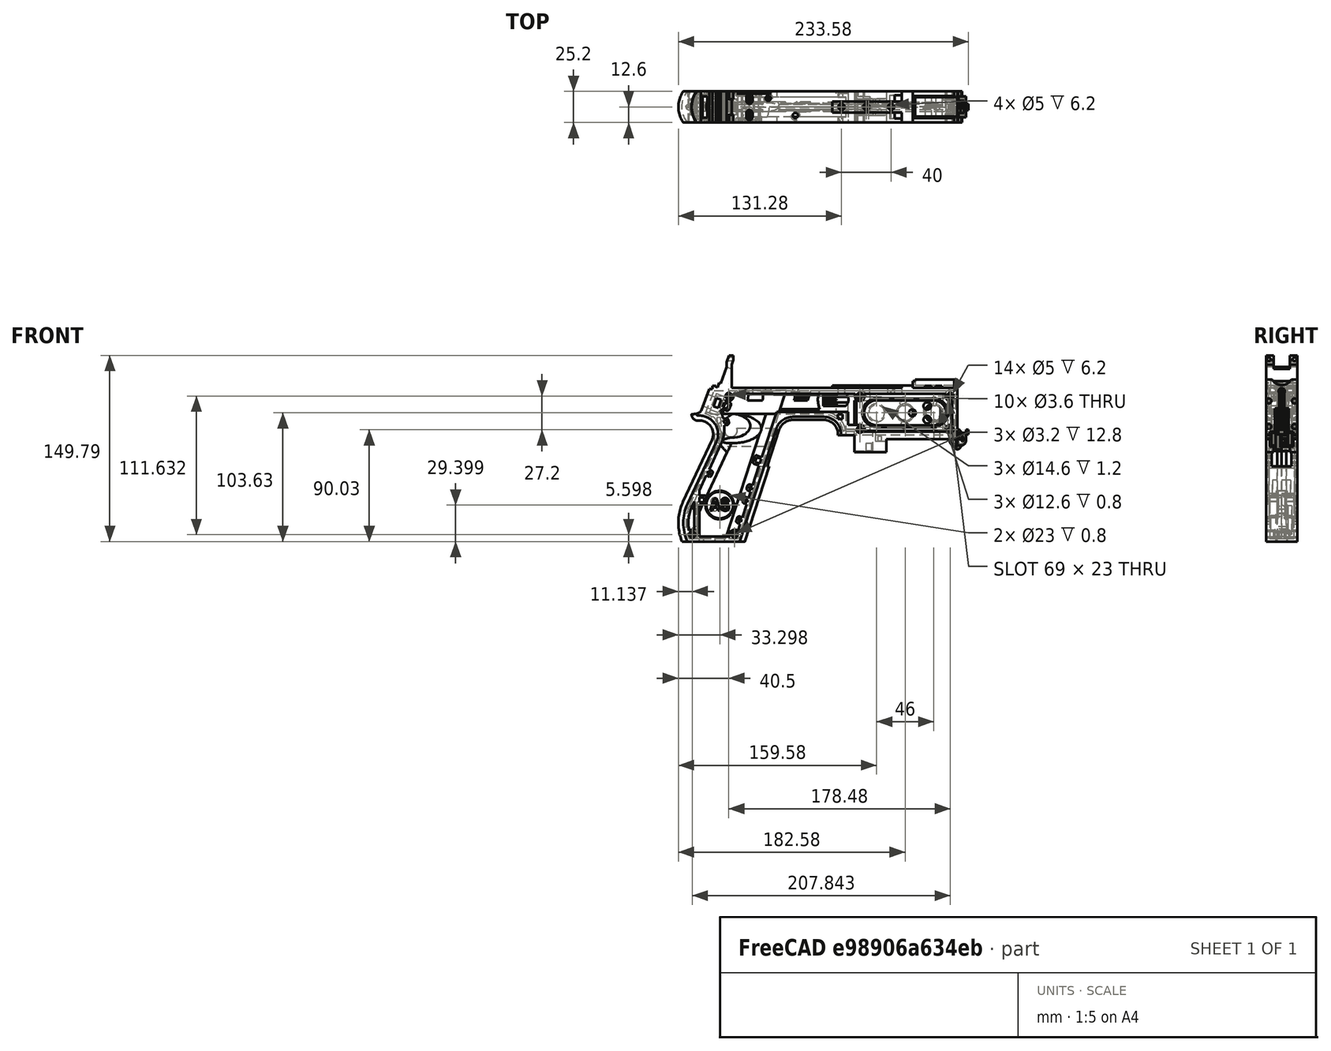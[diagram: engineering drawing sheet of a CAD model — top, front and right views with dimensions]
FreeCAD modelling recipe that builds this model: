
FCSTD DOCUMENT  (FreeCAD 1.0R39319 (Git))
Label: PICON-OF_ver_47
License: All rights reserved
LicenseURL: https://en.wikipedia.org/wiki/All_rights_reserved
objects: Sketcher::SketchObject×119, Part::Extrusion×62, Part::Cut×48, PartDesign::Pad×29, PartDesign::Pocket×18, PartDesign::Chamfer×15, PartDesign::Body×10, PartDesign::Fillet×6, Part::MultiFuse×4, Part::Part2DObjectPython×4, PartDesign::SubtractivePipe×4, PartDesign::SubtractiveLoft×4, PartDesign::Plane×2, PartDesign::SubShapeBinder×2, Part::Sweep×1, PartDesign::ShapeBinder×1, Mesh::Feature×1
note: 600 computed .brp shape members not serialized (recipe doc carries the construction recipe); baked Part::Feature solids carry a one-line shape summary decoded from their .brp

FEATURE [Sketcher::SketchObject] Sketch  label="corpo principale"
  ArcFitTolerance = 1e-06
  AttacherType = Attacher::AttachEngine3D
  AttachmentSupport = -> [XZ_Plane]
  FullyConstrained = true
  MakeInternals = false
  MapMode = 5
  Placement = pos=(0,0,0) rot=(1,0,0;1.5708rad)
  sketch-geometry (65):
    g0: LineSegment StartX=0 StartY=0 StartZ=0 EndX=-57.2 EndY=0 EndZ=0
    g1: LineSegment StartX=-57.2 StartY=0 StartZ=0 EndX=-57.2 EndY=-10.4 EndZ=0
    g2: LineSegment StartX=-57.2 StartY=-10.4 StartZ=0 EndX=-82.8 EndY=-10.4 EndZ=0
    g3: LineSegment StartX=-82.8 StartY=-10.4 StartZ=0 EndX=-82.8 EndY=3.2 EndZ=0
    g4: LineSegment StartX=-82.8 StartY=3.2 StartZ=0 EndX=-93.6 EndY=3.2 EndZ=0
    g5: LineSegment StartX=-93.6 StartY=3.2 StartZ=0 EndX=-93.6 EndY=4 EndZ=0
    g6: LineSegment StartX=-107.6 StartY=18 StartZ=0 EndX=-132.428 EndY=18 EndZ=0
    g7: LineSegment StartX=-145.743 StartY=8.32624 StartZ=0 EndX=-175.232 EndY=-82.4316 EndZ=0
    g8: LineSegment StartX=-175.232 StartY=-82.4316 StartZ=0 EndX=-217.232 EndY=-82.4316 EndZ=0
    g9: LineSegment StartX=-217.232 StartY=-52.1862 StartZ=0 EndX=-193.988 EndY=-2.33927 EndZ=0
    g10: LineSegment StartX=-206.196 StartY=23.0857 StartZ=0 EndX=-199.861 EndY=40.4914 EndZ=0
    g11: LineSegment StartX=-199.861 StartY=40.4914 StartZ=0 EndX=-197.061 EndY=40.4914 EndZ=0
    g12: LineSegment StartX=-197.061 StartY=40.4914 StartZ=0 EndX=-197.061 EndY=42.8914 EndZ=0
    g13: LineSegment StartX=-197.061 StartY=42.8914 StartZ=0 EndX=-194.261 EndY=42.8914 EndZ=0
    g14: LineSegment StartX=-194.261 StartY=42.8914 StartZ=0 EndX=-194.535 EndY=42.1397 EndZ=0
    g15: LineSegment StartX=-194.535 StartY=42.1397 StartZ=0 EndX=-193.031 EndY=41.5924 EndZ=0
    g16: LineSegment StartX=-193.031 StartY=41.5924 StartZ=0 EndX=-191.663 EndY=45.3512 EndZ=0
    g17: LineSegment StartX=-191.663 StartY=45.3512 StartZ=0 EndX=-190.536 EndY=44.9408 EndZ=0
    g18: LineSegment StartX=-190.536 StartY=44.9408 StartZ=0 EndX=-185.747 EndY=58.0965 EndZ=0
    g19: LineSegment StartX=-185.747 StartY=58.0965 StartZ=0 EndX=-185.747 EndY=62.0965 EndZ=0
    g20: LineSegment StartX=-185.747 StartY=62.0965 StartZ=0 EndX=-183.832 EndY=67.3588 EndZ=0
    g21: LineSegment StartX=-183.832 StartY=67.3588 StartZ=0 EndX=-180.232 EndY=67.3588 EndZ=0
    g22: LineSegment StartX=-180.232 StartY=67.3588 StartZ=0 EndX=-180.232 EndY=63.7588 EndZ=0
    g23: LineSegment StartX=-180.232 StartY=63.7588 StartZ=0 EndX=-181.6 EndY=60 EndZ=0
    g24: LineSegment StartX=-181.6 StartY=60 StartZ=0 EndX=-181.6 EndY=41.2 EndZ=0
    g25: LineSegment StartX=-181.6 StartY=41.2 StartZ=0 EndX=-100.8 EndY=41.2 EndZ=0
    g26: LineSegment StartX=-36 StartY=43.2 StartZ=0 EndX=-36 EndY=41.2 EndZ=0
    g27: LineSegment StartX=0 StartY=48 StartZ=0 EndX=0 EndY=0 EndZ=0
    g28: LineSegment StartX=-209.901 StartY=19.85 StartZ=0 EndX=-209.901 EndY=20.1 EndZ=0
    g29: LineSegment StartX=-208.001 StartY=22 StartZ=0 EndX=-207.747 EndY=22 EndZ=0
    g30: LineSegment StartX=-207.583 StartY=19 StartZ=0 EndX=-209.051 EndY=19 EndZ=0
    g31: ArcOfCircle CenterX=-208.001 CenterY=20.1 CenterZ=0 NormalX=0 NormalY=0 NormalZ=1 AngleXU=0 Radius=1.9 StartAngle=1.5708 EndAngle=3.14159
    g32: GeomPoint [constr] X=-209.901 Y=22 Z=0
    g33: ArcOfCircle CenterX=-209.051 CenterY=19.85 CenterZ=0 NormalX=0 NormalY=0 NormalZ=1 AngleXU=0 Radius=0.85 StartAngle=3.14159 EndAngle=4.71239
    g34: GeomPoint [constr] X=-209.901 Y=19 Z=0
    g35: ArcOfCircle CenterX=-207.747 CenterY=23.65 CenterZ=0 NormalX=0 NormalY=0 NormalZ=1 AngleXU=0 Radius=1.65 StartAngle=4.71239 EndAngle=5.93412
    g36: GeomPoint [constr] X=-206.591 Y=22 Z=0
    g37: LineSegment StartX=-4 StartY=6 StartZ=0 EndX=-4 EndY=36.4 EndZ=0
    g38: LineSegment StartX=-4 StartY=36.4 StartZ=0 EndX=-185.2 EndY=36.4 EndZ=0
    g39: LineSegment StartX=-185.2 StartY=36.4 StartZ=0 EndX=-190.441 EndY=22 EndZ=0
    g40: LineSegment StartX=-214.575 StartY=-78.4316 StartZ=0 EndX=-178.142 EndY=-78.4316 EndZ=0
    g41: LineSegment StartX=-178.142 StartY=-78.4316 StartZ=0 EndX=-145.51 EndY=22 EndZ=0
    g42: LineSegment StartX=-145.51 StartY=22 StartZ=0 EndX=-87.91 EndY=22 EndZ=0
    g43: LineSegment StartX=-87.91 StartY=22 StartZ=0 EndX=-87.91 EndY=11.6 EndZ=0
    g44: LineSegment StartX=-87.91 StartY=11.6 StartZ=0 EndX=-80.11 EndY=11.6 EndZ=0
    g45: LineSegment StartX=-80.11 StartY=11.6 StartZ=0 EndX=-80.11 EndY=6 EndZ=0
    g46: LineSegment StartX=-80.11 StartY=6 StartZ=0 EndX=-4 EndY=6 EndZ=0
    g47: LineSegment StartX=-190.363 StartY=-4.02975 StartZ=0 EndX=-213.607 EndY=-53.8767 EndZ=0
    g48: ArcOfCircle CenterX=-132.428 CenterY=4 CenterZ=0 NormalX=0 NormalY=0 NormalZ=1 AngleXU=0 Radius=14 StartAngle=1.5708 EndAngle=2.82743
    g49: GeomPoint [constr] X=-142.6 Y=18 Z=0
    g50: ArcOfCircle CenterX=-107.6 CenterY=4 CenterZ=0 NormalX=0 NormalY=0 NormalZ=1 AngleXU=0 Radius=14 StartAngle=0 EndAngle=1.5708
    g51: GeomPoint [constr] X=-93.6 Y=18 Z=0
    g52: ArcOfCircle CenterX=-184.801 CenterY=-67.3089 CenterZ=0 NormalX=0 NormalY=0 NormalZ=1 AngleXU=0 Radius=35.7833 StartAngle=2.70526 EndAngle=3.57792
    g53: ArcOfCircle CenterX=-207.583 CenterY=4 CenterZ=0 NormalX=0 NormalY=0 NormalZ=1 AngleXU=0 Radius=15 StartAngle=5.84685 EndAngle=7.85398
    g54: LineSegment [constr] StartX=-213.607 StartY=-53.8767 StartZ=0 EndX=-217.232 EndY=-52.1862 EndZ=0
    g55: ArcOfCircle CenterX=-184.801 CenterY=-67.3089 CenterZ=0 NormalX=0 NormalY=0 NormalZ=1 AngleXU=0 Radius=31.7833 StartAngle=2.70526 EndAngle=3.49911
    g56: ArcOfCircle CenterX=-218.095 CenterY=8.90192 CenterZ=0 NormalX=0 NormalY=0 NormalZ=1 AngleXU=0 Radius=30.5989 StartAngle=5.84685 EndAngle=6.72553
    g57: LineSegment StartX=-44.6 StartY=43.2 StartZ=0 EndX=-36 EndY=43.2 EndZ=0
    g58: LineSegment StartX=-100.8 StartY=41.2 StartZ=0 EndX=-44.6 EndY=41.2 EndZ=0
    g59: LineSegment StartX=-44.6 StartY=41.2 StartZ=0 EndX=-44.6 EndY=43.2 EndZ=0
    g60: LineSegment StartX=-2.4 StartY=48 StartZ=0 EndX=0 EndY=48 EndZ=0
    g61: LineSegment StartX=-36 StartY=41.2 StartZ=0 EndX=-2.4 EndY=41.2 EndZ=0
    g62: LineSegment StartX=-2.4 StartY=41.2 StartZ=0 EndX=-2.4 EndY=48 EndZ=0
    g63: LineSegment [constr] StartX=-181.6 StartY=36.4 StartZ=0 EndX=-152.209 EndY=36.4 EndZ=0
    g64: LineSegment [constr] StartX=-181.6 StartY=36.4 StartZ=0 EndX=-130.41 EndY=36.4 EndZ=0
  constraints (183):
    c: Coincident(g-1,g0)
    c: PointOnObject(g0,g-1)
    c: Coincident(g0,g1)
    c: Vertical(g1)
    c: Coincident(g1,g2)
    c: Horizontal(g2)
    c: Coincident(g2,g3)
    c: Vertical(g3)
    c: Coincident(g3,g4)
    c: Coincident(g4,g5)
    c: Vertical(g5)
    c: Horizontal(g6)
    c: Coincident(g7,g8)
    c: Horizontal(g8)
    c: Coincident(g10,g11)
    c: Horizontal(g11)
    c: Coincident(g11,g12)
    c: Vertical(g12)
    c: Coincident(g12,g13)
    c: Horizontal(g13)
    c: Coincident(g13,g14)
    c: Coincident(g14,g15)
    c: Coincident(g15,g16)
    c: Coincident(g16,g17)
    c: Coincident(g17,g18)
    c: Coincident(g18,g19)
    c: Vertical(g19)
    c: Coincident(g19,g20)
    c: Coincident(g20,g21)
    c: Horizontal(g21)
    c: Coincident(g21,g22)
    c: Vertical(g22)
    c: Coincident(g22,g23)
    c: Coincident(g23,g24)
    c: Vertical(g24)
    c: Coincident(g24,g25)
    c: Horizontal(g25)
    c: Coincident(g57,g26)
    c: Vertical(g26)
    c: Coincident(g26,g61)
    c: PointOnObject(g60,g-2)
    c: Coincident(g60,g27)
    c: Coincident(g27,g0)
    c: DistanceY(g27,g27) = 48
    c: DistanceY(g1,g1) = 10.4
    c: DistanceX(g0,g0) = 57.2
    c: DistanceX(g2,g2) = 25.6
    c: Horizontal(g4)
    c: DistanceY(g3,g3) = 13.6
    c: DistanceX(g4,g4) = 10.8
    c: DistanceY(g5,g51) = 14.8
    c: DistanceX(g49,g51) = 49
    c: Distance(g7,g49) = 105.6
    c: DistanceX(g61,g60) = 36
    c: DistanceX(g25,g25) = 80.8
    c: DistanceY(g24,g24) = 18.8
    c: DistanceY(g22,g22) = 3.6
    c: Distance(g23) = 4
    c: Angle(g-1,g23) = 1.22173
    c: DistanceX(g21,g21) = 3.6
    c: Distance(g20) = 5.6
    c: Angle(g-1,g20) = 1.22173
    c: DistanceY(g19,g19) = 4
    c: Distance(g18) = 14
    c: Angle(g-1,g18) = 1.22173
    c: Distance(g17) = 1.2
    c: Distance(g16) = 4
    c: Angle(g16) = 1.22173
    c: Perpendicular(g18,g17)
    c: Distance(g15) = 1.6
    c: Perpendicular(g16,g15)
    c: Distance(g14) = 0.8
    c: DistanceX(g13,g13) = 2.8
    c: Perpendicular(g15,g14)
    c: DistanceY(g12,g12) = 2.4
    c: DistanceX(g11,g11) = 2.8
    c: Distance(g9) = 55
    c: Angle(g9,g-1) = 2.00713
    c: Horizontal(g29)
    c: Vertical(g28)
    c: Horizontal(g30)
    c: PointOnObject(g32,g29)
    c: PointOnObject(g32,g28)
    c: Tangent(g29,g31) = 1.5708
    c: Tangent(g28,g31) = 1.5708
    c: PointOnObject(g34,g28)
    c: PointOnObject(g34,g30)
    c: Tangent(g28,g33) = 1.5708
    c: Tangent(g30,g33) = 1.5708
    c: PointOnObject(g36,g29)
    c: PointOnObject(g36,g10)
    c: Tangent(g29,g35) = -1.5708
    c: Tangent(g10,g35) = -1.5708
    c: Angle(g-1,g10) = 1.22173
    c: Radius(g35) = 1.65
    c: Vertical(g37)
    c: Coincident(g37,g38)
    c: Horizontal(g38)
    c: Coincident(g38,g39)
    c: Horizontal(g40)
    c: Coincident(g40,g41)
    c: Coincident(g41,g42)
    c: Horizontal(g42)
    c: Coincident(g42,g43)
    c: Vertical(g43)
    c: Coincident(g43,g44)
    c: Horizontal(g44)
    c: Coincident(g44,g45)
    c: Vertical(g45)
    c: Coincident(g45,g46)
    c: Coincident(g46,g37)
    c: Horizontal(g46)
    c: DistanceY(g0,g37) = 6
    c: DistanceX(g37,g0) = 4
    c: DistanceY(g37,g25) = 4.8
    c: DistanceX(g38,g38) = 181.2
    c: DistanceX(g42,g42) = 57.6
    c: DistanceY(g49,g41) = 4
    c: DistanceX(g41,g49) = 2.91
    c: DistanceY(g43,g43) = 10.4
    c: DistanceX(g44,g44) = 7.8
    c: DistanceY(g7,g40) = 4
    c: Distance(g47) = 55
    c: Angle(g-1,g39) = 1.22173
    c: PointOnObject(g49,g7)
    c: PointOnObject(g49,g6)
    c: Tangent(g7,g48) = -1.5708
    c: Tangent(g6,g48) = -1.5708
    c: PointOnObject(g51,g5)
    c: PointOnObject(g51,g6)
    c: Tangent(g5,g50) = -1.5708
    c: Tangent(g6,g50) = -1.5708
    c: Radius(g50) = 14
    c: Radius(g48) = 14
    c: DistanceX(g8,g8) = 42
    c: Angle(g7,g-1) = 1.88496
    c: Parallel(g41,g7)
    c: Parallel(g47,g9)
    c: Coincident(g52,g8)
    c: Tangent(g52,g9) = 1.5708
    c: DistanceX(g9,g8) = 0
    c: Tangent(g53,g9) = -1.5708
    c: Tangent(g53,g30) = -1.5708
    c: Diameter(g53) = 30
    c: DistanceY(g53,g0) = -4
    c: Coincident(g54,g47)
    c: Distance(g54) = 4
    c: Coincident(g54,g9)
    c: Coincident(g55,g40)
    c: Tangent(g55,g47) = -1.5708
    c: Coincident(g52,g55)
    c: Coincident(g56,g39)
    c: Tangent(g56,g47) = 1.5708
    c: Horizontal(g57)
    c: DistanceX(g57,g57) = 8.6
    c: Coincident(g58,g25)
    c: Horizontal(g58)
    c: Coincident(g59,g58)
    c: Vertical(g59)
    c: DistanceY(g58,g57) = 2
    c: DistanceX(g58,g58) = 56.2
    c: Coincident(g59,g57)
    c: DistanceY(g41,g36) = 0
    c: DistanceY(g36,g39) = 0
    c: DistanceY(g28,g28) = 0.25
    c: DistanceX(g30,g36) = 2.46
    c: DistanceX(g28,g29) = 1.9
    c: Coincident(g62,g60)
    c: Horizontal(g60)
    c: DistanceX(g62,g27) = 2.4
    c: Coincident(g61,g62)
    c: DistanceY(g26,g26) = 2
    c: Vertical(g62)
    c: DistanceY(g61,g60) = 6.8
    c: Horizontal(g61)
    c: Distance(g63) = 29.391
    c: PointOnObject(g63,g38)
    c: PointOnObject(g63,g38)
    c: Distance(g64) = 51.19
    c: PointOnObject(g64,g38)
    c: PointOnObject(g64,g38)
    c: DistanceX(g24,g63) = 0
    c: DistanceX(g24,g64) = 0
FEATURE [Part::Extrusion] Extrude  label="Extrude corpo principale"
  Base = -> Sketch
  Dir = (0,-1,2e-16)
  DirMode = 2
  FaceMakerClass = Part::FaceMakerBullseye
  FaceMakerMode = 3
  LengthFwd = 25.2
  LengthRev = 12.6
  Solid = true
  Symmetric = true
FEATURE [Sketcher::SketchObject] Sketch002  label="scavo grilletto"
  ArcFitTolerance = 1e-06
  AttachmentSupport = -> [XZ_Plane]
  ExternalGeometry = -> [Sketch]
  FullyConstrained = true
  MakeInternals = false
  MapMode = 5
  Placement = pos=(0,0,0) rot=(1,0,0;1.5708rad)
  sketch-geometry (4):
    g0: LineSegment StartX=-89.51 StartY=22 StartZ=0 EndX=-152.71 EndY=22 EndZ=0
    g1: LineSegment StartX=-152.71 StartY=22 StartZ=0 EndX=-167.006 EndY=-22 EndZ=0
    g2: LineSegment StartX=-167.006 StartY=-22 StartZ=0 EndX=-89.51 EndY=-22 EndZ=0
    g3: LineSegment StartX=-89.51 StartY=-22 StartZ=0 EndX=-89.51 EndY=22 EndZ=0
  constraints (12):
    c: Horizontal(g0)
    c: Coincident(g0,g1)
    c: Coincident(g1,g2)
    c: Horizontal(g2)
    c: Coincident(g2,g3)
    c: Coincident(g3,g0)
    c: Vertical(g3)
    c: Angle(g1,g0) = 1.88496
    c: DistanceY(g3,g3) = 44
    c: DistanceX(g0,g0) = 63.2
    c: DistanceX(g0,g-3) = 1.6
    c: DistanceY(g-3,g0) = 0
FEATURE [Sketcher::SketchObject] Sketch004  label="traiettoria arrotondamento impugnatura anteriore"
  ArcFitTolerance = 1e-06
  AttachmentSupport = -> [XZ_Plane]
  ExternalGeometry = -> [Sketch]
  FullyConstrained = true
  MakeInternals = false
  MapMode = 5
  Placement = pos=(0,0,0) rot=(1,0,0;1.5708rad)
  sketch-geometry (13):
    g0: LineSegment StartX=-175.232 StartY=-82.4316 StartZ=0 EndX=-145.743 EndY=8.32624 EndZ=0
    g1: LineSegment StartX=-93.6 StartY=3.2 StartZ=0 EndX=-93.6 EndY=4 EndZ=0
    g2: LineSegment StartX=-132.428 StartY=18 StartZ=0 EndX=-107.6 EndY=18 EndZ=0
    g3: ArcOfCircle CenterX=-132.428 CenterY=4 CenterZ=0 NormalX=0 NormalY=0 NormalZ=1 AngleXU=0 Radius=14 StartAngle=1.5708 EndAngle=2.82743
    g4: ArcOfCircle CenterX=-107.6 CenterY=4 CenterZ=0 NormalX=0 NormalY=0 NormalZ=1 AngleXU=0 Radius=14 StartAngle=0 EndAngle=1.5708
    g5: LineSegment StartX=-175.232 StartY=-82.4316 StartZ=0 EndX=-217.232 EndY=-82.4316 EndZ=0
    g6: LineSegment StartX=-217.232 StartY=-52.1862 StartZ=0 EndX=-193.988 EndY=-2.33927 EndZ=0
    g7: LineSegment StartX=-209.051 StartY=19 StartZ=0 EndX=-207.583 EndY=19 EndZ=0
    g8: LineSegment StartX=-209.901 StartY=20.1 StartZ=0 EndX=-209.901 EndY=19.85 EndZ=0
    g9: ArcOfCircle CenterX=-184.801 CenterY=-67.3089 CenterZ=0 NormalX=0 NormalY=0 NormalZ=1 AngleXU=0 Radius=35.7833 StartAngle=2.70526 EndAngle=3.57792
    g10: ArcOfCircle CenterX=-207.583 CenterY=4 CenterZ=0 NormalX=0 NormalY=0 NormalZ=1 AngleXU=0 Radius=15 StartAngle=5.84685 EndAngle=7.85398
    g11: ArcOfCircle CenterX=-209.051 CenterY=19.85 CenterZ=0 NormalX=0 NormalY=0 NormalZ=1 AngleXU=0 Radius=0.85 StartAngle=3.14159 EndAngle=4.71239
    g12: ArcOfCircle CenterX=-208.001 CenterY=20.1 CenterZ=0 NormalX=0 NormalY=0 NormalZ=1 AngleXU=0 Radius=1.9 StartAngle=1.5708 EndAngle=3.14159
  constraints (26):
    c: Coincident(g0,g-3)
    c: Coincident(g0,g-6)
    c: Coincident(g1,g-8)
    c: Coincident(g1,g-7)
    c: Coincident(g2,g-5)
    c: Coincident(g2,g-4)
    c: Coincident(g3,g2)
    c: Tangent(g3,g0) = 1.5708
    c: Coincident(g4,g1)
    c: Tangent(g4,g2) = 1.5708
    c: Coincident(g5,g0)
    c: Coincident(g5,g-9)
    c: Coincident(g6,g-12)
    c: Coincident(g6,g-11)
    c: Coincident(g7,g-15)
    c: Coincident(g7,g-14)
    c: Coincident(g8,g-16)
    c: Coincident(g8,g-17)
    c: Tangent(g9,g6) = 1.5708
    c: Coincident(g9,g5)
    c: Coincident(g10,g7)
    c: Tangent(g10,g6) = -1.5708
    c: Tangent(g11,g7) = -1.5708
    c: Coincident(g11,g8)
    c: Tangent(g12,g8) = -1.5708
    c: Coincident(g12,g-17)
FEATURE [PartDesign::Plane] DatumPlane  label="Piano per disegno arrotondamento impugnatura"
  AttachmentSupport = -> [Sketch]
  Length = 73.6581
  MapMode = 7
  Placement = pos=(-145.743,1.8e-15,8.32624) rot=(0.154555,0.154555,0.97582;1.59527rad)
  ResizeMode = 0
  Width = 303.511
FEATURE [Sketcher::SketchObject] Sketch005  label="forma arrotondamento impugnatura anteriore"
  ArcFitTolerance = 1e-06
  AttachmentSupport = -> [DatumPlane]
  FullyConstrained = true
  MakeInternals = false
  MapMode = 5
  Placement = pos=(-145.743,1.8e-15,8.32624) rot=(0.154555,0.154555,0.97582;1.59527rad)
  sketch-geometry (5):
    g0: GeomPoint [constr] X=0 Y=-4 Z=0
    g1: GeomPoint [constr] X=-12.6 Y=7.1e-15 Z=0
    g2: GeomPoint [constr] X=12.6 Y=4.97e-14 Z=0
    g3: LineSegment StartX=-12.6 StartY=7.1e-15 StartZ=0 EndX=12.6 EndY=4.97e-14 EndZ=0
    g4: ArcOfCircle CenterX=-3.88e-14 CenterY=17.845 CenterZ=0 NormalX=0 NormalY=0 NormalZ=1 AngleXU=0 Radius=21.845 StartAngle=4.09759 EndAngle=5.32718
  constraints (11):
    c: DistanceY(g0,g-1) = 4
    c: DistanceX(g-1,g0) = 0
    c: DistanceX(g1,g-1) = 12.6
    c: DistanceX(g-1,g2) = 12.6
    c: DistanceY(g-1,g2) = 0
    c: DistanceY(g-1,g1) = 0
    c: Coincident(g3,g1)
    c: Coincident(g3,g2)
    c: Coincident(g4,g1)
    c: Coincident(g4,g2)
    c: PointOnObject(g0,g4)
FEATURE [Part::Sweep] Sweep  label="Sweep impugnatura"
  Frenet = true
  Sections = -> [Sketch005]
  Solid = true
  Spine = -> Sketch [Edge32,Edge33,Edge34,Edge35,Edge36,Edge37,Edge38,Edge39,Edge40,Edge41,Edge42,Edge43,Edge44]
  Transition = 1
FEATURE [Sketcher::SketchObject] Sketch008  label="buchi e pulizie varie"
  ArcFitTolerance = 1e-06
  AttachmentSupport = -> [XZ_Plane]
  ExternalGeometry = -> [Sketch]
  FullyConstrained = true
  MakeInternals = false
  MapMode = 5
  Placement = pos=(0,0,0) rot=(1,0,0;1.5708rad)
  sketch-geometry (26):
    g0: LineSegment StartX=-96.278 StartY=20.155 StartZ=0 EndX=-92.278 EndY=20.155 EndZ=0
    g1: LineSegment StartX=-92.278 StartY=20.155 StartZ=0 EndX=-92.278 EndY=16.155 EndZ=0
    g2: LineSegment StartX=-92.278 StartY=16.155 StartZ=0 EndX=-96.278 EndY=16.155 EndZ=0
    g3: LineSegment StartX=-96.278 StartY=16.155 StartZ=0 EndX=-96.278 EndY=20.155 EndZ=0
    g4: LineSegment StartX=-222.232 StartY=-82.4316 StartZ=0 EndX=-170.232 EndY=-82.4316 EndZ=0
    g5: LineSegment StartX=-170.232 StartY=-82.4316 StartZ=0 EndX=-170.232 EndY=-86.4316 EndZ=0
    g6: LineSegment StartX=-170.232 StartY=-86.4316 StartZ=0 EndX=-222.232 EndY=-86.4316 EndZ=0
    g7: LineSegment StartX=-222.232 StartY=-86.4316 StartZ=0 EndX=-222.232 EndY=-82.4316 EndZ=0
    g8: LineSegment StartX=-213.901 StartY=20.1 StartZ=0 EndX=-213.901 EndY=26 EndZ=0
    g9: LineSegment StartX=-213.901 StartY=26 StartZ=0 EndX=-206.196 EndY=26 EndZ=0
    g10: LineSegment StartX=-17.4 StartY=42.8 StartZ=0 EndX=-12.4 EndY=42.8 EndZ=0
    g11: LineSegment StartX=-12.4 StartY=42.8 StartZ=0 EndX=-12.4 EndY=41.2 EndZ=0
    g12: LineSegment StartX=-12.4 StartY=41.2 StartZ=0 EndX=-17.4 EndY=41.2 EndZ=0
    g13: LineSegment StartX=-17.4 StartY=41.2 StartZ=0 EndX=-17.4 EndY=42.8 EndZ=0
    g14: LineSegment StartX=-25.9 StartY=42.8 StartZ=0 EndX=-20.9 EndY=42.8 EndZ=0
    g15: LineSegment StartX=-20.9 StartY=42.8 StartZ=0 EndX=-20.9 EndY=41.2 EndZ=0
    g16: LineSegment StartX=-20.9 StartY=41.2 StartZ=0 EndX=-25.9 EndY=41.2 EndZ=0
    g17: LineSegment StartX=-25.9 StartY=41.2 StartZ=0 EndX=-25.9 EndY=42.8 EndZ=0
    g18: GeomPoint [constr] X=-206.196 Y=23.0857 Z=0
    g19: GeomPoint [constr] X=-213.901 Y=20.1 Z=0
    g20: BSplineCurve PolesCount=4 KnotsCount=2 Degree=3 IsPeriodic=0
    g21-g24: Circle [constr] x4 (B-spline internal-alignment scaffolding for g20; pole/knot coordinates omitted)
    g25: LineSegment StartX=-206.196 StartY=26 StartZ=0 EndX=-206.196 EndY=23.0857 EndZ=0
  constraints (73):
    c: Horizontal(g0)
    c: Coincident(g1,g0)
    c: Vertical(g1)
    c: Coincident(g2,g1)
    c: Horizontal(g2)
    c: Coincident(g3,g2)
    c: Coincident(g3,g0)
    c: Vertical(g3)
    c: DistanceX(g0,g-4) = 4.368
    c: DistanceY(g0,g-4) = 1.845
    c: DistanceY(g1,g1) = 4
    c: DistanceX(g2,g2) = 4
    c: Horizontal(g4)
    c: Coincident(g5,g4)
    c: Vertical(g5)
    c: Coincident(g6,g5)
    c: Horizontal(g6)
    c: Coincident(g7,g6)
    c: Coincident(g7,g4)
    c: Vertical(g7)
    c: DistanceY(g7,g7) = 4
    c: DistanceX(g4,g-5) = 5
    c: DistanceX(g-5,g4) = 5
    c: DistanceY(g4,g-5) = 0
    c: Coincident(g9,g8)
    c: Parallel(g9,g-6)
    c: DistanceX(g8,g-8) = 4
    c: Horizontal(g10)
    c: Coincident(g11,g10)
    c: Vertical(g11)
    c: Coincident(g12,g11)
    c: Horizontal(g12)
    c: Coincident(g13,g12)
    c: Coincident(g13,g10)
    c: Vertical(g13)
    c: Horizontal(g14)
    c: Coincident(g15,g14)
    c: Vertical(g15)
    c: Coincident(g16,g15)
    c: Horizontal(g16)
    c: Coincident(g17,g16)
    c: Coincident(g17,g14)
    c: Vertical(g17)
    c: DistanceY(g11,g10) = 1.6
    c: DistanceX(g10,g10) = 5
    c: DistanceY(g15,g14) = 1.6
    c: DistanceX(g14,g14) = 5
    c: DistanceX(g15,g12) = 3.5
    c: DistanceX(g11,g-9) = 10
    c: DistanceY(g-9,g11) = 0
    c: DistanceY(g-9,g15) = 0
    c: Perpendicular(g8,g9)
    c: DistanceY(g-7,g9) = 4
    c: DistanceY(g8,g-8) = 0
    c: InternalAlignment(g18,g20)
    c: InternalAlignment(g19,g20)
    c: InternalAlignment(g21,g20)
    c: Weight(g21) = 1
    c: InternalAlignment(g22,g20)
    c: Equal(g22,g21)
    c: InternalAlignment(g23,g20)
    c: Equal(g23,g21)
    c: InternalAlignment(g24,g20)
    c: Equal(g24,g21)
    c: Coincident(g18,g-12)
    c: Coincident(g19,g8)
    c: Coincident(g25,g9)
    c: Coincident(g25,g20)
    c: Vertical(g25)
    c: DistanceY(g20,g23) = 0
    c: DistanceY(g22,g18) = 2.26
    c: DistanceX(g22,g18) = 0.93
    c: DistanceX(g20,g23) = 2.9
FEATURE [Part::Extrusion] Extrude004  label="Extrude Buchi e pulizie varie"
  Base = -> Sketch008
  Dir = (0,-1,2e-16)
  DirMode = 2
  FaceMakerClass = Part::FaceMakerBullseye
  FaceMakerMode = 3
  LengthFwd = 25.2
  LengthRev = 0
  Solid = true
  Symmetric = true
FEATURE [Sketcher::SketchObject] Sketch009  label="rinforzi"
  ArcFitTolerance = 1e-06
  AttachmentSupport = -> [XZ_Plane]
  ExternalGeometry = -> [Sketch]
  FullyConstrained = true
  MakeInternals = false
  MapMode = 5
  Placement = pos=(0,0,0) rot=(1,0,0;1.5708rad)
  sketch-geometry (9):
    g0: LineSegment StartX=-87.91 StartY=22 StartZ=0 EndX=-87.91 EndY=36.4 EndZ=0
    g1: LineSegment StartX=-87.91 StartY=36.4 StartZ=0 EndX=-97.91 EndY=36.4 EndZ=0
    g2: LineSegment StartX=-97.91 StartY=36.4 StartZ=0 EndX=-97.91 EndY=22 EndZ=0
    g3: LineSegment StartX=-97.91 StartY=22 StartZ=0 EndX=-87.91 EndY=22 EndZ=0
    g4: LineSegment StartX=-149.713 StartY=9.06563 StartZ=0 EndX=-154.586 EndY=-5.93437 EndZ=0
    g5: LineSegment StartX=-154.586 StartY=-5.93437 StartZ=0 EndX=-191.863 EndY=-5.93437 EndZ=0
    g6: LineSegment StartX=-191.863 StartY=-5.93437 StartZ=0 EndX=-191.863 EndY=9.06563 EndZ=0
    g7: LineSegment StartX=-191.863 StartY=9.06563 StartZ=0 EndX=-149.713 EndY=9.06563 EndZ=0
    g8: LineSegment [constr] StartX=-145.51 StartY=22 StartZ=0 EndX=-149.713 EndY=9.06563 EndZ=0
  constraints (25):
    c: Vertical(g0)
    c: Coincident(g1,g0)
    c: Horizontal(g1)
    c: Coincident(g2,g1)
    c: Vertical(g2)
    c: Coincident(g3,g2)
    c: Coincident(g3,g0)
    c: Horizontal(g3)
    c: Coincident(g0,g-4)
    c: DistanceX(g3,g3) = 10
    c: DistanceY(g0,g-3) = 0
    c: Coincident(g5,g4)
    c: Horizontal(g5)
    c: Coincident(g6,g5)
    c: Vertical(g6)
    c: Coincident(g7,g6)
    c: Coincident(g7,g4)
    c: Horizontal(g7)
    c: Distance(g8) = 13.6
    c: Parallel(g-6,g8)
    c: Coincident(g-6,g8)
    c: Parallel(g4,g-6)
    c: DistanceY(g4,g4) = 15
    c: Coincident(g4,g8)
    c: DistanceX(g-5,g5) = -1.5
FEATURE [Part::Extrusion] Extrude001  label="Extrude scavo grilletto"
  Base = -> Sketch002
  Dir = (0,-1,2e-16)
  DirMode = 2
  FaceMakerClass = Part::FaceMakerBullseye
  FaceMakerMode = 3
  LengthFwd = 16
  LengthRev = 0
  Solid = true
  Symmetric = true
FEATURE [Part::Extrusion] Extrude005  label="Extrude Rinforzi"
  Base = -> Sketch009
  Dir = (0,-1,2e-16)
  DirMode = 2
  FaceMakerClass = Part::FaceMakerBullseye
  FaceMakerMode = 3
  LengthFwd = 2
  LengthRev = 0
  Placement = pos=(0,12.6,0) rot=(0,0,1;0rad)
  Solid = true
  Symmetric = false
FEATURE [PartDesign::ShapeBinder] CopyCut
  TraceSupport = false
FEATURE [PartDesign::Plane] DatumPlane001
  AttachmentSupport = -> [CopyCut]
  Length = 283.944
  MapMode = 5
  Placement = pos=(0,12.6,0) rot=(0,0.707107,0.707107;3.14159rad)
  ResizeMode = 0
  Width = 188.15
FEATURE [Sketcher::SketchObject] Sketch010  label="buco neopixel"
  ArcFitTolerance = 1e-06
  AttachmentSupport = -> [XZ_Plane]
  ExternalGeometry = -> [Sketch]
  FullyConstrained = true
  MakeInternals = false
  MapMode = 5
  Placement = pos=(0,0,0) rot=(1,0,0;1.5708rad)
  sketch-geometry (5):
    g0: LineSegment [constr] StartX=-199.861 StartY=40.4914 StartZ=0 EndX=-201.368 EndY=36.3521 EndZ=0
    g1: LineSegment StartX=-201.368 StartY=36.3521 StartZ=0 EndX=-204.932 EndY=26.5605 EndZ=0
    g2: LineSegment StartX=-201.368 StartY=36.3521 StartZ=0 EndX=-180.2 EndY=28.6477 EndZ=0
    g3: LineSegment StartX=-180.2 StartY=28.6477 StartZ=0 EndX=-183.764 EndY=18.8561 EndZ=0
    g4: LineSegment StartX=-183.764 StartY=18.8561 StartZ=0 EndX=-204.932 EndY=26.5605 EndZ=0
  constraints (14):
    c: Parallel(g0,g-3)
    c: Distance(g0) = 4.405
    c: Coincident(g0,g-3)
    c: Coincident(g2,g1)
    c: Coincident(g3,g2)
    c: Coincident(g4,g3)
    c: Coincident(g4,g1)
    c: Parallel(g1,g-3)
    c: Distance(g1) = 10.42
    c: Coincident(g1,g0)
    c: Parallel(g2,g4)
    c: Perpendicular(g1,g2)
    c: DistanceX(g-4,g2) = 5
    c: Parallel(g3,g1)
FEATURE [Part::Extrusion] Extrude006  label="Extrude buco neopixel"
  Base = -> Sketch010
  Dir = (0,-1,2e-16)
  DirMode = 2
  FaceMakerClass = Part::FaceMakerBullseye
  FaceMakerMode = 3
  LengthFwd = 17.2
  LengthRev = 0
  Solid = true
  Symmetric = true
FEATURE [Sketcher::SketchObject] Sketch011  label="fermo grilletto"
  ArcFitTolerance = 1e-06
  AttachmentSupport = -> [XZ_Plane]
  ExternalGeometry = -> [Sketch]
  FullyConstrained = true
  MakeInternals = false
  MapMode = 5
  Placement = pos=(0,0,0) rot=(1,0,0;1.5708rad)
  sketch-geometry (18):
    g0: LineSegment [constr] StartX=-145.51 StartY=22 StartZ=0 EndX=-157.347 EndY=-14.4293 EndZ=0
    g1: LineSegment [constr] StartX=-157.347 StartY=-14.4293 StartZ=0 EndX=-157.841 EndY=-15.951 EndZ=0
    g2: LineSegment StartX=-161.151 StartY=-13.1932 StartZ=0 EndX=-155.825 EndY=-14.9237 EndZ=0
    g3: LineSegment StartX=-163.167 StartY=-14.2205 StartZ=0 EndX=-164.403 EndY=-18.0247 EndZ=0
    g4: LineSegment StartX=-163.376 StartY=-20.0408 StartZ=0 EndX=-158.05 EndY=-21.7713 EndZ=0
    g5: LineSegment StartX=-158.05 StartY=-21.7713 StartZ=0 EndX=-155.825 EndY=-14.9237 EndZ=0
    g6: LineSegment StartX=-161.645 StartY=-14.7149 StartZ=0 EndX=-157.841 EndY=-15.951 EndZ=0
    g7: LineSegment StartX=-157.841 StartY=-15.951 StartZ=0 EndX=-159.077 EndY=-19.7552 EndZ=0
    g8: LineSegment StartX=-159.077 StartY=-19.7552 StartZ=0 EndX=-162.881 EndY=-18.5191 EndZ=0
    g9: LineSegment StartX=-162.881 StartY=-18.5191 StartZ=0 EndX=-161.645 EndY=-14.7149 EndZ=0
    g10: LineSegment [constr] StartX=-161.645 StartY=-14.7149 StartZ=0 EndX=-161.151 EndY=-13.1932 EndZ=0
    g11: LineSegment [constr] StartX=-159.077 StartY=-19.7552 StartZ=0 EndX=-157.555 EndY=-20.2496 EndZ=0
    g12: LineSegment [constr] StartX=-159.077 StartY=-19.7552 StartZ=0 EndX=-159.572 EndY=-21.2769 EndZ=0
    g13: LineSegment [constr] StartX=-161.645 StartY=-14.7149 StartZ=0 EndX=-163.167 EndY=-14.2205 EndZ=0
    g14: ArcOfCircle CenterX=-161.645 CenterY=-14.7149 CenterZ=0 NormalX=0 NormalY=0 NormalZ=1 AngleXU=0 Radius=1.6 StartAngle=1.25664 EndAngle=2.82743
    g15: GeomPoint [constr] X=-162.673 Y=-12.6988 Z=0
    g16: ArcOfCircle CenterX=-162.881 CenterY=-18.5191 CenterZ=0 NormalX=0 NormalY=0 NormalZ=1 AngleXU=0 Radius=1.6 StartAngle=2.82743 EndAngle=4.39823
    g17: GeomPoint [constr] X=-164.897 Y=-19.5464 Z=0
  constraints (48):
    c: Parallel(g0,g-3)
    c: Distance(g0) = 38.304
    c: Coincident(g0,g-3)
    c: Parallel(g1,g-3)
    c: Distance(g1) = 1.6
    c: Coincident(g1,g0)
    c: Coincident(g5,g4)
    c: Coincident(g5,g2)
    c: Coincident(g7,g6)
    c: Coincident(g8,g7)
    c: Coincident(g9,g8)
    c: Coincident(g9,g6)
    c: Parallel(g7,g-3)
    c: Parallel(g9,g7)
    c: Perpendicular(g6,g7)
    c: Parallel(g6,g8)
    c: Distance(g6) = 4
    c: Distance(g9) = 4
    c: Parallel(g5,g7)
    c: Parallel(g9,g3)
    c: Parallel(g2,g6)
    c: Parallel(g4,g8)
    c: Parallel(g13,g6)
    c: Parallel(g10,g9)
    c: Parallel(g11,g8)
    c: Parallel(g12,g7)
    c: Distance(g10) = 1.6
    c: Distance(g13) = 1.6
    c: Distance(g12) = 1.6
    c: Distance(g11) = 1.6
    c: Coincident(g10,g6)
    c: Coincident(g13,g6)
    c: Coincident(g12,g7)
    c: Coincident(g11,g7)
    c: Distance(g10,g15) = 1.6
    c: Distance(g15,g13) = 1.6
    c: Distance(g4,g12) = 1.6
    c: Distance(g4,g11) = 1.6
    c: PointOnObject(g15,g2)
    c: Tangent(g3,g14) = -1.5708
    c: Tangent(g2,g14) = 1.5708
    c: PointOnObject(g17,g4)
    c: PointOnObject(g17,g3)
    c: Tangent(g4,g16) = -1.5708
    c: Tangent(g3,g16) = -1.5708
    c: Equal(g16,g14)
    c: Coincident(g16,g8)
    c: Coincident(g6,g1)
FEATURE [Part::Extrusion] Extrude007  label="Extrude fermo grilletto"
  Base = -> Sketch011
  Dir = (0,-1,2e-16)
  DirMode = 2
  FaceMakerClass = Part::FaceMakerBullseye
  FaceMakerMode = 3
  LengthFwd = 25.2
  LengthRev = 0
  Solid = true
  Symmetric = true
FEATURE [Sketcher::SketchObject] Sketch012  label="buco oled"
  ArcFitTolerance = 1e-06
  AttachmentSupport = -> [XZ_Plane]
  ExternalGeometry = -> [Sketch]
  FullyConstrained = true
  MakeInternals = false
  MapMode = 5
  Placement = pos=(0,0,0) rot=(1,0,0;1.5708rad)
  sketch-geometry (4):
    g0: LineSegment StartX=-185.747 StartY=58.0965 StartZ=0 EndX=-180.232 EndY=56.0891 EndZ=0
    g1: LineSegment StartX=-185.747 StartY=58.0965 StartZ=0 EndX=-185.747 EndY=67.3588 EndZ=0
    g2: LineSegment StartX=-185.747 StartY=67.3588 StartZ=0 EndX=-180.232 EndY=67.3588 EndZ=0
    g3: LineSegment StartX=-180.232 StartY=67.3588 StartZ=0 EndX=-180.232 EndY=56.0891 EndZ=0
  constraints (10):
    c: Coincident(g1,g0)
    c: Coincident(g2,g1)
    c: Coincident(g3,g2)
    c: Coincident(g3,g0)
    c: Parallel(g1,g-5)
    c: Perpendicular(g-3,g0)
    c: Parallel(g2,g-6)
    c: Parallel(g3,g-4)
    c: Coincident(g0,g-5)
    c: Coincident(g2,g-6)
FEATURE [Part::Extrusion] Extrude008  label="Extrude buco oled"
  Base = -> Sketch012
  Dir = (0,-1,2e-16)
  DirMode = 2
  FaceMakerClass = Part::FaceMakerBullseye
  FaceMakerMode = 3
  LengthFwd = 12.8
  LengthRev = 0
  Solid = true
  Symmetric = true
FEATURE [Sketcher::SketchObject] Sketch013  label="buco pompa"
  ArcFitTolerance = 1e-06
  AttachmentSupport = -> [XZ_Plane]
  ExternalGeometry = -> [Sketch]
  FullyConstrained = true
  MakeInternals = false
  MapMode = 5
  Placement = pos=(0,0,0) rot=(1,0,0;1.5708rad)
  sketch-geometry (8):
    g0: LineSegment StartX=-82.8 StartY=-10.4 StartZ=0 EndX=-82.8 EndY=-9.6 EndZ=0
    g1: LineSegment StartX=-82.8 StartY=-9.6 StartZ=0 EndX=-67.9 EndY=-9.6 EndZ=0
    g2: LineSegment StartX=-67.9 StartY=-9.6 StartZ=0 EndX=-67.9 EndY=6 EndZ=0
    g3: LineSegment StartX=-67.9 StartY=6 StartZ=0 EndX=-65.9 EndY=6 EndZ=0
    g4: LineSegment StartX=-65.9 StartY=6 StartZ=0 EndX=-65.9 EndY=-1.7 EndZ=0
    g5: LineSegment StartX=-65.9 StartY=-1.7 StartZ=0 EndX=-57.2 EndY=-1.7 EndZ=0
    g6: LineSegment StartX=-57.2 StartY=-1.7 StartZ=0 EndX=-57.2 EndY=-10.4 EndZ=0
    g7: LineSegment StartX=-57.2 StartY=-10.4 StartZ=0 EndX=-82.8 EndY=-10.4 EndZ=0
  constraints (22):
    c: Vertical(g0)
    c: Coincident(g1,g0)
    c: Horizontal(g1)
    c: Coincident(g2,g1)
    c: Vertical(g2)
    c: Coincident(g3,g2)
    c: Horizontal(g3)
    c: Coincident(g4,g3)
    c: Vertical(g4)
    c: Coincident(g5,g4)
    c: Horizontal(g5)
    c: Coincident(g6,g5)
    c: Vertical(g6)
    c: Coincident(g7,g6)
    c: Coincident(g7,g0)
    c: DistanceY(g0,g0) = 0.8
    c: DistanceY(g6,g6) = 8.7
    c: DistanceX(g1,g1) = 14.9
    c: DistanceX(g3,g3) = 2
    c: Coincident(g0,g-4)
    c: DistanceY(g2,g-6) = 0
    c: Coincident(g6,g-5)
FEATURE [Part::Extrusion] Extrude009  label="Extrude buco pompa"
  Base = -> Sketch013
  Dir = (0,-1,2e-16)
  DirMode = 2
  FaceMakerClass = Part::FaceMakerBullseye
  FaceMakerMode = 3
  LengthFwd = 13.2
  LengthRev = 0
  Solid = true
  Symmetric = true
FEATURE [Sketcher::SketchObject] Sketch014  label="buco frontale"
  ArcFitTolerance = 1e-06
  AttachmentSupport = -> [XZ_Plane]
  ExternalGeometry = -> [Sketch]
  FullyConstrained = true
  MakeInternals = false
  MapMode = 5
  Placement = pos=(0,0,0) rot=(1,0,0;1.5708rad)
  sketch-geometry (10):
    g0: LineSegment StartX=0 StartY=0 StartZ=0 EndX=0 EndY=24.671 EndZ=0
    g1: LineSegment StartX=0 StartY=24.671 StartZ=0 EndX=-4 EndY=24.671 EndZ=0
    g2: LineSegment StartX=-4 StartY=24.671 StartZ=0 EndX=-4 EndY=16 EndZ=0
    g3: LineSegment StartX=-4 StartY=16 StartZ=0 EndX=-2.4 EndY=16 EndZ=0
    g4: LineSegment StartX=-2.4 StartY=16 StartZ=0 EndX=-2.4 EndY=10 EndZ=0
    g5: LineSegment StartX=-2.4 StartY=10 StartZ=0 EndX=-12 EndY=10 EndZ=0
    g6: LineSegment StartX=-12 StartY=10 StartZ=0 EndX=-12 EndY=6 EndZ=0
    g7: LineSegment StartX=-12 StartY=6 StartZ=0 EndX=-2.4 EndY=6 EndZ=0
    g8: LineSegment StartX=-2.4 StartY=6 StartZ=0 EndX=-2.4 EndY=0 EndZ=0
    g9: LineSegment StartX=-2.4 StartY=0 StartZ=0 EndX=0 EndY=0 EndZ=0
  constraints (29):
    c: Vertical(g0)
    c: Coincident(g1,g0)
    c: Horizontal(g1)
    c: Coincident(g2,g1)
    c: Vertical(g2)
    c: Coincident(g3,g2)
    c: Horizontal(g3)
    c: Coincident(g4,g3)
    c: Vertical(g4)
    c: Coincident(g5,g4)
    c: Horizontal(g5)
    c: Coincident(g6,g5)
    c: Vertical(g6)
    c: Coincident(g7,g6)
    c: Coincident(g8,g7)
    c: Vertical(g8)
    c: Coincident(g9,g8)
    c: Coincident(g9,g0)
    c: Horizontal(g9)
    c: DistanceY(g0,g0) = 24.671
    c: Horizontal(g7)
    c: DistanceY(g6,g6) = 4
    c: DistanceY(g4,g4) = 6
    c: DistanceX(g9,g9) = 2.4
    c: Coincident(g0,g-1)
    c: DistanceY(g-3,g7) = 0
    c: DistanceX(g8,g4) = 0
    c: DistanceX(g-3,g1) = 0
    c: DistanceX(g6,g-3) = 8
FEATURE [Part::Extrusion] Extrude010  label="Extrude buco frontale"
  Base = -> Sketch014
  Dir = (0,-1,2e-16)
  DirMode = 2
  FaceMakerClass = Part::FaceMakerBullseye
  FaceMakerMode = 3
  LengthFwd = 11.2
  LengthRev = 0
  Solid = true
  Symmetric = true
FEATURE [Sketcher::SketchObject] Sketch015  label="guida rail"
  ArcFitTolerance = 1e-06
  AttachmentSupport = -> [XZ_Plane]
  ExternalGeometry = -> [Sketch]
  FullyConstrained = true
  MakeInternals = false
  MapMode = 5
  Placement = pos=(0,0,0) rot=(1,0,0;1.5708rad)
  sketch-geometry (4):
    g0: LineSegment StartX=-100.8 StartY=43.2 StartZ=0 EndX=-44.6 EndY=43.2 EndZ=0
    g1: LineSegment StartX=-44.6 StartY=43.2 StartZ=0 EndX=-44.6 EndY=41.2 EndZ=0
    g2: LineSegment StartX=-44.6 StartY=41.2 StartZ=0 EndX=-100.8 EndY=41.2 EndZ=0
    g3: LineSegment StartX=-100.8 StartY=41.2 StartZ=0 EndX=-100.8 EndY=43.2 EndZ=0
  constraints (9):
    c: Horizontal(g0)
    c: Coincident(g1,g0)
    c: Coincident(g2,g1)
    c: Coincident(g3,g2)
    c: Coincident(g3,g0)
    c: Vertical(g3)
    c: Coincident(g2,g-3)
    c: Coincident(g1,g-3)
    c: Coincident(g0,g-4)
FEATURE [Part::Extrusion] Extrude011  label="Extrude guida rail"
  Base = -> Sketch015
  Dir = (0,-1,2e-16)
  DirMode = 2
  FaceMakerClass = Part::FaceMakerBullseye
  FaceMakerMode = 3
  LengthFwd = 9
  LengthRev = 0
  Solid = true
  Symmetric = true
FEATURE [Sketcher::SketchObject] Sketch016  label="guide per coperture laterali"
  ArcFitTolerance = 1e-06
  AttachmentSupport = -> [XZ_Plane]
  ExternalGeometry = -> [Sketch]
  FullyConstrained = true
  MakeInternals = false
  MapMode = 5
  Placement = pos=(0,0,0) rot=(1,0,0;1.5708rad)
  sketch-geometry (14):
    g0: Circle CenterX=-5.6 CenterY=7.6 CenterZ=0 NormalX=0 NormalY=0 NormalZ=1 AngleXU=0 Radius=1.6
    g1: Circle CenterX=-5.6 CenterY=7.6 CenterZ=0 NormalX=0 NormalY=0 NormalZ=1 AngleXU=0 Radius=4
    g2: Circle CenterX=-5.6 CenterY=34.8 CenterZ=0 NormalX=0 NormalY=0 NormalZ=1 AngleXU=0 Radius=1.6
    g3: Circle CenterX=-5.6 CenterY=34.8 CenterZ=0 NormalX=0 NormalY=0 NormalZ=1 AngleXU=0 Radius=4
    g4: Circle CenterX=-184.08 CenterY=34.8 CenterZ=0 NormalX=0 NormalY=0 NormalZ=1 AngleXU=0 Radius=1.6
    g5: Circle CenterX=-184.08 CenterY=34.8 CenterZ=0 NormalX=0 NormalY=0 NormalZ=1 AngleXU=0 Radius=4
    g6: Circle CenterX=-179.305 CenterY=-76.8316 CenterZ=0 NormalX=0 NormalY=0 NormalZ=1 AngleXU=0 Radius=1.6
    g7: Circle CenterX=-179.305 CenterY=-76.8316 CenterZ=0 NormalX=0 NormalY=0 NormalZ=1 AngleXU=0 Radius=4
    g8: Circle CenterX=-213.443 CenterY=-76.8316 CenterZ=0 NormalX=0 NormalY=0 NormalZ=1 AngleXU=0 Radius=1.6
    g9: Circle CenterX=-213.443 CenterY=-76.8316 CenterZ=0 NormalX=0 NormalY=0 NormalZ=1 AngleXU=0 Radius=4
    g10: Circle CenterX=-78.51 CenterY=7.6 CenterZ=0 NormalX=0 NormalY=0 NormalZ=1 AngleXU=0 Radius=1.6
    g11: Circle CenterX=-78.51 CenterY=7.6 CenterZ=0 NormalX=0 NormalY=0 NormalZ=1 AngleXU=0 Radius=4
    g12: Circle CenterX=-78.51 CenterY=34.8 CenterZ=0 NormalX=0 NormalY=0 NormalZ=1 AngleXU=0 Radius=1.6
    g13: Circle CenterX=-78.51 CenterY=34.8 CenterZ=0 NormalX=0 NormalY=0 NormalZ=1 AngleXU=0 Radius=4
  constraints (35):
    c: Diameter(g0) = 3.2
    c: Diameter(g1) = 8
    c: Coincident(g0,g1)
    c: Diameter(g2) = 3.2
    c: Diameter(g3) = 8
    c: Coincident(g3,g2)
    c: Tangent(g2,g-7)
    c: Diameter(g4) = 3.2
    c: Diameter(g5) = 8
    c: Coincident(g5,g4)
    c: Tangent(g4,g-7)
    c: Tangent(g4,g-8)
    c: Diameter(g6) = 3.2
    c: Diameter(g7) = 8
    c: Coincident(g7,g6)
    c: Tangent(g6,g-9)
    c: Tangent(g6,g-10)
    c: Diameter(g8) = 3.2
    c: Diameter(g9) = 8
    c: Coincident(g9,g8)
    c: Tangent(g8,g-10)
    c: Tangent(g8,g-11)
    c: Diameter(g10) = 3.2
    c: Diameter(g11) = 8
    c: Diameter(g12) = 3.2
    c: Diameter(g13) = 8
    c: Coincident(g12,g13)
    c: Coincident(g10,g11)
    c: Tangent(g12,g-7)
    c: DistanceX(g12,g10) = 0
    c: Tangent(g2,g-6)
    c: Tangent(g0,g-6)
    c: Tangent(g0,g-3)
    c: Tangent(g10,g-3)
    c: Tangent(g10,g-4)
FEATURE [Part::Extrusion] Extrude012  label="extrude guide per coperture laterali"
  Base = -> Sketch016
  Dir = (0,-1,2e-16)
  DirMode = 2
  FaceMakerClass = Part::FaceMakerBullseye
  FaceMakerMode = 3
  LengthFwd = 25.2
  LengthRev = 0
  Solid = true
  Symmetric = true
FEATURE [Sketcher::SketchObject] Sketch017  label="supporto CAM"
  ArcFitTolerance = 1e-06
  AttachmentSupport = -> [XZ_Plane]
  ExternalGeometry = -> [Sketch]
  FullyConstrained = true
  MakeInternals = false
  MapMode = 5
  Placement = pos=(0,0,0) rot=(1,0,0;1.5708rad)
  sketch-geometry (6):
    g0: LineSegment StartX=-2.4 StartY=48 StartZ=0 EndX=-2.4 EndY=41.2 EndZ=0
    g1: LineSegment StartX=-2.4 StartY=48 StartZ=0 EndX=-34 EndY=48 EndZ=0
    g2: LineSegment StartX=-34 StartY=48 StartZ=0 EndX=-34 EndY=46.72 EndZ=0
    g3: LineSegment StartX=-34 StartY=46.72 StartZ=0 EndX=-36 EndY=46.72 EndZ=0
    g4: LineSegment StartX=-36 StartY=46.72 StartZ=0 EndX=-36 EndY=41.2 EndZ=0
    g5: LineSegment StartX=-36 StartY=41.2 StartZ=0 EndX=-2.4 EndY=41.2 EndZ=0
  constraints (15):
    c: Coincident(g1,g0)
    c: Horizontal(g1)
    c: Coincident(g2,g1)
    c: Vertical(g2)
    c: Coincident(g3,g2)
    c: Horizontal(g3)
    c: Coincident(g4,g3)
    c: Coincident(g5,g4)
    c: DistanceX(g1,g0) = 31.6
    c: Coincident(g5,g0)
    c: Vertical(g4)
    c: DistanceY(g2,g1) = 1.28
    c: Coincident(g0,g-3)
    c: Coincident(g0,g-3)
    c: Coincident(g4,g-4)
FEATURE [Part::Extrusion] Extrude013  label="Extrude supporto CAM"
  Base = -> Sketch017
  Dir = (0,-1,2e-16)
  DirMode = 2
  FaceMakerClass = Part::FaceMakerBullseye
  FaceMakerMode = 3
  LengthFwd = 17.8
  LengthRev = 0
  Solid = true
  Symmetric = true
FEATURE [Sketcher::SketchObject] Sketch018  label="Scavo CAM"
  ArcFitTolerance = 1e-06
  AttachmentSupport = -> [YZ_Plane]
  ExternalGeometry = -> [Sketch]
  FullyConstrained = true
  MakeInternals = false
  MapMode = 5
  Placement = pos=(0,0,0) rot=(0.57735,0.57735,0.57735;2.0944rad)
  sketch-geometry (4):
    g0: LineSegment StartX=-7.73 StartY=48 StartZ=0 EndX=7.73 EndY=48 EndZ=0
    g1: LineSegment [constr] StartX=1.07e-14 StartY=48 StartZ=0 EndX=0 EndY=43.5155 EndZ=0
    g2: ArcOfCircle CenterX=9e-15 CenterY=52.42 CenterZ=0 NormalX=0 NormalY=0 NormalZ=1 AngleXU=0 Radius=8.90445 StartAngle=3.66102 EndAngle=5.76376
    g3: Circle [constr] CenterX=9e-15 CenterY=52.42 CenterZ=0 NormalX=0 NormalY=0 NormalZ=1 AngleXU=0 Radius=8.9
  constraints (13):
    c: Horizontal(g0)
    c: DistanceY(g-3,g0) = 0
    c: DistanceX(g0,g0) = 15.46
    c: DistanceX(g0,g-3) = 7.73
    c: DistanceX(g-3) = 0
    c: Coincident(g1,g-3)
    c: PointOnObject(g1,g-2)
    c: Coincident(g2,g0)
    c: Coincident(g2,g0)
    c: PointOnObject(g1,g2)
    c: Diameter(g3) = 17.8
    c: DistanceY(g1,g3) = 4.42
    c: Coincident(g2,g3)
FEATURE [Part::Extrusion] Extrude014  label="Extrude Scavo CAM"
  Base = -> Sketch018
  Dir = (1,0,0)
  DirMode = 2
  FaceMakerClass = Part::FaceMakerBullseye
  FaceMakerMode = 3
  LengthFwd = -34
  LengthRev = 0
  Solid = true
  Symmetric = false
FEATURE [Sketcher::SketchObject] Sketch019  label="scavo rumble"
  ArcFitTolerance = 1e-06
  AttachmentSupport = -> [XZ_Plane]
  ExternalGeometry = -> [Sketch]
  FullyConstrained = true
  MakeInternals = false
  MapMode = 5
  Placement = pos=(0,0,0) rot=(1,0,0;1.5708rad)
  sketch-geometry (6):
    g0: LineSegment StartX=-163.771 StartY=-21.9058 StartZ=0 EndX=-158.636 EndY=-23.5745 EndZ=0
    g1: LineSegment StartX=-158.636 StartY=-23.5745 StartZ=0 EndX=-165.743 EndY=-45.4488 EndZ=0
    g2: LineSegment StartX=-165.743 StartY=-45.4488 StartZ=0 EndX=-170.879 EndY=-43.7801 EndZ=0
    g3: LineSegment StartX=-170.879 StartY=-43.7801 StartZ=0 EndX=-163.771 EndY=-21.9058 EndZ=0
    g4: LineSegment [constr] StartX=-145.51 StartY=22 StartZ=0 EndX=-160.157 EndY=-23.0801 EndZ=0
    g5: LineSegment [constr] StartX=-158.636 StartY=-23.5745 StartZ=0 EndX=-160.157 EndY=-23.0801 EndZ=0
  constraints (17):
    c: Coincident(g1,g0)
    c: Coincident(g2,g1)
    c: Coincident(g3,g2)
    c: Coincident(g3,g0)
    c: Parallel(g3,g-3)
    c: Parallel(g3,g1)
    c: Perpendicular(g3,g0)
    c: Perpendicular(g2,g3)
    c: Distance(g2,g0) = 23
    c: Parallel(g4,g-3)
    c: Distance(g4) = 47.4
    c: Coincident(g4,g-3)
    c: Parallel(g5,g0)
    c: Distance(g5) = 1.6
    c: Coincident(g5,g0)
    c: Distance(g5,g0) = 3.8
    c: Coincident(g5,g4)
FEATURE [Part::Extrusion] Extrude015  label="scavo rumble001"
  Base = -> Sketch019
  Dir = (0,-1,2e-16)
  DirMode = 2
  FaceMakerClass = Part::FaceMakerBullseye
  FaceMakerMode = 3
  LengthFwd = 21
  LengthRev = 0
  Solid = true
  Symmetric = true
FEATURE [Sketcher::SketchObject] Sketch020  label="fermo rumble"
  ArcFitTolerance = 1e-06
  AttachmentSupport = -> [XZ_Plane]
  ExternalGeometry = -> [Sketch019,Sketch]
  FullyConstrained = true
  MakeInternals = false
  MapMode = 5
  Placement = pos=(0,0,0) rot=(1,0,0;1.5708rad)
  sketch-geometry (16):
    g0: LineSegment [constr] StartX=-165.905 StartY=-40.7697 StartZ=0 EndX=-167.265 EndY=-44.9544 EndZ=0
    g1: LineSegment [constr] StartX=-167.265 StartY=-44.9544 StartZ=0 EndX=-165.743 EndY=-45.4488 EndZ=0
    g2: LineSegment StartX=-167.318 StartY=-37.9976 StartZ=0 EndX=-165.225 EndY=-38.6774 EndZ=0
    g3: LineSegment StartX=-165.225 StartY=-38.6774 StartZ=0 EndX=-165.905 EndY=-40.7697 EndZ=0
    g4: LineSegment StartX=-165.905 StartY=-40.7697 StartZ=0 EndX=-167.997 EndY=-40.0899 EndZ=0
    g5: LineSegment StartX=-167.997 StartY=-40.0899 StartZ=0 EndX=-167.318 EndY=-37.9976 EndZ=0
    g6: LineSegment StartX=-166.823 StartY=-36.4759 StartZ=0 EndX=-163.399 EndY=-37.5883 EndZ=0
    g7: LineSegment StartX=-163.399 StartY=-37.5883 StartZ=0 EndX=-165.006 EndY=-42.5338 EndZ=0
    g8: LineSegment StartX=-165.006 StartY=-42.5338 StartZ=0 EndX=-168.43 EndY=-41.4214 EndZ=0
    g9: LineSegment StartX=-169.457 StartY=-39.4053 StartZ=0 EndX=-168.839 EndY=-37.5031 EndZ=0
    g10: LineSegment [constr] StartX=-168.839 StartY=-37.5031 StartZ=0 EndX=-168.345 EndY=-35.9815 EndZ=0
    g11: LineSegment [constr] StartX=-168.345 StartY=-35.9815 StartZ=0 EndX=-166.823 EndY=-36.4759 EndZ=0
    g12: ArcOfCircle CenterX=-167.936 CenterY=-39.8997 CenterZ=0 NormalX=0 NormalY=0 NormalZ=1 AngleXU=0 Radius=1.6 StartAngle=2.82743 EndAngle=4.39823
    g13: GeomPoint [constr] X=-169.952 Y=-40.9269 Z=0
    g14: ArcOfCircle CenterX=-167.318 CenterY=-37.9976 CenterZ=0 NormalX=0 NormalY=0 NormalZ=1 AngleXU=0 Radius=1.6 StartAngle=1.25664 EndAngle=2.82743
    g15: GeomPoint [constr] X=-168.345 Y=-35.9815 Z=0
  constraints (42):
    c: Parallel(g0,g-4)
    c: Distance(g0) = 4.4
    c: Coincident(g1,g0)
    c: Perpendicular(g0,g1)
    c: Distance(g1) = 1.6
    c: Coincident(g1,g-5)
    c: Coincident(g3,g2)
    c: Coincident(g4,g3)
    c: Coincident(g5,g4)
    c: Coincident(g5,g2)
    c: Parallel(g3,g-4)
    c: Parallel(g3,g5)
    c: Perpendicular(g2,g3)
    c: Parallel(g4,g2)
    c: Distance(g2) = 2.2
    c: Distance(g3) = 2.2
    c: Coincident(g7,g6)
    c: Coincident(g8,g7)
    c: Parallel(g7,g-4)
    c: Parallel(g7,g9)
    c: Perpendicular(g6,g7)
    c: Parallel(g6,g8)
    c: Distance(g6,g15) = 5.2
    c: Distance(g7) = 5.2
    c: Coincident(g11,g10)
    c: Parallel(g10,g9)
    c: Parallel(g11,g6)
    c: Distance(g10) = 1.6
    c: Distance(g11) = 1.6
    c: Coincident(g10,g15)
    c: Distance(g11,g2) = 1.6
    c: Distance(g2,g10) = 1.6
    c: PointOnObject(g13,g8)
    c: PointOnObject(g13,g9)
    c: Tangent(g8,g12) = 1.5708
    c: Tangent(g9,g12) = 1.5708
    c: PointOnObject(g15,g9)
    c: Tangent(g6,g14) = 1.5708
    c: Tangent(g9,g14) = 1.5708
    c: Equal(g12,g14)
    c: Coincident(g6,g11)
    c: Coincident(g3,g0)
FEATURE [Part::Extrusion] Extrude016  label="Extrude fermo rumble"
  Base = -> Sketch020
  Dir = (0,-1,2e-16)
  DirMode = 2
  FaceMakerClass = Part::FaceMakerBullseye
  FaceMakerMode = 3
  LengthFwd = 25.2
  LengthRev = 0
  Solid = true
  Symmetric = true
FEATURE [Sketcher::SketchObject] Sketch021  label="perno fermo rumble001"
  ArcFitTolerance = 1e-06
  AttachmentSupport = -> [XZ_Plane001]
  FullyConstrained = true
  MakeInternals = false
  MapMode = 5
  Placement = pos=(0,0,0) rot=(1,0,0;1.5708rad)
  sketch-geometry (16):
    g0: LineSegment StartX=0 StartY=0.45 StartZ=0 EndX=0 EndY=1.55 EndZ=0
    g1: LineSegment StartX=0.45 StartY=2 StartZ=0 EndX=1.55 EndY=2 EndZ=0
    g2: LineSegment StartX=2 StartY=1.55 StartZ=0 EndX=2 EndY=0.45 EndZ=0
    g3: LineSegment StartX=1.55 StartY=0 StartZ=0 EndX=0.45 EndY=0 EndZ=0
    g4: ArcOfCircle [constr] CenterX=0.45 CenterY=1.55 CenterZ=0 NormalX=0 NormalY=0 NormalZ=1 AngleXU=0 Radius=0.45 StartAngle=1.5708 EndAngle=3.14159
    g5: GeomPoint [constr] X=0 Y=2 Z=0
    g6: LineSegment StartX=0.45 StartY=2 StartZ=0 EndX=0 EndY=1.55 EndZ=0
    g7: ArcOfCircle [constr] CenterX=1.55 CenterY=1.55 CenterZ=0 NormalX=0 NormalY=0 NormalZ=1 AngleXU=0 Radius=0.45 StartAngle=0 EndAngle=1.5708
    g8: GeomPoint [constr] X=2 Y=2 Z=0
    g9: LineSegment StartX=2 StartY=1.55 StartZ=0 EndX=1.55 EndY=2 EndZ=0
    g10: ArcOfCircle [constr] CenterX=1.55 CenterY=0.45 CenterZ=0 NormalX=0 NormalY=0 NormalZ=1 AngleXU=0 Radius=0.45 StartAngle=4.71239 EndAngle=6.28319
    g11: GeomPoint [constr] X=2 Y=0 Z=0
    g12: LineSegment StartX=1.55 StartY=0 StartZ=0 EndX=2 EndY=0.45 EndZ=0
    g13: ArcOfCircle [constr] CenterX=0.45 CenterY=0.45 CenterZ=0 NormalX=0 NormalY=0 NormalZ=1 AngleXU=0 Radius=0.45 StartAngle=3.14159 EndAngle=4.71239
    g14: GeomPoint [constr] X=0 Y=0 Z=0
    g15: LineSegment StartX=0 StartY=0.45 StartZ=0 EndX=0.45 EndY=0 EndZ=0
  constraints (35):
    c: Coincident(g14,g-1)
    c: PointOnObject(g5,g-2)
    c: Horizontal(g1)
    c: Vertical(g2)
    c: Horizontal(g3)
    c: DistanceX(g5,g8) = 2
    c: DistanceY(g11,g8) = 2
    c: PointOnObject(g5,g0)
    c: PointOnObject(g5,g1)
    c: Tangent(g0,g4) = 1.5708
    c: Tangent(g1,g4) = 1.5708
    c: Coincident(g6,g0)
    c: Coincident(g6,g1)
    c: PointOnObject(g8,g2)
    c: PointOnObject(g8,g1)
    c: Tangent(g2,g7) = 1.5708
    c: Tangent(g1,g7) = 1.5708
    c: Coincident(g9,g2)
    c: Coincident(g9,g1)
    c: PointOnObject(g11,g2)
    c: PointOnObject(g11,g3)
    c: Tangent(g2,g10) = 1.5708
    c: Tangent(g3,g10) = 1.5708
    c: Coincident(g12,g2)
    c: Coincident(g12,g3)
    c: PointOnObject(g14,g0)
    c: PointOnObject(g14,g3)
    c: Tangent(g0,g13) = 1.5708
    c: Tangent(g3,g13) = 1.5708
    c: Coincident(g15,g0)
    c: Coincident(g15,g3)
    c: Equal(g6,g9)
    c: Equal(g9,g12)
    c: Equal(g12,g15)
    c: DistanceX(g14,g3) = 0.45
FEATURE [Sketcher::SketchObject] Sketch022  label="fori per M3x5(OD)x6(L)"
  ArcFitTolerance = 1e-06
  AttachmentSupport = -> [XZ_Plane]
  ExternalGeometry = -> [Sketch016]
  FullyConstrained = true
  MakeInternals = false
  MapMode = 5
  Placement = pos=(0,0,0) rot=(1,0,0;1.5708rad)
  sketch-geometry (7):
    g0: Circle CenterX=-5.6 CenterY=34.8 CenterZ=0 NormalX=0 NormalY=0 NormalZ=1 AngleXU=0 Radius=2.5
    g1: Circle CenterX=-5.6 CenterY=7.6 CenterZ=0 NormalX=0 NormalY=0 NormalZ=1 AngleXU=0 Radius=2.5
    g2: Circle CenterX=-78.51 CenterY=34.8 CenterZ=0 NormalX=0 NormalY=0 NormalZ=1 AngleXU=0 Radius=2.5
    g3: Circle CenterX=-78.51 CenterY=7.6 CenterZ=0 NormalX=0 NormalY=0 NormalZ=1 AngleXU=0 Radius=2.5
    g4: Circle CenterX=-184.08 CenterY=34.8 CenterZ=0 NormalX=0 NormalY=0 NormalZ=1 AngleXU=0 Radius=2.5
    g5: Circle CenterX=-179.305 CenterY=-76.8316 CenterZ=0 NormalX=0 NormalY=0 NormalZ=1 AngleXU=0 Radius=2.5
    g6: Circle CenterX=-213.443 CenterY=-76.8316 CenterZ=0 NormalX=0 NormalY=0 NormalZ=1 AngleXU=0 Radius=2.5
  constraints (14):
    c: Diameter(g0) = 5
    c: Diameter(g1) = 5
    c: Diameter(g2) = 5
    c: Diameter(g3) = 5
    c: Diameter(g4) = 5
    c: Diameter(g5) = 5
    c: Diameter(g6) = 5
    c: Coincident(g0,g-8)
    c: Coincident(g1,g-9)
    c: Coincident(g2,g-6)
    c: Coincident(g3,g-7)
    c: Coincident(g4,g-5)
    c: Coincident(g5,g-4)
    c: Coincident(g6,g-3)
FEATURE [Part::Extrusion] Extrude018  label="Extrude fori M3x5x6 - dx"
  Base = -> Sketch022
  Dir = (0,-1,2e-16)
  DirMode = 2
  FaceMakerClass = Part::FaceMakerBullseye
  FaceMakerMode = 3
  LengthFwd = 6.2
  LengthRev = 0
  Placement = pos=(0,-9.5,0) rot=(0,0,1;0rad)
  Solid = true
  Symmetric = true
FEATURE [Part::Extrusion] Extrude019  label="Extrude fori M3x5x6 - sx"
  Base = -> Sketch022
  Dir = (0,-1,2e-16)
  DirMode = 2
  FaceMakerClass = Part::FaceMakerBullseye
  FaceMakerMode = 3
  LengthFwd = 6.2
  LengthRev = 0
  Placement = pos=(0,9.5,0) rot=(0,0,1;0rad)
  Solid = true
  Symmetric = true
FEATURE [Sketcher::SketchObject] Sketch023  label="foro anteriore M3x5x6"
  ArcFitTolerance = 1e-06
  AttachmentSupport = -> [YZ_Plane]
  FullyConstrained = true
  MakeInternals = false
  MapMode = 5
  Placement = pos=(0,0,0) rot=(0.57735,0.57735,0.57735;2.0944rad)
  sketch-geometry (2):
    g0: LineSegment [constr] StartX=0 StartY=0 StartZ=0 EndX=0 EndY=38.6 EndZ=0
    g1: Circle CenterX=0 CenterY=38.6 CenterZ=0 NormalX=0 NormalY=0 NormalZ=1 AngleXU=0 Radius=2.5
  constraints (5):
    c: Coincident(g0,g-1)
    c: PointOnObject(g0,g-2)
    c: DistanceY(g0,g0) = 38.6
    c: Diameter(g1) = 5
    c: Coincident(g1,g0)
FEATURE [Part::Extrusion] Extrude020  label="Extrude foro anteriore M3x5x6"
  Base = -> Sketch023
  Dir = (1,0,0)
  DirMode = 2
  FaceMakerClass = Part::FaceMakerBullseye
  FaceMakerMode = 3
  LengthFwd = -6.2
  LengthRev = 0
  Solid = true
  Symmetric = false
FEATURE [Sketcher::SketchObject] Sketch024  label="fori per viti frontale"
  ArcFitTolerance = 1e-06
  AttachmentSupport = -> [YZ_Plane]
  FullyConstrained = true
  MakeInternals = false
  MapMode = 5
  Placement = pos=(0,0,0) rot=(0.57735,0.57735,0.57735;2.0944rad)
  sketch-geometry (9):
    g0: LineSegment [constr] StartX=-10.3 StartY=30.721 StartZ=0 EndX=10.3 EndY=30.721 EndZ=0
    g1: LineSegment [constr] StartX=10.3 StartY=30.721 StartZ=0 EndX=10.3 EndY=10.121 EndZ=0
    g2: LineSegment [constr] StartX=10.3 StartY=10.121 StartZ=0 EndX=-10.3 EndY=10.121 EndZ=0
    g3: LineSegment [constr] StartX=-10.3 StartY=10.121 StartZ=0 EndX=-10.3 EndY=30.721 EndZ=0
    g4: LineSegment [constr] StartX=0 StartY=0 StartZ=0 EndX=0 EndY=10.121 EndZ=0
    g5: Circle CenterX=-10.3 CenterY=30.721 CenterZ=0 NormalX=0 NormalY=0 NormalZ=1 AngleXU=0 Radius=2
    g6: Circle CenterX=10.3 CenterY=30.721 CenterZ=0 NormalX=0 NormalY=0 NormalZ=1 AngleXU=0 Radius=2
    g7: Circle CenterX=-10.3 CenterY=10.121 CenterZ=0 NormalX=0 NormalY=0 NormalZ=1 AngleXU=0 Radius=2
    g8: Circle CenterX=10.3 CenterY=10.121 CenterZ=0 NormalX=0 NormalY=0 NormalZ=1 AngleXU=0 Radius=2
  constraints (22):
    c: Horizontal(g0)
    c: Coincident(g1,g0)
    c: Vertical(g1)
    c: Coincident(g2,g1)
    c: Horizontal(g2)
    c: Coincident(g3,g2)
    c: Coincident(g3,g0)
    c: Vertical(g3)
    c: DistanceX(g0,g0) = 20.6
    c: DistanceY(g3,g3) = 20.6
    c: Coincident(g4,g-1)
    c: PointOnObject(g4,g-2)
    c: DistanceY(g4,g4) = 10.121
    c: Symmetric(g2,g2,g4)
    c: Diameter(g5) = 4
    c: Diameter(g6) = 4
    c: Diameter(g7) = 4
    c: Diameter(g8) = 4
    c: Coincident(g5,g0)
    c: Coincident(g6,g0)
    c: Coincident(g7,g2)
    c: Coincident(g8,g1)
FEATURE [Part::Extrusion] Extrude021  label="Extrude fori per viti frontale"
  Base = -> Sketch024
  Dir = (1,0,0)
  DirMode = 2
  FaceMakerClass = Part::FaceMakerBullseye
  FaceMakerMode = 3
  LengthFwd = -2.4
  LengthRev = 0
  Solid = true
  Symmetric = false
FEATURE [Sketcher::SketchObject] Sketch025  label="foro per filo CAM"
  ArcFitTolerance = 1e-06
  AttachmentSupport = -> [XZ_Plane]
  ExternalGeometry = -> [Sketch]
  FullyConstrained = true
  MakeInternals = false
  MapMode = 5
  Placement = pos=(0,0,0) rot=(1,0,0;1.5708rad)
  sketch-geometry (4):
    g0: LineSegment StartX=-44.6 StartY=41.2 StartZ=0 EndX=-44.6 EndY=36.4 EndZ=0
    g1: LineSegment StartX=-44.6 StartY=36.4 StartZ=0 EndX=-54.6 EndY=36.4 EndZ=0
    g2: LineSegment StartX=-54.6 StartY=36.4 StartZ=0 EndX=-50.4 EndY=41.2 EndZ=0
    g3: LineSegment StartX=-50.4 StartY=41.2 StartZ=0 EndX=-44.6 EndY=41.2 EndZ=0
  constraints (11):
    c: Vertical(g0)
    c: Coincident(g1,g0)
    c: Horizontal(g1)
    c: Coincident(g2,g1)
    c: Coincident(g3,g2)
    c: Coincident(g3,g0)
    c: Horizontal(g3)
    c: Coincident(g0,g-3)
    c: DistanceY(g0,g-4) = 0
    c: DistanceX(g3,g3) = 5.8
    c: DistanceX(g1,g1) = 10
FEATURE [Part::Extrusion] Extrude022  label="Extrude foro per filo CAM dx"
  Base = -> Sketch025
  Dir = (0,-1,2e-16)
  DirMode = 2
  FaceMakerClass = Part::FaceMakerBullseye
  FaceMakerMode = 3
  LengthFwd = 4.9
  LengthRev = 0
  Placement = pos=(0,6.95,0) rot=(0,0,1;0rad)
  Solid = true
  Symmetric = true
FEATURE [Part::Extrusion] Extrude023  label="Extrude foro per filo CAM sx"
  Base = -> Sketch025
  Dir = (0,-1,2e-16)
  DirMode = 2
  FaceMakerClass = Part::FaceMakerBullseye
  FaceMakerMode = 3
  LengthFwd = 4.9
  LengthRev = 0
  Placement = pos=(0,-6.95,0) rot=(0,0,1;0rad)
  Solid = true
  Symmetric = true
FEATURE [Sketcher::SketchObject] Sketch026  label="foro sotto anteriore M3x5x6"
  ArcFitTolerance = 1e-06
  AttachmentSupport = -> [XY_Plane]
  FullyConstrained = true
  MakeInternals = false
  MapMode = 5
  sketch-geometry (2):
    g0: LineSegment [constr] StartX=0 StartY=0 StartZ=0 EndX=-16.5 EndY=0 EndZ=0
    g1: Circle CenterX=-16.5 CenterY=0 CenterZ=0 NormalX=0 NormalY=0 NormalZ=1 AngleXU=0 Radius=2.5
  constraints (5):
    c: Distance(g0) = 16.5
    c: Coincident(g0,g-1)
    c: PointOnObject(g0,g-1)
    c: Diameter(g1) = 5
    c: Coincident(g0,g1)
FEATURE [Sketcher::SketchObject] Sketch027  label="foro sotto posteriore M3x5x6"
  ArcFitTolerance = 1e-06
  AttachmentSupport = -> [XY_Plane]
  ExternalGeometry = -> [Sketch]
  FullyConstrained = true
  MakeInternals = false
  MapMode = 5
  sketch-geometry (2):
    g0: LineSegment [constr] StartX=-82.8 StartY=2e-16 StartZ=0 EndX=-71.3 EndY=2e-16 EndZ=0
    g1: Circle CenterX=-71.3 CenterY=2e-16 CenterZ=0 NormalX=0 NormalY=0 NormalZ=1 AngleXU=0 Radius=2.5
  constraints (5):
    c: Distance(g0) = 11.5
    c: Coincident(g0,g-3)
    c: PointOnObject(g0,g-3)
    c: Diameter(g1) = 5
    c: Coincident(g1,g0)
FEATURE [Sketcher::SketchObject] Sketch029  label="fori sotto impugnatura"
  ArcFitTolerance = 1e-06
  AttachmentSupport = -> [XY_Plane]
  ExternalGeometry = -> [Sketch]
  FullyConstrained = true
  MakeInternals = false
  MapMode = 5
  sketch-geometry (15):
    g0: LineSegment [constr] StartX=-175.232 StartY=-1.83e-14 StartZ=0 EndX=-191.232 EndY=0 EndZ=0
    g1: Circle CenterX=-191.232 CenterY=0 CenterZ=0 NormalX=0 NormalY=0 NormalZ=1 AngleXU=0 Radius=3.95
    g2: LineSegment [constr] StartX=-175.232 StartY=-1.83e-14 StartZ=0 EndX=-204.275 EndY=0 EndZ=0
    g3: LineSegment StartX=-204.275 StartY=3.525 StartZ=0 EndX=-204.275 EndY=-3.525 EndZ=0
    g4: LineSegment StartX=-205.4 StartY=-4.65 StartZ=0 EndX=-206.65 EndY=-4.65 EndZ=0
    g5: LineSegment StartX=-207.775 StartY=-3.525 StartZ=0 EndX=-207.775 EndY=3.525 EndZ=0
    g6: LineSegment StartX=-206.65 StartY=4.65 StartZ=0 EndX=-205.4 EndY=4.65 EndZ=0
    g7: ArcOfCircle CenterX=-206.65 CenterY=3.525 CenterZ=0 NormalX=0 NormalY=0 NormalZ=1 AngleXU=0 Radius=1.125 StartAngle=1.5708 EndAngle=3.14159
    g8: GeomPoint [constr] X=-207.775 Y=4.65 Z=0
    g9: ArcOfCircle CenterX=-205.4 CenterY=3.525 CenterZ=0 NormalX=0 NormalY=0 NormalZ=1 AngleXU=0 Radius=1.125 StartAngle=0 EndAngle=1.5708
    g10: GeomPoint [constr] X=-204.275 Y=4.65 Z=0
    g11: ArcOfCircle CenterX=-205.4 CenterY=-3.525 CenterZ=0 NormalX=0 NormalY=0 NormalZ=1 AngleXU=0 Radius=1.125 StartAngle=4.71239 EndAngle=6.28319
    g12: GeomPoint [constr] X=-204.275 Y=-4.65 Z=0
    g13: ArcOfCircle CenterX=-206.65 CenterY=-3.525 CenterZ=0 NormalX=0 NormalY=0 NormalZ=1 AngleXU=0 Radius=1.125 StartAngle=3.14159 EndAngle=4.71239
    g14: GeomPoint [constr] X=-207.775 Y=-4.65 Z=0
  constraints (35):
    c: Distance(g0) = 16
    c: Coincident(g0,g-3)
    c: PointOnObject(g0,g-1)
    c: Diameter(g1) = 7.9
    c: Coincident(g1,g0)
    c: Coincident(g2,g0)
    c: PointOnObject(g2,g-1)
    c: Vertical(g3)
    c: Horizontal(g4)
    c: Vertical(g5)
    c: Horizontal(g6)
    c: DistanceY(g12,g10) = 9.3
    c: DistanceX(g8,g10) = 3.5
    c: Symmetric(g10,g12,g2)
    c: PointOnObject(g8,g5)
    c: PointOnObject(g8,g6)
    c: Tangent(g5,g7) = 1.5708
    c: Tangent(g6,g7) = 1.5708
    c: PointOnObject(g10,g3)
    c: PointOnObject(g10,g6)
    c: Tangent(g3,g9) = 1.5708
    c: Tangent(g6,g9) = 1.5708
    c: PointOnObject(g12,g3)
    c: PointOnObject(g12,g4)
    c: Tangent(g3,g11) = 1.5708
    c: Tangent(g4,g11) = 1.5708
    c: PointOnObject(g14,g4)
    c: PointOnObject(g14,g5)
    c: Tangent(g4,g13) = 1.5708
    c: Tangent(g5,g13) = 1.5708
    c: Equal(g7,g9)
    c: Equal(g9,g11)
    c: Equal(g11,g13)
    c: DistanceX(g6,g6) = 1.25
    c: DistanceX(g-5,g5) = 6.8
FEATURE [Sketcher::SketchObject] Sketch030  label="fori superiori per solenoide e oled"
  ArcFitTolerance = 1e-06
  AttachmentSupport = -> [XY_Plane]
  ExternalGeometry = -> [Sketch]
  FullyConstrained = true
  MakeInternals = false
  MapMode = 5
  sketch-geometry (33):
    g0: LineSegment [constr] StartX=-181.6 StartY=1.12e-14 StartZ=0 EndX=-169.91 EndY=0 EndZ=0
    g1: LineSegment [constr] StartX=-169.91 StartY=0 StartZ=0 EndX=-169.91 EndY=-2.6 EndZ=0
    g2: LineSegment [constr] StartX=-169.91 StartY=0 StartZ=0 EndX=-169.91 EndY=2.6 EndZ=0
    g3: LineSegment StartX=-169.91 StartY=4.975 StartZ=0 EndX=-169.91 EndY=8.225 EndZ=0
    g4: LineSegment StartX=-167.535 StartY=10.6 StartZ=0 EndX=-167.285 EndY=10.6 EndZ=0
    g5: LineSegment StartX=-164.91 StartY=8.225 StartZ=0 EndX=-164.91 EndY=4.975 EndZ=0
    g6: LineSegment StartX=-167.285 StartY=2.6 StartZ=0 EndX=-167.535 EndY=2.6 EndZ=0
    g7: LineSegment StartX=-169.91 StartY=-4.975 StartZ=0 EndX=-169.91 EndY=-8.225 EndZ=0
    g8: LineSegment StartX=-167.535 StartY=-10.6 StartZ=0 EndX=-167.285 EndY=-10.6 EndZ=0
    g9: LineSegment StartX=-164.91 StartY=-8.225 StartZ=0 EndX=-164.91 EndY=-4.975 EndZ=0
    g10: LineSegment StartX=-167.285 StartY=-2.6 StartZ=0 EndX=-167.535 EndY=-2.6 EndZ=0
    g11: ArcOfCircle CenterX=-167.535 CenterY=8.225 CenterZ=0 NormalX=0 NormalY=0 NormalZ=1 AngleXU=0 Radius=2.375 StartAngle=1.5708 EndAngle=3.14159
    g12: GeomPoint [constr] X=-169.91 Y=10.6 Z=0
    g13: ArcOfCircle CenterX=-167.285 CenterY=8.225 CenterZ=0 NormalX=0 NormalY=0 NormalZ=1 AngleXU=0 Radius=2.375 StartAngle=0 EndAngle=1.5708
    g14: GeomPoint [constr] X=-164.91 Y=10.6 Z=0
    g15: ArcOfCircle CenterX=-167.285 CenterY=4.975 CenterZ=0 NormalX=0 NormalY=0 NormalZ=1 AngleXU=0 Radius=2.375 StartAngle=4.71239 EndAngle=6.28319
    g16: GeomPoint [constr] X=-164.91 Y=2.6 Z=0
    g17: ArcOfCircle CenterX=-167.535 CenterY=4.975 CenterZ=0 NormalX=0 NormalY=0 NormalZ=1 AngleXU=0 Radius=2.375 StartAngle=3.14159 EndAngle=4.71239
    g18: GeomPoint [constr] X=-169.91 Y=2.6 Z=0
    g19: ArcOfCircle CenterX=-167.535 CenterY=-4.975 CenterZ=0 NormalX=0 NormalY=0 NormalZ=1 AngleXU=0 Radius=2.375 StartAngle=1.5708 EndAngle=3.14159
    g20: GeomPoint [constr] X=-169.91 Y=-2.6 Z=0
    g21: ArcOfCircle CenterX=-167.285 CenterY=-4.975 CenterZ=0 NormalX=0 NormalY=0 NormalZ=1 AngleXU=0 Radius=2.375 StartAngle=0 EndAngle=1.5708
    g22: GeomPoint [constr] X=-164.91 Y=-2.6 Z=0
    g23: ArcOfCircle CenterX=-167.285 CenterY=-8.225 CenterZ=0 NormalX=0 NormalY=0 NormalZ=1 AngleXU=0 Radius=2.375 StartAngle=4.71239 EndAngle=6.28319
    g24: GeomPoint [constr] X=-164.91 Y=-10.6 Z=0
    g25: ArcOfCircle CenterX=-167.535 CenterY=-8.225 CenterZ=0 NormalX=0 NormalY=0 NormalZ=1 AngleXU=0 Radius=2.375 StartAngle=3.14159 EndAngle=4.71239
    g26: GeomPoint [constr] X=-169.91 Y=-10.6 Z=0
    g27: LineSegment [constr] StartX=-181.6 StartY=1.12e-14 StartZ=0 EndX=-152.209 EndY=0 EndZ=0
    g28: LineSegment [constr] StartX=-181.6 StartY=1.12e-14 StartZ=0 EndX=-130.41 EndY=0 EndZ=0
    g29: LineSegment [constr] StartX=-152.209 StartY=0 StartZ=0 EndX=-152.209 EndY=6.95 EndZ=0
    g30: LineSegment [constr] StartX=-130.41 StartY=0 StartZ=0 EndX=-130.41 EndY=-6.95 EndZ=0
    g31: Circle CenterX=-152.209 CenterY=6.95 CenterZ=0 NormalX=0 NormalY=0 NormalZ=1 AngleXU=0 Radius=2.1
    g32: Circle CenterX=-130.41 CenterY=-6.95 CenterZ=0 NormalX=0 NormalY=0 NormalZ=1 AngleXU=0 Radius=2.1
  constraints (79):
    c: Distance(g0) = 11.69
    c: PointOnObject(g0,g-1)
    c: Coincident(g-4,g0)
    c: Distance(g1) = 2.6
    c: Coincident(g1,g0)
    c: Vertical(g1)
    c: Distance(g2) = 2.6
    c: Coincident(g2,g0)
    c: Vertical(g2)
    c: Distance(g18,g12) = 8
    c: Coincident(g18,g2)
    c: Vertical(g3)
    c: Distance(g14,g12) = 5
    c: Horizontal(g4)
    c: Distance(g16,g14) = 8
    c: Vertical(g5)
    c: Distance(g26,g20) = 8
    c: Coincident(g20,g1)
    c: Vertical(g7)
    c: Distance(g26,g24) = 5
    c: Horizontal(g8)
    c: Distance(g24,g22) = 8
    c: Vertical(g9)
    c: PointOnObject(g12,g3)
    c: PointOnObject(g12,g4)
    c: Tangent(g3,g11) = 1.5708
    c: Tangent(g4,g11) = 1.5708
    c: PointOnObject(g14,g5)
    c: PointOnObject(g14,g4)
    c: Tangent(g5,g13) = 1.5708
    c: Tangent(g4,g13) = 1.5708
    c: PointOnObject(g16,g5)
    c: PointOnObject(g16,g6)
    c: Tangent(g5,g15) = 1.5708
    c: Tangent(g6,g15) = 1.5708
    c: PointOnObject(g18,g3)
    c: PointOnObject(g18,g6)
    c: Tangent(g3,g17) = 1.5708
    c: Tangent(g6,g17) = 1.5708
    c: Equal(g11,g13)
    c: Equal(g13,g15)
    c: Equal(g15,g17)
    c: DistanceX(g4,g4) = 0.25
    c: PointOnObject(g20,g7)
    c: PointOnObject(g20,g10)
    c: Tangent(g7,g19) = -1.5708
    c: Tangent(g10,g19) = -1.5708
    c: PointOnObject(g22,g9)
    c: PointOnObject(g22,g10)
    c: Tangent(g9,g21) = -1.5708
    c: Tangent(g10,g21) = -1.5708
    c: PointOnObject(g24,g9)
    c: PointOnObject(g24,g8)
    c: Tangent(g9,g23) = -1.5708
    c: Tangent(g8,g23) = -1.5708
    c: PointOnObject(g26,g8)
    c: PointOnObject(g26,g7)
    c: Tangent(g8,g25) = -1.5708
    c: Tangent(g7,g25) = -1.5708
    c: Equal(g19,g21)
    c: Equal(g21,g23)
    c: Equal(g23,g25)
    c: DistanceX(g10,g10) = 0.25
    c: Distance(g27) = 29.391
    c: Coincident(g27,g0)
    c: PointOnObject(g27,g-1)
    c: Distance(g28) = 51.19
    c: Coincident(g28,g0)
    c: PointOnObject(g28,g-1)
    c: Distance(g29) = 6.95
    c: Coincident(g29,g27)
    c: Vertical(g29)
    c: Distance(g30) = 6.95
    c: Coincident(g30,g28)
    c: Vertical(g30)
    c: Diameter(g31) = 4.2
    c: Diameter(g32) = 4.2
    c: Coincident(g32,g30)
    c: Coincident(g31,g29)
FEATURE [Sketcher::SketchObject] Sketch031  label="fori inferiori switch pompa"
  ArcFitTolerance = 1e-06
  AttachmentSupport = -> [XY_Plane]
  ExternalGeometry = -> [Sketch]
  FullyConstrained = true
  MakeInternals = false
  MapMode = 5
  sketch-geometry (4):
    g0: LineSegment [constr] StartX=-57.2 StartY=1.9e-15 StartZ=0 EndX=-62.45 EndY=1.9e-15 EndZ=0
    g1: LineSegment [constr] StartX=-62.45 StartY=3.25 StartZ=0 EndX=-62.45 EndY=-3.25 EndZ=0
    g2: Circle CenterX=-62.45 CenterY=3.25 CenterZ=0 NormalX=0 NormalY=0 NormalZ=1 AngleXU=0 Radius=1.6
    g3: Circle CenterX=-62.45 CenterY=-3.25 CenterZ=0 NormalX=0 NormalY=0 NormalZ=1 AngleXU=0 Radius=1.6
  constraints (10):
    c: Distance(g0) = 5.25
    c: Coincident(g0,g-3)
    c: PointOnObject(g0,g-3)
    c: Vertical(g1)
    c: DistanceY(g1,g1) = 6.5
    c: Symmetric(g1,g1,g0)
    c: Diameter(g2) = 3.2
    c: Diameter(g3) = 3.2
    c: Coincident(g2,g1)
    c: Coincident(g3,g1)
FEATURE [Sketcher::SketchObject] Sketch032  label="spazio per PILA 18650"
  ArcFitTolerance = 1e-06
  AttachmentSupport = -> [XY_Plane]
  ExternalGeometry = -> [Sketch]
  FullyConstrained = true
  MakeInternals = false
  MapMode = 5
  sketch-geometry (2):
    g0: LineSegment [constr] StartX=-178.142 StartY=-1.74e-14 StartZ=0 EndX=-191.142 EndY=-1.83e-14 EndZ=0
    g1: Circle CenterX=-191.142 CenterY=-1.83e-14 CenterZ=0 NormalX=0 NormalY=0 NormalZ=1 AngleXU=0 Radius=10.5
  constraints (5):
    c: Distance(g0) = 13
    c: Coincident(g0,g-3)
    c: PointOnObject(g0,g-4)
    c: Diameter(g1) = 21
    c: Coincident(g1,g0)
FEATURE [Part::Extrusion] Extrude030  label="Extrude spazio per PILA 18650"
  Base = -> Sketch032
  Dir = (0,0,1)
  DirLink = -> Sketch [Edge45]
  DirMode = 2
  FaceMakerClass = Part::FaceMakerBullseye
  FaceMakerMode = 3
  LengthFwd = 76
  LengthRev = 0
  Placement = pos=(6,0,-72) rot=(0,0,1;0rad)
  Solid = true
  Symmetric = false
FEATURE [Sketcher::SketchObject] Sketch033  label="fermo per scheda micro"
  ArcFitTolerance = 1e-06
  AttachmentSupport = -> [XZ_Plane]
  ExternalGeometry = -> [Sketch]
  FullyConstrained = true
  MakeInternals = false
  MapMode = 5
  Placement = pos=(0,0,0) rot=(1,0,0;1.5708rad)
  sketch-geometry (12):
    g0: LineSegment StartX=-11.6 StartY=6 StartZ=0 EndX=-4 EndY=6 EndZ=0
    g1: LineSegment StartX=-4 StartY=6 StartZ=0 EndX=-4 EndY=36.4 EndZ=0
    g2: LineSegment StartX=-4 StartY=36.4 StartZ=0 EndX=-11.6 EndY=36.4 EndZ=0
    g3: LineSegment StartX=-11.6 StartY=36.4 StartZ=0 EndX=-11.6 EndY=6 EndZ=0
    g4: LineSegment StartX=-80.11 StartY=11.6 StartZ=0 EndX=-70.51 EndY=11.6 EndZ=0
    g5: LineSegment StartX=-70.51 StartY=11.6 StartZ=0 EndX=-70.51 EndY=6 EndZ=0
    g6: LineSegment StartX=-70.51 StartY=6 StartZ=0 EndX=-80.11 EndY=6 EndZ=0
    g7: LineSegment StartX=-80.11 StartY=6 StartZ=0 EndX=-80.11 EndY=11.6 EndZ=0
    g8: LineSegment StartX=-78.51 StartY=36.4 StartZ=0 EndX=-70.51 EndY=36.4 EndZ=0
    g9: LineSegment StartX=-70.51 StartY=36.4 StartZ=0 EndX=-70.51 EndY=30.8 EndZ=0
    g10: LineSegment StartX=-70.51 StartY=30.8 StartZ=0 EndX=-78.51 EndY=30.8 EndZ=0
    g11: LineSegment StartX=-78.51 StartY=30.8 StartZ=0 EndX=-78.51 EndY=36.4 EndZ=0
  constraints (33):
    c: Horizontal(g0)
    c: Coincident(g1,g0)
    c: Coincident(g2,g1)
    c: Horizontal(g2)
    c: Coincident(g3,g2)
    c: Coincident(g3,g0)
    c: Vertical(g3)
    c: DistanceX(g2,g2) = 7.6
    c: Coincident(g1,g-3)
    c: Coincident(g0,g-3)
    c: Horizontal(g4)
    c: Coincident(g5,g4)
    c: Vertical(g5)
    c: Coincident(g6,g5)
    c: Horizontal(g6)
    c: Coincident(g7,g6)
    c: Coincident(g7,g4)
    c: Vertical(g7)
    c: DistanceY(g5,g5) = 5.6
    c: DistanceX(g4,g4) = 9.6
    c: Coincident(g9,g8)
    c: Vertical(g9)
    c: Coincident(g10,g9)
    c: Horizontal(g10)
    c: Coincident(g11,g10)
    c: Coincident(g11,g8)
    c: Vertical(g11)
    c: DistanceY(g9,g9) = 5.6
    c: DistanceX(g10,g10) = 8
    c: Coincident(g4,g-4)
    c: DistanceX(g4,g10) = 1.6
    c: Horizontal(g8)
    c: DistanceY(g8,g1) = 0
FEATURE [Sketcher::SketchObject] Sketch034  label="buchi guida rail"
  ArcFitTolerance = 1e-06
  AttachmentSupport = -> [XY_Plane]
  ExternalGeometry = -> [Sketch]
  FullyConstrained = true
  MakeInternals = false
  MapMode = 5
  sketch-geometry (6):
    g0: LineSegment [constr] StartX=-100.8 StartY=9.1e-15 StartZ=0 EndX=-93.3 EndY=0 EndZ=0
    g1: LineSegment [constr] StartX=-93.3 StartY=0 StartZ=0 EndX=-73.3 EndY=0 EndZ=0
    g2: LineSegment [constr] StartX=-73.3 StartY=0 StartZ=0 EndX=-53.3 EndY=0 EndZ=0
    g3: Circle CenterX=-93.3 CenterY=0 CenterZ=0 NormalX=0 NormalY=0 NormalZ=1 AngleXU=0 Radius=2.5
    g4: Circle CenterX=-73.3 CenterY=0 CenterZ=0 NormalX=0 NormalY=0 NormalZ=1 AngleXU=0 Radius=2.5
    g5: Circle CenterX=-53.3 CenterY=0 CenterZ=0 NormalX=0 NormalY=0 NormalZ=1 AngleXU=0 Radius=2.5
  constraints (15):
    c: Distance(g0) = 7.5
    c: Coincident(g0,g-3)
    c: PointOnObject(g0,g-1)
    c: Distance(g1) = 20
    c: Coincident(g1,g0)
    c: PointOnObject(g1,g-1)
    c: Distance(g2) = 20
    c: Coincident(g2,g1)
    c: PointOnObject(g2,g-1)
    c: Diameter(g3) = 5
    c: Diameter(g4) = 5
    c: Diameter(g5) = 5
    c: Coincident(g3,g0)
    c: Coincident(g4,g1)
    c: Coincident(g5,g2)
FEATURE [Part::Extrusion] Extrude032  label="Extrude buchi guida rail"
  Base = -> Sketch034
  Dir = (0,0,1)
  DirMode = 2
  FaceMakerClass = Part::FaceMakerBullseye
  FaceMakerMode = 3
  LengthFwd = -6.2
  LengthRev = 0
  Placement = pos=(0,0,43.2) rot=(0,0,1;0rad)
  Solid = true
  Symmetric = false
FEATURE [Part::Extrusion] Extrude033  label="Extrude fori superiori per solenoide e oled001"
  Base = -> Sketch030
  Dir = (0,0,1)
  DirMode = 2
  FaceMakerClass = Part::FaceMakerBullseye
  FaceMakerMode = 3
  LengthFwd = -4.8
  LengthRev = 0
  Placement = pos=(0,0,41.2) rot=(0,0,1;0rad)
  Solid = true
  Symmetric = false
FEATURE [Part::Extrusion] Extrude034  label="Extrude fori sotto impugnatura001"
  Base = -> Sketch029
  Dir = (0,0,1)
  DirMode = 2
  FaceMakerClass = Part::FaceMakerBullseye
  FaceMakerMode = 3
  LengthFwd = 5
  LengthRev = 0
  Placement = pos=(0,0,-83) rot=(0,0,1;0rad)
  Solid = true
  Symmetric = false
FEATURE [Part::Extrusion] Extrude035  label="Extrude fori inferiori switch pompa001"
  Base = -> Sketch031
  Dir = (0,0,1)
  DirMode = 2
  FaceMakerClass = Part::FaceMakerBullseye
  FaceMakerMode = 3
  LengthFwd = 4
  LengthRev = 0
  Placement = pos=(0,0,-1.7) rot=(0,0,1;0rad)
  Solid = true
  Symmetric = false
FEATURE [Part::Extrusion] Extrude036  label="Extrude foro sotto posteriore M3x5x007"
  Base = -> Sketch027
  Dir = (0,0,1)
  DirMode = 2
  FaceMakerClass = Part::FaceMakerBullseye
  FaceMakerMode = 3
  LengthFwd = 6.2
  LengthRev = 0
  Placement = pos=(0,0,-9.6) rot=(0,0,1;0rad)
  Solid = true
  Symmetric = false
FEATURE [Part::Extrusion] Extrude037  label="Extrude foro sotto anteriore M3x5x007"
  Base = -> Sketch026
  Dir = (0,0,1)
  DirMode = 2
  FaceMakerClass = Part::FaceMakerBullseye
  FaceMakerMode = 3
  LengthFwd = 6.2
  LengthRev = 0
  Solid = true
  Symmetric = false
FEATURE [Sketcher::SketchObject] Sketch035  label="foro per fissaggio micro"
  ArcFitTolerance = 1e-06
  AttachmentSupport = -> [XZ_Plane]
  ExternalGeometry = -> [Sketch,Sketch033]
  FullyConstrained = true
  MakeInternals = false
  MapMode = 5
  Placement = pos=(0,0,0) rot=(1,0,0;1.5708rad)
  sketch-geometry (3):
    g0: Circle CenterX=-7.8 CenterY=21.2 CenterZ=0 NormalX=0 NormalY=0 NormalZ=1 AngleXU=0 Radius=1.6
    g1: GeomPoint [constr] X=-4 Y=21.2 Z=0
    g2: LineSegment [constr] StartX=-4 StartY=21.2 StartZ=0 EndX=-11.6 EndY=21.2 EndZ=0
  constraints (6):
    c: Diameter(g0) = 3.2
    c: Symmetric(g-3,g-3,g1)
    c: Coincident(g2,g1)
    c: Horizontal(g2)
    c: DistanceX(g-4,g2) = 0
    c: Symmetric(g2,g1,g0)
FEATURE [Part::Extrusion] Extrude038  label="Extrude foro per fissaggio micro"
  Base = -> Sketch035
  Dir = (0,-1,2e-16)
  DirMode = 2
  FaceMakerClass = Part::FaceMakerBullseye
  FaceMakerMode = 3
  LengthFwd = 3
  LengthRev = 0
  Placement = pos=(0,8.6,0) rot=(0,0,1;0rad)
  Solid = true
  Symmetric = false
FEATURE [Sketcher::SketchObject] Sketch036  label="supporto per alimentatore"
  ArcFitTolerance = 1e-06
  AttachmentSupport = -> [XZ_Plane]
  ExternalGeometry = -> [Sketch,Sketch016,Sketch022]
  FullyConstrained = true
  MakeInternals = false
  MapMode = 5
  Placement = pos=(0,0,0) rot=(1,0,0;1.5708rad)
  sketch-geometry (5):
    g0: LineSegment StartX=-211.843 StartY=-50.0944 StartZ=0 EndX=-211.843 EndY=-80.4316 EndZ=0
    g1: LineSegment StartX=-211.843 StartY=-50.0944 StartZ=0 EndX=-207.775 EndY=-41.3701 EndZ=0
    g2: LineSegment [constr] StartX=-209.443 StartY=-50.0944 StartZ=0 EndX=-209.443 EndY=-80.4316 EndZ=0
    g3: LineSegment StartX=-207.775 StartY=-41.3701 StartZ=0 EndX=-207.775 EndY=-80.4316 EndZ=0
    g4: LineSegment StartX=-211.843 StartY=-80.4316 StartZ=0 EndX=-207.775 EndY=-80.4316 EndZ=0
  constraints (15):
    c: Vertical(g0)
    c: Coincident(g1,g0)
    c: Vertical(g2)
    c: Tangent(g2,g-5)
    c: Coincident(g3,g1)
    c: Vertical(g3)
    c: DistanceY(g-3,g3) = -2
    c: Tangent(g1,g-8)
    c: DistanceY(g-3,g0) = -2
    c: Coincident(g4,g0)
    c: Coincident(g4,g3)
    c: Tangent(g0,g-6)
    c: DistanceY(g-3,g2) = -2
    c: DistanceY(g2,g0) = 0
    c: DistanceX(g-3,g3) = 6.8
FEATURE [Part::Extrusion] Extrude039  label="Extrude039 supporto alimentatore"
  Base = -> Sketch036
  Dir = (0,-1,2e-16)
  DirMode = 2
  FaceMakerClass = Part::FaceMakerBullseye
  FaceMakerMode = 3
  LengthFwd = 25.2
  LengthRev = 0
  Solid = true
  Symmetric = true
FEATURE [Sketcher::SketchObject] Sketch037  label="scavo per alimentatore"
  ArcFitTolerance = 1e-06
  AttachmentSupport = -> [XZ_Plane]
  ExternalGeometry = -> [Sketch036]
  FullyConstrained = true
  MakeInternals = false
  MapMode = 5
  Placement = pos=(0,0,0) rot=(1,0,0;1.5708rad)
  sketch-geometry (4):
    g0: LineSegment StartX=-209.575 StartY=-50.4316 StartZ=0 EndX=-209.575 EndY=-80.4316 EndZ=0
    g1: LineSegment StartX=-209.575 StartY=-50.4316 StartZ=0 EndX=-207.775 EndY=-50.4316 EndZ=0
    g2: LineSegment StartX=-207.775 StartY=-50.4316 StartZ=0 EndX=-207.775 EndY=-80.4316 EndZ=0
    g3: LineSegment StartX=-207.775 StartY=-80.4316 StartZ=0 EndX=-209.575 EndY=-80.4316 EndZ=0
  constraints (11):
    c: Vertical(g0)
    c: Coincident(g1,g0)
    c: Horizontal(g1)
    c: Coincident(g2,g1)
    c: Vertical(g2)
    c: Coincident(g3,g2)
    c: Coincident(g3,g0)
    c: Horizontal(g3)
    c: DistanceX(g1,g1) = 1.8
    c: Coincident(g2,g-3)
    c: DistanceY(g2,g2) = 30
FEATURE [Part::Extrusion] Extrude040  label="Extrude040 scavo alimentatore"
  Base = -> Sketch037
  Dir = (0,-1,2e-16)
  DirMode = 2
  FaceMakerClass = Part::FaceMakerBullseye
  FaceMakerMode = 3
  LengthFwd = 19.5
  LengthRev = 0
  Solid = true
  Symmetric = true
FEATURE [Part::Extrusion] Extrude031  label="Extrude fermo per scheda micro"
  Base = -> Sketch033
  Dir = (0,-1,2e-16)
  DirMode = 2
  FaceMakerClass = Part::FaceMakerBullseye
  FaceMakerMode = 3
  LengthFwd = 3
  LengthRev = 0
  Placement = pos=(0,8.6,0) rot=(0,0,1;0rad)
  Solid = true
  Symmetric = false
FEATURE [Sketcher::SketchObject] Sketch038  label="scavo driver solenoide"
  ArcFitTolerance = 1e-06
  AttachmentSupport = -> [XZ_Plane]
  ExternalGeometry = -> [Sketch,Sketch036]
  FullyConstrained = true
  MakeInternals = false
  MapMode = 5
  Placement = pos=(0,0,0) rot=(1,0,0;1.5708rad)
  sketch-geometry (7):
    g0: LineSegment StartX=-192.222 StartY=-8.0175 StartZ=0 EndX=-194.941 EndY=-6.74965 EndZ=0
    g1: LineSegment StartX=-194.941 StartY=-6.74965 StartZ=0 EndX=-212.269 EndY=-43.9083 EndZ=0
    g2: LineSegment StartX=-192.222 StartY=-8.0175 StartZ=0 EndX=-188.779 EndY=-9.62345 EndZ=0
    g3: LineSegment StartX=-188.779 StartY=-9.62345 StartZ=0 EndX=-205.357 EndY=-45.1761 EndZ=0
    g4: LineSegment StartX=-205.357 StartY=-45.1761 StartZ=0 EndX=-209.55 EndY=-45.1761 EndZ=0
    g5: LineSegment [constr] StartX=-212.269 StartY=-43.9083 StartZ=0 EndX=-209.55 EndY=-45.1761 EndZ=0
    g6: LineSegment StartX=-212.269 StartY=-43.9083 StartZ=0 EndX=-209.55 EndY=-45.1761 EndZ=0
  constraints (20):
    c: Coincident(g1,g0)
    c: Coincident(g3,g2)
    c: Coincident(g4,g3)
    c: Distance(g2) = 3.8
    c: Distance(g1) = 41
    c: Coincident(g5,g1)
    c: Distance(g5) = 3
    c: Perpendicular(g5,g-3)
    c: Parallel(g1,g-3)
    c: Perpendicular(g1,g0)
    c: Distance(g0) = 3
    c: Coincident(g6,g1)
    c: Parallel(g3,g-3)
    c: Perpendicular(g2,g3)
    c: Coincident(g2,g0)
    c: Perpendicular(g-4,g4)
    c: PointOnObject(g5,g-3)
    c: Distance(g-3,g5) = 9.6
    c: Coincident(g4,g5)
    c: Coincident(g6,g4)
FEATURE [Part::Extrusion] Extrude041  label="Extrude scavo driver solenoide"
  Base = -> Sketch038
  Dir = (0,-1,2e-16)
  DirMode = 2
  FaceMakerClass = Part::FaceMakerBullseye
  FaceMakerMode = 3
  LengthFwd = 20.6
  LengthRev = 0
  Solid = true
  Symmetric = true
FEATURE [Sketcher::SketchObject] Sketch039  label="scavo per cavo usb per micro"
  ArcFitTolerance = 1e-06
  AttachmentSupport = -> [XZ_Plane]
  ExternalGeometry = -> [Sketch,Sketch016]
  FullyConstrained = true
  MakeInternals = false
  MapMode = 5
  Placement = pos=(0,0,0) rot=(1,0,0;1.5708rad)
  sketch-geometry (4):
    g0: LineSegment StartX=-82.51 StartY=36.4 StartZ=0 EndX=-74.51 EndY=36.4 EndZ=0
    g1: LineSegment StartX=-74.51 StartY=36.4 StartZ=0 EndX=-74.51 EndY=30.8 EndZ=0
    g2: LineSegment StartX=-74.51 StartY=30.8 StartZ=0 EndX=-82.51 EndY=30.8 EndZ=0
    g3: LineSegment StartX=-82.51 StartY=30.8 StartZ=0 EndX=-82.51 EndY=36.4 EndZ=0
  constraints (11):
    c: Coincident(g1,g0)
    c: Vertical(g1)
    c: Coincident(g2,g1)
    c: Horizontal(g2)
    c: Coincident(g3,g2)
    c: Coincident(g3,g0)
    c: Vertical(g3)
    c: Tangent(g0,g-3)
    c: Tangent(g2,g-4)
    c: Tangent(g3,g-4)
    c: Tangent(g1,g-4)
FEATURE [Part::Extrusion] Extrude042  label="Extrude scavo per cavo usb per micro"
  Base = -> Sketch039
  Dir = (0,-1,2e-16)
  DirMode = 2
  FaceMakerClass = Part::FaceMakerBullseye
  FaceMakerMode = 3
  LengthFwd = 11.2
  LengthRev = 0
  Solid = true
  Symmetric = true
FEATURE [Sketcher::SketchObject] Sketch040  label="scavo saldature alimentatore connettore 5v"
  ArcFitTolerance = 1e-06
  AttachmentSupport = -> [XZ_Plane]
  ExternalGeometry = -> [Sketch037]
  FullyConstrained = true
  MakeInternals = false
  MapMode = 5
  Placement = pos=(0,0,0) rot=(1,0,0;1.5708rad)
  sketch-geometry (4):
    g0: LineSegment StartX=-211.175 StartY=-52.4316 StartZ=0 EndX=-211.175 EndY=-56.4316 EndZ=0
    g1: LineSegment StartX=-211.175 StartY=-52.4316 StartZ=0 EndX=-209.575 EndY=-52.4316 EndZ=0
    g2: LineSegment StartX=-209.575 StartY=-52.4316 StartZ=0 EndX=-209.575 EndY=-56.4316 EndZ=0
    g3: LineSegment StartX=-209.575 StartY=-56.4316 StartZ=0 EndX=-211.175 EndY=-56.4316 EndZ=0
  constraints (11):
    c: Vertical(g0)
    c: Coincident(g1,g0)
    c: Horizontal(g1)
    c: Coincident(g2,g1)
    c: Coincident(g3,g2)
    c: Coincident(g3,g0)
    c: Horizontal(g3)
    c: DistanceX(g1,g1) = 1.6
    c: DistanceY(g2,g2) = 4
    c: Tangent(g2,g-3)
    c: DistanceY(g1,g-3) = 2
FEATURE [Part::Extrusion] Extrude043  label="Extrude scavo saldature alimentatore connettore 5v"
  Base = -> Sketch040
  Dir = (0,-1,2e-16)
  DirMode = 2
  FaceMakerClass = Part::FaceMakerBullseye
  FaceMakerMode = 3
  LengthFwd = 8
  LengthRev = 0
  Solid = true
  Symmetric = true
FEATURE [Sketcher::SketchObject] Sketch041  label="scavo saldature alimentatore connettore 5v verticali"
  ArcFitTolerance = 1e-06
  AttachmentSupport = -> [XZ_Plane]
  ExternalGeometry = -> [Sketch037]
  FullyConstrained = true
  MakeInternals = false
  MapMode = 5
  Placement = pos=(0,0,0) rot=(1,0,0;1.5708rad)
  sketch-geometry (4):
    g0: LineSegment StartX=-211.175 StartY=-53.6316 StartZ=0 EndX=-209.575 EndY=-53.6316 EndZ=0
    g1: LineSegment StartX=-209.575 StartY=-53.6316 StartZ=0 EndX=-209.575 EndY=-76.6316 EndZ=0
    g2: LineSegment StartX=-209.575 StartY=-76.6316 StartZ=0 EndX=-211.175 EndY=-76.6316 EndZ=0
    g3: LineSegment StartX=-211.175 StartY=-76.6316 StartZ=0 EndX=-211.175 EndY=-53.6316 EndZ=0
  constraints (11):
    c: Horizontal(g0)
    c: Coincident(g1,g0)
    c: Coincident(g2,g1)
    c: Horizontal(g2)
    c: Coincident(g3,g2)
    c: Coincident(g3,g0)
    c: Vertical(g3)
    c: DistanceY(g3,g3) = 23
    c: DistanceX(g0,g0) = 1.6
    c: Tangent(g1,g-3)
    c: DistanceY(g0,g-3) = 3.2
FEATURE [Part::Extrusion] Extrude044  label="Extrude scavo saldature alimentatore connettore 5v verticali"
  Base = -> Sketch041
  Dir = (0,-1,2e-16)
  DirMode = 2
  FaceMakerClass = Part::FaceMakerBullseye
  FaceMakerMode = 3
  LengthFwd = 3.2
  LengthRev = 0
  Placement = pos=(0,8.3,0) rot=(0,0,1;0rad)
  Solid = true
  Symmetric = false
FEATURE [Sketcher::SketchObject] Sketch042  label="fermi per driver solenoide e alimentatore"
  ArcFitTolerance = 1e-06
  AttachmentSupport = -> [XZ_Plane]
  ExternalGeometry = -> [Sketch036,Sketch037,Sketch,Sketch038]
  FullyConstrained = true
  MakeInternals = false
  MapMode = 5
  Placement = pos=(0,0,0) rot=(1,0,0;1.5708rad)
  sketch-geometry (27):
    g0: LineSegment StartX=-200.506 StartY=-25.7811 StartZ=0 EndX=-201.436 EndY=-27.775 EndZ=0
    g1: LineSegment StartX=-201.436 StartY=-27.775 StartZ=0 EndX=-199.442 EndY=-28.7048 EndZ=0
    g2: LineSegment StartX=-199.442 StartY=-28.7048 StartZ=0 EndX=-198.512 EndY=-26.7109 EndZ=0
    g3: LineSegment StartX=-198.512 StartY=-26.7109 StartZ=0 EndX=-200.506 EndY=-25.7811 EndZ=0
    g4: LineSegment StartX=-201.28 StartY=-23.6549 StartZ=0 EndX=-203.562 EndY=-28.5489 EndZ=0
    g5: LineSegment StartX=-203.562 StartY=-28.5489 StartZ=0 EndX=-200.118 EndY=-30.1549 EndZ=0
    g6: LineSegment StartX=-197.992 StartY=-29.381 StartZ=0 EndX=-197.062 EndY=-27.3871 EndZ=0
    g7: LineSegment StartX=-197.836 StartY=-25.2608 StartZ=0 EndX=-201.28 EndY=-23.6549 EndZ=0
    g8: LineSegment [constr] StartX=-198.668 StartY=-30.8311 StartZ=0 EndX=-197.992 EndY=-29.381 EndZ=0
    g9: LineSegment [constr] StartX=-198.668 StartY=-30.8311 StartZ=0 EndX=-200.118 EndY=-30.1549 EndZ=0
    g10: ArcOfCircle CenterX=-198.512 CenterY=-26.7109 CenterZ=0 NormalX=0 NormalY=0 NormalZ=1 AngleXU=0 Radius=1.6 StartAngle=5.84685 EndAngle=7.41765
    g11: GeomPoint [constr] X=-196.386 Y=-25.937 Z=0
    g12: ArcOfCircle CenterX=-199.442 CenterY=-28.7048 CenterZ=0 NormalX=0 NormalY=0 NormalZ=1 AngleXU=0 Radius=1.6 StartAngle=4.27606 EndAngle=5.84685
    g13: GeomPoint [constr] X=-198.668 Y=-30.8311 Z=0
    g14: LineSegment StartX=-207.775 StartY=-46.8316 StartZ=0 EndX=-207.775 EndY=-50.8316 EndZ=0
    g15: LineSegment StartX=-207.775 StartY=-46.8316 StartZ=0 EndX=-203.775 EndY=-46.8316 EndZ=0
    g16: LineSegment StartX=-203.775 StartY=-46.8316 StartZ=0 EndX=-203.775 EndY=-50.8316 EndZ=0
    g17: LineSegment StartX=-207.775 StartY=-50.8316 StartZ=0 EndX=-203.775 EndY=-50.8316 EndZ=0
    g18: LineSegment StartX=-209.375 StartY=-52.4316 StartZ=0 EndX=-203.775 EndY=-52.4316 EndZ=0
    g19: LineSegment StartX=-202.175 StartY=-50.8316 StartZ=0 EndX=-202.175 EndY=-46.8316 EndZ=0
    g20: LineSegment StartX=-203.775 StartY=-45.2316 StartZ=0 EndX=-209.375 EndY=-45.2316 EndZ=0
    g21: LineSegment StartX=-209.375 StartY=-45.2316 StartZ=0 EndX=-209.375 EndY=-52.4316 EndZ=0
    g22: ArcOfCircle CenterX=-203.775 CenterY=-46.8316 CenterZ=0 NormalX=0 NormalY=0 NormalZ=1 AngleXU=0 Radius=1.6 StartAngle=1.8e-15 EndAngle=1.5708
    g23: GeomPoint [constr] X=-202.175 Y=-45.2316 Z=0
    g24: ArcOfCircle CenterX=-203.775 CenterY=-50.8316 CenterZ=0 NormalX=0 NormalY=0 NormalZ=1 AngleXU=0 Radius=1.6 StartAngle=4.71239 EndAngle=6.28319
    g25: GeomPoint [constr] X=-202.175 Y=-52.4316 Z=0
    g26: LineSegment [constr] StartX=-207.775 StartY=-50.4316 StartZ=0 EndX=-207.775 EndY=-50.8316 EndZ=0
  constraints (69):
    c: Coincident(g1,g0)
    c: Coincident(g2,g1)
    c: Coincident(g3,g2)
    c: Coincident(g3,g0)
    c: Parallel(g0,g2)
    c: Perpendicular(g3,g0)
    c: Perpendicular(g1,g0)
    c: Coincident(g5,g4)
    c: Coincident(g7,g4)
    c: Distance(g3) = 2.2
    c: Distance(g2) = 2.2
    c: Parallel(g6,g2)
    c: Parallel(g6,g4)
    c: Perpendicular(g5,g6)
    c: Perpendicular(g7,g6)
    c: Distance(g13,g11) = 5.4
    c: Distance(g5,g13) = 5.4
    c: Coincident(g9,g8)
    c: Distance(g8) = 1.6
    c: Distance(g9) = 1.6
    c: Perpendicular(g9,g8)
    c: Parallel(g8,g6)
    c: Coincident(g8,g13)
    c: Distance(g8,g1) = 1.6
    c: Distance(g9,g1) = 1.6
    c: Tangent(g0,g-5)
    c: Distance(g0,g-6) = 19.2
    c: PointOnObject(g11,g7)
    c: PointOnObject(g11,g6)
    c: Tangent(g7,g10) = -1.5708
    c: Tangent(g6,g10) = -1.5708
    c: PointOnObject(g13,g5)
    c: Tangent(g5,g12) = -1.5708
    c: Tangent(g6,g12) = -1.5708
    c: Equal(g10,g12)
    c: Coincident(g10,g2)
    c: Vertical(g14)
    c: Coincident(g15,g14)
    c: Horizontal(g15)
    c: Coincident(g16,g15)
    c: Vertical(g16)
    c: Coincident(g17,g14)
    c: Coincident(g17,g16)
    c: Horizontal(g17)
    c: Distance(g16) = 4
    c: Distance(g15) = 4
    c: Horizontal(g18)
    c: Vertical(g19)
    c: Horizontal(g20)
    c: Coincident(g21,g20)
    c: Coincident(g21,g18)
    c: Vertical(g21)
    c: Distance(g20,g23) = 7.2
    c: Distance(g25,g23) = 7.2
    c: DistanceY(g18,g14) = 1.6
    c: DistanceX(g18,g14) = 1.6
    c: PointOnObject(g23,g20)
    c: PointOnObject(g23,g19)
    c: Tangent(g20,g22) = -1.5708
    c: Tangent(g19,g22) = -1.5708
    c: PointOnObject(g25,g19)
    c: Tangent(g18,g24) = -1.5708
    c: Tangent(g19,g24) = -1.5708
    c: Equal(g22,g24)
    c: Coincident(g22,g15)
    c: Vertical(g26)
    c: Distance(g26) = 0.4
    c: Coincident(g26,g-4)
    c: Coincident(g14,g26)
FEATURE [Part::Extrusion] Extrude045  label="Extrude fermi per driver solenoide e alimentatore"
  Base = -> Sketch042
  Dir = (0,-1,2e-16)
  DirMode = 2
  FaceMakerClass = Part::FaceMakerBullseye
  FaceMakerMode = 3
  LengthFwd = 25.2
  LengthRev = 0
  Solid = true
  Symmetric = true
FEATURE [Sketcher::SketchObject] Sketch043  label="scavo pulizia fermo alimentatore"
  ArcFitTolerance = 1e-06
  AttachmentSupport = -> [XZ_Plane]
  ExternalGeometry = -> [Sketch042,Sketch036,Sketch037]
  FullyConstrained = true
  MakeInternals = false
  MapMode = 5
  Placement = pos=(0,0,0) rot=(1,0,0;1.5708rad)
  sketch-geometry (6):
    g0: LineSegment StartX=-209.375 StartY=-52.4316 StartZ=0 EndX=-209.375 EndY=-50.4316 EndZ=0
    g1: LineSegment StartX=-209.375 StartY=-50.4316 StartZ=0 EndX=-207.775 EndY=-50.4316 EndZ=0
    g2: LineSegment StartX=-207.775 StartY=-50.4316 StartZ=0 EndX=-207.775 EndY=-45.2316 EndZ=0
    g3: LineSegment StartX=-207.775 StartY=-45.2316 StartZ=0 EndX=-202.175 EndY=-45.2316 EndZ=0
    g4: LineSegment StartX=-202.175 StartY=-45.2316 StartZ=0 EndX=-202.175 EndY=-52.4316 EndZ=0
    g5: LineSegment StartX=-202.175 StartY=-52.4316 StartZ=0 EndX=-209.375 EndY=-52.4316 EndZ=0
  constraints (13):
    c: Vertical(g0)
    c: Coincident(g1,g0)
    c: Coincident(g2,g1)
    c: Coincident(g3,g2)
    c: Coincident(g4,g3)
    c: Coincident(g5,g4)
    c: Coincident(g5,g0)
    c: Horizontal(g5)
    c: Coincident(g0,g-6)
    c: Tangent(g1,g-8)
    c: Tangent(g2,g-4)
    c: Tangent(g3,g-7)
    c: Tangent(g4,g-3)
FEATURE [Part::Extrusion] Extrude046  label="Extrude scavo pulizia fermo alimentatore"
  Base = -> Sketch043
  Dir = (0,-1,2e-16)
  DirMode = 2
  FaceMakerClass = Part::FaceMakerBullseye
  FaceMakerMode = 3
  LengthFwd = 19.5
  LengthRev = 0
  Solid = true
  Symmetric = true
FEATURE [Sketcher::SketchObject] Sketch044  label="buchini per fissaggio oled"
  ArcFitTolerance = 1e-06
  AttachmentSupport = -> [YZ_Plane]
  ExternalGeometry = -> [Sketch]
  FullyConstrained = true
  MakeInternals = false
  MapMode = 5
  Placement = pos=(0,0,0) rot=(0.57735,0.57735,0.57735;2.0944rad)
  sketch-geometry (5):
    g0: LineSegment [constr] StartX=1.5e-14 StartY=67.3588 StartZ=0 EndX=0 EndY=64.3588 EndZ=0
    g1: LineSegment [constr] StartX=0 StartY=64.3588 StartZ=0 EndX=10.4 EndY=64.3588 EndZ=0
    g2: LineSegment [constr] StartX=0 StartY=64.3588 StartZ=0 EndX=-10.4 EndY=64.3588 EndZ=0
    g3: Circle CenterX=10.4 CenterY=64.3588 CenterZ=0 NormalX=0 NormalY=0 NormalZ=1 AngleXU=0 Radius=1.5
    g4: Circle CenterX=-10.4 CenterY=64.3588 CenterZ=0 NormalX=0 NormalY=0 NormalZ=1 AngleXU=0 Radius=1.5
  constraints (13):
    c: Distance(g0) = 3
    c: PointOnObject(g0,g-2)
    c: Coincident(g1,g0)
    c: Horizontal(g1)
    c: Coincident(g2,g0)
    c: Horizontal(g2)
    c: DistanceX(g1,g1) = 10.4
    c: Coincident(g3,g1)
    c: Diameter(g4) = 3
    c: Coincident(g4,g2)
    c: Coincident(g0,g-7)
    c: Equal(g1,g2)
    c: Equal(g4,g3)
FEATURE [Part::Extrusion] Extrude047  label="Extrude buchini per fissaggio oled"
  Base = -> Sketch044
  Dir = (1,0,0)
  DirMode = 2
  FaceMakerClass = Part::FaceMakerBullseye
  FaceMakerMode = 3
  LengthFwd = 10
  LengthRev = 0
  Placement = pos=(-186,0,0) rot=(0,0,1;0rad)
  Solid = true
  Symmetric = false
FEATURE [Sketcher::SketchObject] Sketch046  label="scavo 5x5 neopixel"
  ArcFitTolerance = 1e-06
  AttachmentSupport = -> [YZ_Plane002]
  FullyConstrained = true
  MakeInternals = false
  MapMode = 5
  Placement = pos=(0,0,0) rot=(0.57735,0.57735,0.57735;2.0944rad)
  sketch-geometry (4):
    g0: LineSegment StartX=-2.7 StartY=2.7 StartZ=0 EndX=2.7 EndY=2.7 EndZ=0
    g1: LineSegment StartX=2.7 StartY=2.7 StartZ=0 EndX=2.7 EndY=-2.7 EndZ=0
    g2: LineSegment StartX=2.7 StartY=-2.7 StartZ=0 EndX=-2.7 EndY=-2.7 EndZ=0
    g3: LineSegment StartX=-2.7 StartY=-2.7 StartZ=0 EndX=-2.7 EndY=2.7 EndZ=0
  constraints (11):
    c: Horizontal(g0)
    c: Coincident(g1,g0)
    c: Vertical(g1)
    c: Coincident(g2,g1)
    c: Horizontal(g2)
    c: Coincident(g3,g2)
    c: Coincident(g3,g0)
    c: Vertical(g3)
    c: DistanceX(g0,g0) = 5.4
    c: DistanceY(g1,g1) = 5.4
    c: Symmetric(g0,g1,g-1)
FEATURE [Sketcher::SketchObject] Sketch047  label="scavo 10x10 neopixel corpo"
  ArcFitTolerance = 1e-06
  AttachmentOffset = pos=(0,0,1) rot=(0,0,1;0rad)
  AttachmentSupport = -> [YZ_Plane002]
  FullyConstrained = true
  MakeInternals = false
  MapMode = 5
  Placement = pos=(1,0,0) rot=(0.57735,0.57735,0.57735;2.0944rad)
  sketch-geometry (4):
    g0: LineSegment StartX=-5 StartY=5.1 StartZ=0 EndX=5 EndY=5.1 EndZ=0
    g1: LineSegment StartX=5 StartY=5.1 StartZ=0 EndX=5 EndY=-5.1 EndZ=0
    g2: LineSegment StartX=5 StartY=-5.1 StartZ=0 EndX=-5 EndY=-5.1 EndZ=0
    g3: LineSegment StartX=-5 StartY=-5.1 StartZ=0 EndX=-5 EndY=5.1 EndZ=0
  constraints (11):
    c: Horizontal(g0)
    c: Coincident(g1,g0)
    c: Vertical(g1)
    c: Coincident(g2,g1)
    c: Horizontal(g2)
    c: Coincident(g3,g2)
    c: Coincident(g3,g0)
    c: Vertical(g3)
    c: DistanceX(g0,g0) = 10
    c: DistanceY(g1,g1) = 10.2
    c: Symmetric(g0,g2,g-1)
FEATURE [Sketcher::SketchObject] Sketch048  label="buco per perno blocco neopixel"
  ArcFitTolerance = 1e-06
  AttachmentSupport = -> [XZ_Plane002]
  FullyConstrained = true
  MakeInternals = false
  MapMode = 5
  Placement = pos=(0,0,0) rot=(1,0,0;1.5708rad)
  sketch-geometry (4):
    g0: LineSegment StartX=3 StartY=1.2 StartZ=0 EndX=3 EndY=-1.2 EndZ=0
    g1: LineSegment StartX=3 StartY=-1.2 StartZ=0 EndX=5.4 EndY=-1.2 EndZ=0
    g2: LineSegment StartX=5.4 StartY=-1.2 StartZ=0 EndX=5.4 EndY=1.2 EndZ=0
    g3: LineSegment StartX=5.4 StartY=1.2 StartZ=0 EndX=3 EndY=1.2 EndZ=0
  constraints (11):
    c: Coincident(g1,g0)
    c: Horizontal(g1)
    c: Coincident(g2,g1)
    c: Vertical(g2)
    c: Coincident(g3,g2)
    c: Coincident(g3,g0)
    c: Horizontal(g3)
    c: DistanceX(g1,g1) = 2.4
    c: DistanceY(g2,g2) = 2.4
    c: Symmetric(g0,g0,g-1)
    c: DistanceX(g-1,g0) = 3
FEATURE [Sketcher::SketchObject] Sketch045  label="blocco principale per neopixel"
  ArcFitTolerance = 1e-06
  AttachmentSupport = -> [XZ_Plane002]
  ExternalGeometry = -> [Sketch048]
  FullyConstrained = true
  MakeInternals = false
  MapMode = 5
  Placement = pos=(0,0,0) rot=(1,0,0;1.5708rad)
  sketch-geometry (6):
    g0: LineSegment StartX=0 StartY=5.1 StartZ=0 EndX=0 EndY=-5.1 EndZ=0
    g1: LineSegment StartX=0 StartY=-5.1 StartZ=0 EndX=3 EndY=-5.1 EndZ=0
    g2: LineSegment StartX=7 StartY=-1.1 StartZ=0 EndX=7 EndY=5.1 EndZ=0
    g3: LineSegment StartX=7 StartY=5.1 StartZ=0 EndX=0 EndY=5.1 EndZ=0
    g4: ArcOfCircle CenterX=3 CenterY=-1.1 CenterZ=0 NormalX=0 NormalY=0 NormalZ=1 AngleXU=0 Radius=4 StartAngle=4.71239 EndAngle=6.28319
    g5: GeomPoint [constr] X=7 Y=-5.1 Z=0
  constraints (15):
    c: Vertical(g0)
    c: Coincident(g1,g0)
    c: Horizontal(g1)
    c: Vertical(g2)
    c: Coincident(g3,g2)
    c: Coincident(g3,g0)
    c: Horizontal(g3)
    c: DistanceY(g0,g0) = 10.2
    c: Symmetric(g0,g0,g-1)
    c: DistanceX(g3,g3) = 7
    c: PointOnObject(g5,g2)
    c: PointOnObject(g5,g1)
    c: Tangent(g2,g4) = -1.5708
    c: Tangent(g1,g4) = -1.5708
    c: DistanceX(g-3,g1) = 0
FEATURE [Sketcher::SketchObject] Sketch049  label="rinforzi esterni per corpo neopoixel"
  ArcFitTolerance = 1e-06
  AttachmentSupport = -> [XZ_Plane002]
  ExternalGeometry = -> [Sketch045]
  FullyConstrained = true
  MakeInternals = false
  MapMode = 5
  Placement = pos=(0,0,0) rot=(1,0,0;1.5708rad)
  sketch-geometry (8):
    g0: LineSegment StartX=1 StartY=-4.1 StartZ=0 EndX=2 EndY=-4.1 EndZ=0
    g1: LineSegment StartX=2 StartY=-4.1 StartZ=0 EndX=2 EndY=-5.1 EndZ=0
    g2: LineSegment StartX=2 StartY=-5.1 StartZ=0 EndX=1 EndY=-5.1 EndZ=0
    g3: LineSegment StartX=1 StartY=-5.1 StartZ=0 EndX=1 EndY=-4.1 EndZ=0
    g4: LineSegment StartX=1 StartY=5.1 StartZ=0 EndX=2 EndY=5.1 EndZ=0
    g5: LineSegment StartX=2 StartY=5.1 StartZ=0 EndX=2 EndY=4.1 EndZ=0
    g6: LineSegment StartX=2 StartY=4.1 StartZ=0 EndX=1 EndY=4.1 EndZ=0
    g7: LineSegment StartX=1 StartY=4.1 StartZ=0 EndX=1 EndY=5.1 EndZ=0
  constraints (24):
    c: Horizontal(g0)
    c: Coincident(g1,g0)
    c: Vertical(g1)
    c: Coincident(g2,g1)
    c: Horizontal(g2)
    c: Coincident(g3,g2)
    c: Coincident(g3,g0)
    c: Vertical(g3)
    c: Horizontal(g4)
    c: Coincident(g5,g4)
    c: Vertical(g5)
    c: Coincident(g6,g5)
    c: Horizontal(g6)
    c: Coincident(g7,g6)
    c: Coincident(g7,g4)
    c: Vertical(g7)
    c: DistanceX(g4,g4) = 1
    c: DistanceY(g5,g5) = 1
    c: DistanceX(g0,g0) = 1
    c: DistanceY(g1,g1) = 1
    c: DistanceX(g-3,g4) = 1
    c: DistanceY(g-3,g4) = 0
    c: DistanceX(g-4,g2) = 1
    c: DistanceY(g2,g-4) = 0
FEATURE [Sketcher::SketchObject] Sketch052  label="scavo saldature driver solenoide"
  ArcFitTolerance = 1e-06
  AttachmentSupport = -> [XZ_Plane]
  ExternalGeometry = -> [Sketch038]
  FullyConstrained = true
  MakeInternals = false
  MapMode = 5
  Placement = pos=(0,0,0) rot=(1,0,0;1.5708rad)
  sketch-geometry (4):
    g0: LineSegment StartX=-195.304 StartY=-6.5806 StartZ=0 EndX=-196.994 EndY=-10.2058 EndZ=0
    g1: LineSegment StartX=-196.994 StartY=-10.2058 StartZ=0 EndX=-196.632 EndY=-10.3749 EndZ=0
    g2: LineSegment StartX=-196.632 StartY=-10.3749 StartZ=0 EndX=-194.941 EndY=-6.74965 EndZ=0
    g3: LineSegment StartX=-194.941 StartY=-6.74965 StartZ=0 EndX=-195.304 EndY=-6.5806 EndZ=0
  constraints (11):
    c: Coincident(g1,g0)
    c: Coincident(g2,g1)
    c: Coincident(g3,g2)
    c: Coincident(g3,g0)
    c: Parallel(g2,g0)
    c: Perpendicular(g2,g3)
    c: Perpendicular(g1,g2,g1) = 1.5708
    c: Parallel(g2,g-3)
    c: Distance(g2) = 4
    c: Distance(g3) = 0.4
    c: Coincident(g2,g-3)
FEATURE [Part::Extrusion] Extrude055  label="Extrude scavo saldature driver solenoide"
  Base = -> Sketch052
  Dir = (0,-1,2e-16)
  DirMode = 2
  FaceMakerClass = Part::FaceMakerBullseye
  FaceMakerMode = 3
  LengthFwd = 6
  LengthRev = 0
  Solid = true
  Symmetric = true
FEATURE [Sketcher::SketchObject] Sketch053  label="scavo saldature rumble"
  ArcFitTolerance = 1e-06
  AttachmentSupport = -> [XZ_Plane]
  ExternalGeometry = -> [Sketch019]
  FullyConstrained = true
  MakeInternals = false
  MapMode = 5
  Placement = pos=(0,0,0) rot=(1,0,0;1.5708rad)
  sketch-geometry (4):
    g0: LineSegment StartX=-164.507 StartY=-41.6446 StartZ=0 EndX=-165.743 EndY=-45.4488 EndZ=0
    g1: LineSegment StartX=-165.743 StartY=-45.4488 StartZ=0 EndX=-164.602 EndY=-45.8196 EndZ=0
    g2: LineSegment StartX=-164.602 StartY=-45.8196 StartZ=0 EndX=-163.366 EndY=-42.0154 EndZ=0
    g3: LineSegment StartX=-163.366 StartY=-42.0154 StartZ=0 EndX=-164.507 EndY=-41.6446 EndZ=0
  constraints (11):
    c: Coincident(g1,g0)
    c: Coincident(g2,g1)
    c: Coincident(g3,g2)
    c: Coincident(g3,g0)
    c: Parallel(g0,g2)
    c: Perpendicular(g3,g0)
    c: Perpendicular(g1,g0)
    c: Parallel(g0,g-3)
    c: Distance(g0) = 4
    c: Distance(g1) = 1.2
    c: Coincident(g0,g-3)
FEATURE [Part::Extrusion] Extrude056  label="Extrude scavo saldature rumble"
  Base = -> Sketch053
  Dir = (0,-1,2e-16)
  DirMode = 2
  FaceMakerClass = Part::FaceMakerBullseye
  FaceMakerMode = 3
  LengthFwd = 8.4
  LengthRev = 0
  Solid = true
  Symmetric = true
FEATURE [Sketcher::SketchObject] Sketch054  label="scavo saldature alimentatore connettore USB"
  ArcFitTolerance = 1e-06
  AttachmentSupport = -> [XZ_Plane]
  ExternalGeometry = -> [Sketch037]
  FullyConstrained = true
  MakeInternals = false
  MapMode = 5
  Placement = pos=(0,0,0) rot=(1,0,0;1.5708rad)
  sketch-geometry (4):
    g0: LineSegment StartX=-209.575 StartY=-80.4316 StartZ=0 EndX=-210.375 EndY=-80.4316 EndZ=0
    g1: LineSegment StartX=-210.375 StartY=-80.4316 StartZ=0 EndX=-210.375 EndY=-72.4316 EndZ=0
    g2: LineSegment StartX=-210.375 StartY=-72.4316 StartZ=0 EndX=-209.575 EndY=-72.4316 EndZ=0
    g3: LineSegment StartX=-209.575 StartY=-72.4316 StartZ=0 EndX=-209.575 EndY=-80.4316 EndZ=0
  constraints (11):
    c: Horizontal(g0)
    c: Coincident(g1,g0)
    c: Vertical(g1)
    c: Coincident(g2,g1)
    c: Horizontal(g2)
    c: Coincident(g3,g2)
    c: Coincident(g3,g0)
    c: Vertical(g3)
    c: DistanceX(g0,g0) = 0.8
    c: DistanceY(g3,g3) = 8
    c: Coincident(g0,g-4)
FEATURE [Part::Extrusion] Extrude057  label="Extrude scavo saldature alimentatore connettore USB"
  Base = -> Sketch054
  Dir = (0,-1,2e-16)
  DirMode = 2
  FaceMakerClass = Part::FaceMakerBullseye
  FaceMakerMode = 3
  LengthFwd = 11
  LengthRev = 0
  Solid = true
  Symmetric = true
FEATURE [Sketcher::SketchObject] Sketch055  label="buco interno per micro switch"
  ArcFitTolerance = 1e-06
  AttachmentSupport = -> [XZ_Plane]
  ExternalGeometry = -> [Sketch]
  FullyConstrained = true
  MakeInternals = false
  MapMode = 5
  Placement = pos=(0,0,0) rot=(1,0,0;1.5708rad)
  sketch-geometry (11):
    g0: LineSegment [constr] StartX=-194.483 StartY=34.2854 StartZ=0 EndX=-196.022 EndY=30.0568 EndZ=0
    g1: LineSegment [constr] StartX=-196.022 StartY=30.0568 StartZ=0 EndX=-197.561 EndY=25.8282 EndZ=0
    g2: LineSegment [constr] StartX=-196.022 StartY=30.0568 StartZ=0 EndX=-194.143 EndY=29.3727 EndZ=0
    g3: LineSegment [constr] StartX=-196.022 StartY=30.0568 StartZ=0 EndX=-197.902 EndY=30.7408 EndZ=0
    g4: LineSegment StartX=-196.362 StartY=34.9694 StartZ=0 EndX=-192.604 EndY=33.6014 EndZ=0
    g5: LineSegment StartX=-199.441 StartY=26.5122 StartZ=0 EndX=-195.682 EndY=25.1441 EndZ=0
    g6: LineSegment StartX=-192.604 StartY=33.6014 StartZ=0 EndX=-195.682 EndY=25.1441 EndZ=0
    g7: LineSegment StartX=-196.362 StartY=34.9694 StartZ=0 EndX=-199.441 EndY=26.5122 EndZ=0
    g8: GeomPoint [constr] X=-187.821 Y=29.2 Z=0
    g9: LineSegment [constr] StartX=-188.505 StartY=27.3206 StartZ=0 EndX=-196.022 EndY=30.0568 EndZ=0
    g10: LineSegment [constr] StartX=-187.821 StartY=29.2 StartZ=0 EndX=-188.505 EndY=27.3206 EndZ=0
  constraints (27):
    c: Coincident(g2,g0)
    c: Parallel(g0,g-3)
    c: Tangent(g1,g0) = -1.5708
    c: Perpendicular(g0,g2)
    c: Tangent(g2,g3)
    c: Distance(g0,g1) = 9
    c: Equal(g0,g1)
    c: Distance(g3,g2) = 4
    c: Equal(g2,g3)
    c: Parallel(g3,g4)
    c: Symmetric(g4,g4,g0)
    c: Parallel(g6,g1)
    c: Parallel(g7,g1)
    c: Symmetric(g6,g6,g2)
    c: Symmetric(g5,g5,g1)
    c: Symmetric(g7,g7,g3)
    c: Coincident(g7,g4)
    c: Coincident(g6,g4)
    c: Coincident(g5,g6)
    c: Symmetric(g-3,g-3,g8)
    c: Perpendicular(g-3,g9)
    c: Distance(g9) = 8
    c: Coincident(g3,g9)
    c: Coincident(g10,g8)
    c: Parallel(g10,g-3)
    c: Distance(g10) = 2
    c: Coincident(g10,g9)
FEATURE [Sketcher::SketchObject] Sketch056  label="buco esterno per micro switch"
  ArcFitTolerance = 1e-06
  AttachmentSupport = -> [XZ_Plane]
  ExternalGeometry = -> [Sketch055]
  FullyConstrained = true
  MakeInternals = false
  MapMode = 5
  Placement = pos=(0,0,0) rot=(1,0,0;1.5708rad)
  sketch-geometry (17):
    g0: GeomPoint [constr] X=-194.143 Y=29.3727 Z=0
    g1: GeomPoint [constr] X=-194.483 Y=34.2854 Z=0
    g2: GeomPoint [constr] X=-197.902 Y=30.7408 Z=0
    g3: GeomPoint [constr] X=-197.561 Y=25.8282 Z=0
    g4: GeomPoint [constr] X=-196.022 Y=30.0568 Z=0
    g5: LineSegment [constr] StartX=-194.483 StartY=34.2854 StartZ=0 EndX=-196.022 EndY=30.0568 EndZ=0
    g6: LineSegment [constr] StartX=-196.022 StartY=30.0568 StartZ=0 EndX=-197.561 EndY=25.8282 EndZ=0
    g7: LineSegment [constr] StartX=-197.902 StartY=30.7408 StartZ=0 EndX=-196.022 EndY=30.0568 EndZ=0
    g8: LineSegment [constr] StartX=-196.022 StartY=30.0568 StartZ=0 EndX=-194.143 EndY=29.3727 EndZ=0
    g9: LineSegment [constr] StartX=-195.338 StartY=31.9362 StartZ=0 EndX=-196.022 EndY=30.0568 EndZ=0
    g10: LineSegment [constr] StartX=-196.022 StartY=30.0568 StartZ=0 EndX=-196.706 EndY=28.1774 EndZ=0
    g11: LineSegment [constr] StartX=-196.022 StartY=30.0568 StartZ=0 EndX=-196.821 EndY=30.3475 EndZ=0
    g12: LineSegment [constr] StartX=-196.022 StartY=30.0568 StartZ=0 EndX=-195.223 EndY=29.7661 EndZ=0
    g13: LineSegment StartX=-194.539 StartY=31.6454 StartZ=0 EndX=-195.907 EndY=27.8867 EndZ=0
    g14: LineSegment StartX=-196.137 StartY=32.2269 StartZ=0 EndX=-197.505 EndY=28.4681 EndZ=0
    g15: LineSegment StartX=-196.137 StartY=32.2269 StartZ=0 EndX=-194.539 EndY=31.6454 EndZ=0
    g16: LineSegment StartX=-197.505 StartY=28.4681 StartZ=0 EndX=-195.907 EndY=27.8867 EndZ=0
  constraints (34):
    c: Symmetric(g-5,g-5,g1)
    c: Symmetric(g-5,g-6,g0)
    c: Symmetric(g-6,g-6,g3)
    c: Symmetric(g-5,g-6,g2)
    c: Coincident(g5,g1)
    c: Coincident(g5,g4)
    c: Coincident(g6,g4)
    c: Coincident(g6,g3)
    c: Equal(g5,g6)
    c: Coincident(g7,g2)
    c: Coincident(g7,g4)
    c: Coincident(g8,g4)
    c: Coincident(g8,g0)
    c: Equal(g7,g8)
    c: Coincident(g11,g9)
    c: Coincident(g12,g9)
    c: Tangent(g10,g9) = -1.5708
    c: Perpendicular(g11,g9)
    c: Parallel(g9,g-4)
    c: Equal(g9,g10)
    c: Parallel(g12,g11)
    c: Equal(g11,g12)
    c: Distance(g11,g12) = 1.7
    c: Distance(g9,g10) = 4
    c: Symmetric(g13,g13,g12)
    c: Parallel(g13,g9)
    c: Symmetric(g14,g14,g11)
    c: Symmetric(g15,g15,g9)
    c: Parallel(g15,g11)
    c: Symmetric(g16,g16,g10)
    c: Coincident(g16,g14)
    c: Coincident(g15,g14)
    c: Coincident(g13,g15)
    c: Coincident(g9,g4)
FEATURE [Sketcher::SketchObject] Sketch057  label="buco interno per SWITCH"
  ArcFitTolerance = 1e-06
  AttachmentSupport = -> [XZ_Plane]
  ExternalGeometry = -> [Sketch]
  FullyConstrained = true
  MakeInternals = false
  MapMode = 5
  Placement = pos=(0,0,0) rot=(1,0,0;1.5708rad)
  sketch-geometry (10):
    g0: GeomPoint [constr] X=-187.821 Y=29.2 Z=0
    g1: LineSegment [constr] StartX=-188.505 StartY=27.3206 StartZ=0 EndX=-193.203 EndY=29.0307 EndZ=0
    g2: LineSegment [constr] StartX=-190.809 StartY=35.6086 StartZ=0 EndX=-195.597 EndY=22.4529 EndZ=0
    g3: GeomPoint [constr] X=-193.203 Y=29.0307 Z=0
    g4: LineSegment [constr] StartX=-196.492 StartY=30.2278 StartZ=0 EndX=-189.914 EndY=27.8336 EndZ=0
    g5: LineSegment StartX=-194.098 StartY=36.8056 StartZ=0 EndX=-187.52 EndY=34.4115 EndZ=0
    g6: LineSegment StartX=-194.098 StartY=36.8056 StartZ=0 EndX=-198.886 EndY=23.6499 EndZ=0
    g7: LineSegment StartX=-187.52 StartY=34.4115 StartZ=0 EndX=-192.308 EndY=21.2558 EndZ=0
    g8: LineSegment StartX=-198.886 StartY=23.6499 StartZ=0 EndX=-192.308 EndY=21.2558 EndZ=0
    g9: LineSegment [constr] StartX=-187.821 StartY=29.2 StartZ=0 EndX=-188.505 EndY=27.3206 EndZ=0
  constraints (23):
    c: Symmetric(g-3,g-3,g0)
    c: Perpendicular(g1,g-3)
    c: Parallel(g2,g-3)
    c: Symmetric(g2,g2,g3)
    c: Perpendicular(g2,g4)
    c: Symmetric(g4,g4,g3)
    c: Distance(g2) = 14
    c: Distance(g4) = 7
    c: Distance(g1) = 5
    c: Parallel(g5,g4)
    c: Parallel(g7,g2)
    c: Symmetric(g5,g5,g2)
    c: Symmetric(g6,g6,g4)
    c: Symmetric(g7,g7,g4)
    c: Symmetric(g8,g8,g2)
    c: Coincident(g6,g5)
    c: Coincident(g7,g5)
    c: Coincident(g8,g7)
    c: Coincident(g3,g1)
    c: Coincident(g9,g0)
    c: Parallel(g9,g-3)
    c: Distance(g9) = 2
    c: Coincident(g1,g9)
FEATURE [Sketcher::SketchObject] Sketch058  label="buco esterno per SWITCH"
  ArcFitTolerance = 1e-06
  AttachmentSupport = -> [XZ_Plane]
  ExternalGeometry = -> [Sketch057]
  FullyConstrained = true
  MakeInternals = false
  MapMode = 5
  Placement = pos=(0,0,0) rot=(1,0,0;1.5708rad)
  sketch-geometry (12):
    g0: GeomPoint [constr] X=-190.809 Y=35.6086 Z=0
    g1: GeomPoint [constr] X=-196.492 Y=30.2278 Z=0
    g2: GeomPoint [constr] X=-189.914 Y=27.8336 Z=0
    g3: GeomPoint [constr] X=-195.597 Y=22.4529 Z=0
    g4: GeomPoint [constr] X=-193.203 Y=29.0307 Z=0
    g5: LineSegment [constr] StartX=-192.006 StartY=32.3196 StartZ=0 EndX=-194.4 EndY=25.7418 EndZ=0
    g6: GeomPoint [constr] X=-193.203 Y=29.0307 Z=0
    g7: LineSegment [constr] StartX=-195.082 StartY=29.7148 StartZ=0 EndX=-191.324 EndY=28.3467 EndZ=0
    g8: LineSegment StartX=-193.885 StartY=33.0037 StartZ=0 EndX=-190.127 EndY=31.6356 EndZ=0
    g9: LineSegment StartX=-190.127 StartY=31.6356 StartZ=0 EndX=-192.521 EndY=25.0578 EndZ=0
    g10: LineSegment StartX=-196.28 StartY=26.4258 StartZ=0 EndX=-192.521 EndY=25.0578 EndZ=0
    g11: LineSegment StartX=-193.885 StartY=33.0037 StartZ=0 EndX=-196.28 EndY=26.4258 EndZ=0
  constraints (21):
    c: Symmetric(g-6,g-6,g3)
    c: Symmetric(g-4,g-6,g2)
    c: Symmetric(g-5,g-4,g0)
    c: Symmetric(g-5,g-6,g1)
    c: Symmetric(g1,g2,g4)
    c: Parallel(g5,g-4)
    c: Symmetric(g5,g5,g6)
    c: Perpendicular(g7,g5)
    c: Symmetric(g7,g7,g6)
    c: Distance(g5) = 7
    c: Distance(g7) = 4
    c: Parallel(g8,g7)
    c: Parallel(g11,g5)
    c: Symmetric(g8,g8,g5)
    c: Symmetric(g9,g9,g7)
    c: Symmetric(g10,g10,g5)
    c: Symmetric(g11,g11,g7)
    c: Coincident(g11,g8)
    c: Coincident(g9,g8)
    c: Coincident(g9,g10)
    c: Coincident(g6,g4)
FEATURE [Part::Extrusion] Extrude060  label="Extrude buco interno per SWITCH destro"
  Base = -> Sketch057
  Dir = (0,-1,2e-16)
  DirMode = 2
  FaceMakerClass = Part::FaceMakerBullseye
  FaceMakerMode = 3
  LengthFwd = 13.2
  LengthRev = 0
  Placement = pos=(0,2.6,0) rot=(0,0,1;0rad)
  Solid = true
  Symmetric = false
FEATURE [Part::Extrusion] Extrude061  label="Extrude buco esterno per SWITCH destro"
  Base = -> Sketch058
  Dir = (0,-1,2e-16)
  DirMode = 2
  FaceMakerClass = Part::FaceMakerBullseye
  FaceMakerMode = 3
  LengthFwd = 2
  LengthRev = 0
  Placement = pos=(0,-10.6,0) rot=(0,0,1;0rad)
  Solid = true
  Symmetric = false
FEATURE [Sketcher::SketchObject] Sketch059  label="buco per spazio introduzione SWITCH"
  ArcFitTolerance = 1e-06
  AttachmentSupport = -> [XZ_Plane]
  ExternalGeometry = -> [Sketch057,Sketch010]
  FullyConstrained = true
  MakeInternals = false
  MapMode = 5
  Placement = pos=(0,0,0) rot=(1,0,0;1.5708rad)
  sketch-geometry (8):
    g0: LineSegment [constr] StartX=-201.368 StartY=36.3521 StartZ=0 EndX=-195.094 EndY=34.0687 EndZ=0
    g1: LineSegment [constr] StartX=-194.098 StartY=36.8056 StartZ=0 EndX=-195.094 EndY=34.0687 EndZ=0
    g2: LineSegment StartX=-198.658 StartY=24.2771 StartZ=0 EndX=-199.654 EndY=21.5401 EndZ=0
    g3: LineSegment StartX=-199.654 StartY=21.5401 StartZ=0 EndX=-181.196 EndY=14.822 EndZ=0
    g4: LineSegment StartX=-181.196 StartY=14.822 StartZ=0 EndX=-180.2 EndY=17.559 EndZ=0
    g5: LineSegment StartX=-180.2 StartY=17.559 StartZ=0 EndX=-198.658 EndY=24.2771 EndZ=0
    g6: LineSegment [constr] StartX=-204.932 StartY=26.5605 StartZ=0 EndX=-198.658 EndY=24.2771 EndZ=0
    g7: LineSegment [constr] StartX=-198.658 StartY=24.2771 StartZ=0 EndX=-199.654 EndY=21.5401 EndZ=0
  constraints (20):
    c: Parallel(g1,g-3)
    c: Parallel(g0,g-4)
    c: Coincident(g0,g-4)
    c: Coincident(g1,g-3)
    c: Coincident(g0,g1)
    c: Coincident(g3,g2)
    c: Coincident(g4,g3)
    c: Coincident(g5,g4)
    c: Coincident(g5,g2)
    c: Parallel(g5,g-5)
    c: Parallel(g3,g-5)
    c: Parallel(g4,g-6)
    c: DistanceX(g-6,g4) = 0
    c: Coincident(g6,g-5)
    c: Equal(g6,g0)
    c: Coincident(g7,g6)
    c: Equal(g7,g1)
    c: Tangent(g7,g-3)
    c: Coincident(g2,g6)
    c: Coincident(g2,g7)
FEATURE [Part::Extrusion] Extrude062  label="Extrude buco per spazio introduzione SWITCH"
  Base = -> Sketch059
  Dir = (0,-1,2e-16)
  DirMode = 2
  FaceMakerClass = Part::FaceMakerBullseye
  FaceMakerMode = 3
  LengthFwd = 13.2
  LengthRev = 0
  Solid = true
  Symmetric = true
FEATURE [Part::Extrusion] Extrude063  label="Extrude buco interno per SWITCH sinistro"
  Base = -> Sketch057
  Dir = (0,-1,2e-16)
  DirMode = 2
  FaceMakerClass = Part::FaceMakerBullseye
  FaceMakerMode = 3
  LengthFwd = 13.2
  LengthRev = 0
  Placement = pos=(0,10.6,0) rot=(0,0,1;0rad)
  Solid = true
  Symmetric = false
FEATURE [Part::Extrusion] Extrude064  label="Extrude buco esterno per SWITCH sinistro"
  Base = -> Sketch058
  Dir = (0,-1,2e-16)
  DirMode = 2
  FaceMakerClass = Part::FaceMakerBullseye
  FaceMakerMode = 3
  LengthFwd = 2
  LengthRev = 0
  Placement = pos=(0,12.6,0) rot=(0,0,1;0rad)
  Solid = true
  Symmetric = false
FEATURE [Sketcher::SketchObject] Sketch061  label="struttura esterna blocco switch"
  ArcFitTolerance = 1e-06
  AttachmentSupport = -> [XZ_Plane003]
  FullyConstrained = true
  MakeInternals = false
  MapMode = 5
  Placement = pos=(0,0,0) rot=(1,0,0;1.5708rad)
  sketch-geometry (5):
    g0: LineSegment StartX=-1 StartY=-5.1 StartZ=0 EndX=1 EndY=-5.1 EndZ=0
    g1: LineSegment StartX=1 StartY=-5.1 StartZ=0 EndX=1 EndY=5.1 EndZ=0
    g2: LineSegment StartX=1 StartY=5.1 StartZ=0 EndX=-1 EndY=5.1 EndZ=0
    g3: LineSegment StartX=-1 StartY=5.1 StartZ=0 EndX=-1 EndY=-5.1 EndZ=0
    g4: GeomPoint [constr] X=0 Y=0 Z=0
  constraints (12):
    c: Coincident(g0,g1)
    c: Coincident(g1,g2)
    c: Coincident(g2,g3)
    c: Coincident(g3,g0)
    c: Horizontal(g0)
    c: Horizontal(g2)
    c: Vertical(g1)
    c: Vertical(g3)
    c: Symmetric(g2,g0,g4)
    c: Distance(g1,g3) = 2
    c: Distance(g0,g2) = 10.2
    c: Coincident(g4,g-1)
FEATURE [Sketcher::SketchObject] Sketch062  label="struttura interna blocco switch"
  ArcFitTolerance = 1e-06
  AttachmentSupport = -> [XZ_Plane003]
  ExternalGeometry = -> [Sketch061]
  FullyConstrained = true
  MakeInternals = false
  MapMode = 5
  Placement = pos=(0,0,0) rot=(1,0,0;1.5708rad)
  sketch-geometry (5):
    g0: LineSegment StartX=-1 StartY=3.1 StartZ=0 EndX=-1 EndY=-3.1 EndZ=0
    g1: LineSegment StartX=-1 StartY=-3.1 StartZ=0 EndX=1 EndY=-3.1 EndZ=0
    g2: LineSegment StartX=1 StartY=-3.1 StartZ=0 EndX=1 EndY=3.1 EndZ=0
    g3: LineSegment StartX=1 StartY=3.1 StartZ=0 EndX=-1 EndY=3.1 EndZ=0
    g4: GeomPoint [constr] X=0 Y=0 Z=0
  constraints (12):
    c: Coincident(g0,g1)
    c: Coincident(g1,g2)
    c: Coincident(g2,g3)
    c: Coincident(g3,g0)
    c: Vertical(g0)
    c: Vertical(g2)
    c: Horizontal(g1)
    c: Horizontal(g3)
    c: Symmetric(g2,g0,g4)
    c: Coincident(g4,g-1)
    c: Distance(g0) = 6.2
    c: Equal(g3,g-3)
FEATURE [Sketcher::SketchObject] Sketch063  label="blocchi tra switch"
  ArcFitTolerance = 1e-06
  AttachmentSupport = -> [XZ_Plane003]
  ExternalGeometry = -> [Sketch061,Sketch062]
  FullyConstrained = true
  MakeInternals = false
  MapMode = 5
  Placement = pos=(0,0,0) rot=(1,0,0;1.5708rad)
  sketch-geometry (8):
    g0: LineSegment StartX=-3 StartY=5.1 StartZ=0 EndX=-1 EndY=5.1 EndZ=0
    g1: LineSegment StartX=-1 StartY=5.1 StartZ=0 EndX=-1 EndY=3.1 EndZ=0
    g2: LineSegment StartX=-1 StartY=3.1 StartZ=0 EndX=-3 EndY=3.1 EndZ=0
    g3: LineSegment StartX=-3 StartY=3.1 StartZ=0 EndX=-3 EndY=5.1 EndZ=0
    g4: LineSegment StartX=-3 StartY=-3.1 StartZ=0 EndX=-1 EndY=-3.1 EndZ=0
    g5: LineSegment StartX=-1 StartY=-3.1 StartZ=0 EndX=-1 EndY=-5.1 EndZ=0
    g6: LineSegment StartX=-1 StartY=-5.1 StartZ=0 EndX=-3 EndY=-5.1 EndZ=0
    g7: LineSegment StartX=-3 StartY=-5.1 StartZ=0 EndX=-3 EndY=-3.1 EndZ=0
  constraints (20):
    c: Horizontal(g0)
    c: Coincident(g1,g0)
    c: Coincident(g2,g1)
    c: Horizontal(g2)
    c: Coincident(g3,g2)
    c: Coincident(g3,g0)
    c: Vertical(g3)
    c: Horizontal(g4)
    c: Coincident(g5,g4)
    c: Coincident(g6,g5)
    c: Horizontal(g6)
    c: Coincident(g7,g6)
    c: Coincident(g7,g4)
    c: Vertical(g7)
    c: Coincident(g0,g-4)
    c: Coincident(g1,g-5)
    c: Coincident(g4,g-6)
    c: Coincident(g5,g-7)
    c: Distance(g0) = 2
    c: Distance(g4) = 2
FEATURE [Sketcher::SketchObject] Sketch066  label="piano per rampino"
  ArcFitTolerance = 1e-06
  AttachmentSupport = -> [XZ_Plane002]
  ExternalGeometry = -> [Sketch045]
  FullyConstrained = true
  MakeInternals = false
  MapMode = 5
  Placement = pos=(0,0,0) rot=(1,0,0;1.5708rad)
  sketch-geometry (4):
    g0: LineSegment StartX=5.4 StartY=5.1 StartZ=0 EndX=5.4 EndY=3.9 EndZ=0
    g1: LineSegment StartX=5.4 StartY=3.9 StartZ=0 EndX=7 EndY=3.9 EndZ=0
    g2: LineSegment StartX=7 StartY=3.9 StartZ=0 EndX=7 EndY=5.1 EndZ=0
    g3: LineSegment StartX=7 StartY=5.1 StartZ=0 EndX=5.4 EndY=5.1 EndZ=0
  constraints (11):
    c: Coincident(g0,g1)
    c: Coincident(g1,g2)
    c: Coincident(g2,g3)
    c: Coincident(g3,g0)
    c: Vertical(g0)
    c: Vertical(g2)
    c: Horizontal(g1)
    c: Horizontal(g3)
    c: Distance(g0,g2) = 1.6
    c: Distance(g1,g3) = 1.2
    c: Coincident(g2,g-3)
FEATURE [Sketcher::SketchObject] Sketch064  label="rampini_per_serraggio_struttura"
  ArcFitTolerance = 1e-06
  AttachmentSupport = -> [XZ_Plane002]
  ExternalGeometry = -> [Sketch066,Sketch045]
  FullyConstrained = true
  MakeInternals = false
  MapMode = 5
  Placement = pos=(0,0,0) rot=(1,0,0;1.5708rad)
  sketch-geometry (7):
    g0: LineSegment StartX=7 StartY=5.1 StartZ=0 EndX=7 EndY=3.9 EndZ=0
    g1: LineSegment StartX=7 StartY=3.9 StartZ=0 EndX=9 EndY=3.9 EndZ=0
    g2: LineSegment StartX=7 StartY=5.1 StartZ=0 EndX=7 EndY=5.1 EndZ=0
    g3: LineSegment StartX=7 StartY=5.1 StartZ=0 EndX=7 EndY=7.5 EndZ=0
    g4: LineSegment StartX=9 StartY=5.1 StartZ=0 EndX=9 EndY=3.9 EndZ=0
    g5: LineSegment StartX=7 StartY=7.5 StartZ=0 EndX=9 EndY=7.5 EndZ=0
    g6: LineSegment StartX=9 StartY=7.5 StartZ=0 EndX=9 EndY=5.1 EndZ=0
  constraints (20):
    c: Vertical(g0)
    c: Coincident(g1,g0)
    c: Horizontal(g1)
    c: Coincident(g2,g0)
    c: Horizontal(g2)
    c: Coincident(g3,g2)
    c: Vertical(g3)
    c: Coincident(g5,g3)
    c: Coincident(g4,g6)
    c: Coincident(g4,g1)
    c: Vertical(g4)
    c: Coincident(g0,g-3)
    c: DistanceY(g-4,g3) = 2.4
    c: DistanceX(g1,g1) = 2
    c: DistanceY(g2,g6) = 0
    c: DistanceX(g2,g2) = 0
    c: DistanceY(g0,g0) = 1.2
    c: Coincident(g5,g6)
    c: Horizontal(g5)
    c: Vertical(g6)
FEATURE [Sketcher::SketchObject] Sketch067  label="perno per blocco switch"
  ArcFitTolerance = 1e-06
  AttachmentSupport = -> [XZ_Plane]
  ExternalGeometry = -> [Sketch,Sketch010]
  FullyConstrained = true
  MakeInternals = false
  MapMode = 5
  Placement = pos=(0,0,0) rot=(1,0,0;1.5708rad)
  sketch-geometry (14):
    g0: LineSegment StartX=-191.073 StartY=24.9429 StartZ=0 EndX=-185.81 EndY=23.0276 EndZ=0
    g1: LineSegment StartX=-183.76 StartY=23.9839 StartZ=0 EndX=-182.392 EndY=27.7427 EndZ=0
    g2: LineSegment StartX=-183.348 StartY=29.7934 StartZ=0 EndX=-188.61 EndY=31.7087 EndZ=0
    g3: LineSegment StartX=-188.61 StartY=31.7087 StartZ=0 EndX=-191.073 EndY=24.9429 EndZ=0
    g4: GeomPoint [constr] X=-186.459 Y=27.0946 Z=0
    g5: LineSegment StartX=-189.022 StartY=25.8992 StartZ=0 EndX=-185.263 EndY=24.5311 EndZ=0
    g6: LineSegment StartX=-185.263 StartY=24.5311 StartZ=0 EndX=-183.895 EndY=28.2899 EndZ=0
    g7: LineSegment StartX=-183.895 StartY=28.2899 StartZ=0 EndX=-187.654 EndY=29.658 EndZ=0
    g8: LineSegment StartX=-187.654 StartY=29.658 StartZ=0 EndX=-189.022 EndY=25.8992 EndZ=0
    g9: GeomPoint [constr] X=-186.459 Y=27.0946 Z=0
    g10: ArcOfCircle CenterX=-185.263 CenterY=24.5311 CenterZ=0 NormalX=0 NormalY=0 NormalZ=1 AngleXU=0 Radius=1.6 StartAngle=4.36332 EndAngle=5.93412
    g11: GeomPoint [constr] X=-184.307 Y=22.4804 Z=0
    g12: ArcOfCircle CenterX=-183.895 CenterY=28.2899 CenterZ=0 NormalX=0 NormalY=0 NormalZ=1 AngleXU=0 Radius=1.6 StartAngle=5.93412 EndAngle=7.50492
    g13: GeomPoint [constr] X=-181.844 Y=29.2462 Z=0
  constraints (30):
    c: Coincident(g2,g3)
    c: Coincident(g3,g0)
    c: Symmetric(g13,g0,g4)
    c: Distance(g11,g3) = 7.2
    c: Distance(g0,g2) = 7.2
    c: Parallel(g3,g1)
    c: Parallel(g2,g0)
    c: Perpendicular(g2,g3)
    c: Coincident(g5,g6)
    c: Coincident(g6,g7)
    c: Coincident(g7,g8)
    c: Coincident(g8,g5)
    c: Symmetric(g7,g5,g9)
    c: Distance(g6,g8) = 4
    c: Distance(g5,g7) = 4
    c: Coincident(g9,g4)
    c: Parallel(g8,g6)
    c: Parallel(g7,g5)
    c: Perpendicular(g7,g8)
    c: Tangent(g8,g-3)
    c: Tangent(g2,g-4)
    c: PointOnObject(g11,g1)
    c: PointOnObject(g11,g0)
    c: Tangent(g1,g10) = -1.5708
    c: Tangent(g0,g10) = -1.5708
    c: PointOnObject(g13,g1)
    c: Tangent(g1,g12) = -1.5708
    c: Tangent(g2,g12) = -1.5708
    c: Equal(g10,g12)
    c: Coincident(g10,g5)
FEATURE [Part::Extrusion] Extrude072  label="Extrude perno per blocco switch"
  Base = -> Sketch067
  Dir = (0,-1,2e-16)
  DirMode = 2
  FaceMakerClass = Part::FaceMakerBullseye
  FaceMakerMode = 3
  LengthFwd = 25.2
  LengthRev = 0
  Solid = true
  Symmetric = true
FEATURE [Part::MultiFuse] Fusion
  Refine = true
  Shapes = -> [Extrude,Sweep,Extrude007,Extrude011,Extrude005,Extrude012,Extrude013,Extrude016,Extrude031,Extrude039,Extrude045,Extrude072]
FEATURE [Part::Cut] Cut
  Base = -> Fusion
  Refine = true
  Tool = -> Extrude001
FEATURE [Part::Cut] Cut001
  Base = -> Cut
  Refine = true
  Tool = -> Extrude004
FEATURE [Part::Cut] Cut002
  Base = -> Cut001
  Refine = true
  Tool = -> Extrude006
FEATURE [Part::Cut] Cut003
  Base = -> Cut002
  Refine = true
  Tool = -> Extrude008
FEATURE [Part::Cut] Cut004
  Base = -> Cut003
  Refine = true
  Tool = -> Extrude009
FEATURE [Part::Cut] Cut005
  Base = -> Cut004
  Refine = true
  Tool = -> Extrude010
FEATURE [Part::Cut] Cut006
  Base = -> Cut005
  Refine = true
  Tool = -> Extrude014
FEATURE [Part::Cut] Cut007
  Base = -> Cut006
  Refine = true
  Tool = -> Extrude015
FEATURE [Part::Cut] Cut008
  Base = -> Cut007
  Refine = true
  Tool = -> Extrude018
FEATURE [Part::Cut] Cut009
  Base = -> Cut008
  Refine = true
  Tool = -> Extrude019
FEATURE [Part::Cut] Cut010
  Base = -> Cut009
  Refine = true
  Tool = -> Extrude020
FEATURE [Part::Cut] Cut011
  Base = -> Cut010
  Refine = true
  Tool = -> Extrude021
FEATURE [Part::Cut] Cut012
  Base = -> Cut011
  Refine = true
  Tool = -> Extrude022
FEATURE [Part::Cut] Cut013
  Base = -> Cut012
  Refine = true
  Tool = -> Extrude023
FEATURE [Part::Cut] Cut014
  Base = -> Cut013
  Refine = true
  Tool = -> Extrude032
FEATURE [Part::Cut] Cut015
  Base = -> Cut014
  Refine = true
  Tool = -> Extrude033
FEATURE [Part::Cut] Cut016
  Base = -> Cut015
  Refine = true
  Tool = -> Extrude034
FEATURE [Part::Cut] Cut017
  Base = -> Cut016
  Refine = true
  Tool = -> Extrude035
FEATURE [Part::Cut] Cut018
  Base = -> Cut017
  Refine = true
  Tool = -> Extrude036
FEATURE [Part::Cut] Cut019
  Base = -> Cut018
  Refine = true
  Tool = -> Extrude037
FEATURE [Part::Cut] Cut020
  Base = -> Cut019
  Refine = true
  Tool = -> Extrude030
FEATURE [Part::Cut] Cut022
  Base = -> Cut020
  Refine = true
  Tool = -> Extrude038
FEATURE [Part::Cut] Cut023
  Base = -> Cut022
  Refine = true
  Tool = -> Extrude041
FEATURE [Part::Cut] Cut024
  Base = -> Cut023
  Refine = true
  Tool = -> Extrude040
FEATURE [Part::Cut] Cut025
  Base = -> Cut024
  Refine = true
  Tool = -> Extrude042
FEATURE [Part::Cut] Cut026
  Base = -> Cut025
  Refine = true
  Tool = -> Extrude043
FEATURE [Part::Cut] Cut027
  Base = -> Cut026
  Refine = true
  Tool = -> Extrude044
FEATURE [Part::Cut] Cut028
  Base = -> Cut027
  Refine = true
  Tool = -> Extrude046
FEATURE [Part::Cut] Cut029
  Base = -> Cut028
  Refine = true
  Tool = -> Extrude047
FEATURE [Part::Cut] Cut033
  Base = -> Cut029
  Refine = true
  Tool = -> Extrude055
FEATURE [Part::Cut] Cut034
  Base = -> Cut033
  Refine = true
  Tool = -> Extrude056
FEATURE [Part::Cut] Cut035
  Base = -> Cut034
  Refine = true
  Tool = -> Extrude057
FEATURE [Part::Cut] Cut037
  Base = -> Cut035
  Refine = true
  Tool = -> Extrude060
FEATURE [Part::Cut] Cut038
  Base = -> Cut037
  Refine = true
  Tool = -> Extrude061
FEATURE [Part::Cut] Cut039
  Base = -> Cut038
  Refine = true
  Tool = -> Extrude063
FEATURE [Part::Cut] Cut040
  Base = -> Cut039
  Refine = true
  Tool = -> Extrude064
FEATURE [Part::Cut] Cut041
  Base = -> Cut040
  Refine = true
  Tool = -> Extrude062
FEATURE [Sketcher::SketchObject] Sketch068  label="base con smusso sopra neopixel"
  ArcFitTolerance = 1e-06
  AttachmentSupport = -> [YZ_Plane002]
  FullyConstrained = true
  MakeInternals = false
  MapMode = 5
  Placement = pos=(0,0,0) rot=(0.57735,0.57735,0.57735;2.0944rad)
  sketch-geometry (5):
    g0: LineSegment StartX=-9.5 StartY=-6.1 StartZ=0 EndX=9.5 EndY=-6.1 EndZ=0
    g1: LineSegment StartX=9.5 StartY=-6.1 StartZ=0 EndX=9.5 EndY=6.1 EndZ=0
    g2: LineSegment StartX=9.5 StartY=6.1 StartZ=0 EndX=-9.5 EndY=6.1 EndZ=0
    g3: LineSegment StartX=-9.5 StartY=6.1 StartZ=0 EndX=-9.5 EndY=-6.1 EndZ=0
    g4: GeomPoint [constr] X=0 Y=0 Z=0
  constraints (12):
    c: Coincident(g0,g1)
    c: Coincident(g1,g2)
    c: Coincident(g2,g3)
    c: Coincident(g3,g0)
    c: Horizontal(g0)
    c: Horizontal(g2)
    c: Vertical(g1)
    c: Vertical(g3)
    c: Symmetric(g2,g0,g4)
    c: Distance(g1,g3) = 19
    c: Distance(g0,g2) = 12.2
    c: Coincident(g4,g-1)
FEATURE [Sketcher::SketchObject] Sketch069  label="cilindro minore"
  ArcFitTolerance = 1e-06
  AttachmentSupport = -> [XZ_Plane004]
  FullyConstrained = true
  MakeInternals = false
  MapMode = 5
  Placement = pos=(0,0,0) rot=(1,0,0;1.5708rad)
  sketch-geometry (1):
    g0: Circle CenterX=0 CenterY=0 CenterZ=0 NormalX=0 NormalY=0 NormalZ=1 AngleXU=0 Radius=5.8
  constraints (2):
    c: Diameter(g0) = 11.6
    c: Coincident(g0,g-1)
FEATURE [Sketcher::SketchObject] Sketch070  label="cilindro maggiore"
  ArcFitTolerance = 1e-06
  AttachmentSupport = -> [XZ_Plane004]
  ExternalGeometry = -> [Sketch069]
  FullyConstrained = true
  MakeInternals = false
  MapMode = 5
  Placement = pos=(0,0,0) rot=(1,0,0;1.5708rad)
  sketch-geometry (1):
    g0: Circle CenterX=0 CenterY=0 CenterZ=0 NormalX=0 NormalY=0 NormalZ=1 AngleXU=0 Radius=6.5
  constraints (2):
    c: Coincident(g0,g-1)
    c: Diameter(g0) = 13
FEATURE [Sketcher::SketchObject] Sketch071  label="buco interno"
  ArcFitTolerance = 1e-06
  AttachmentSupport = -> [XZ_Plane004]
  ExternalGeometry = -> [Sketch069]
  FullyConstrained = true
  MakeInternals = false
  MapMode = 5
  Placement = pos=(0,0,0) rot=(1,0,0;1.5708rad)
  sketch-geometry (1):
    g0: Circle CenterX=0 CenterY=0 CenterZ=0 NormalX=0 NormalY=0 NormalZ=1 AngleXU=0 Radius=5
  constraints (2):
    c: Coincident(g0,g-1)
    c: Diameter(g0) = 10
FEATURE [PartDesign::Pad] Pad
  Direction = (0,-1,2e-16)
  Length = 1.2
  Length2 = 10
  Placement = pos=(0,0,0) rot=(1,0,0;1.5708rad)
  Profile = -> Sketch070
  ReferenceAxis = -> Sketch070 [N_Axis]
  Refine = true
  Suppressed = false
  Type = 0
FEATURE [PartDesign::Pad] Pad001
  BaseFeature = -> Pad
  Direction = (0,-1,2e-16)
  Length = 5.6
  Length2 = 10
  Placement = pos=(0,0,0) rot=(1,0,0;1.5708rad)
  Profile = -> Sketch069
  ReferenceAxis = -> Sketch069 [N_Axis]
  Refine = true
  Suppressed = false
  Type = 0
FEATURE [PartDesign::Pocket] Pocket
  BaseFeature = -> Pad001
  Direction = (0,1,-2e-16)
  Length = 7
  Length2 = 5
  Midplane = true
  Placement = pos=(0,0,0) rot=(1,0,0;1.5708rad)
  Profile = -> Sketch071
  ReferenceAxis = -> Sketch071 [N_Axis]
  Refine = true
  Suppressed = false
  Type = 0
FEATURE [PartDesign::Fillet] Fillet
  Base = -> Pocket [Face7]
  BaseFeature = -> Pocket
  Placement = pos=(0,0,0) rot=(1,0,0;1.5708rad)
  Radius = 1
  Refine = true
  SupportTransform = false
  Suppressed = false
  UseAllEdges = false
FEATURE [PartDesign::Body] Body004  label="pulsanti lato sinistro"
  AllowCompound = false
  Group = -> [Sketch069,Sketch070,Sketch071,Pad,Pad001,Pocket,Fillet]
  Origin = -> Origin004
  Tip = -> Fillet
FEATURE [Sketcher::SketchObject] Sketch072  label="buco per saldature e diodo driver solenoide"
  ArcFitTolerance = 1e-06
  AttachmentSupport = -> [XZ_Plane]
  ExternalGeometry = -> [Sketch038]
  FullyConstrained = true
  MakeInternals = false
  MapMode = 5
  Placement = pos=(0,0,0) rot=(1,0,0;1.5708rad)
  sketch-geometry (4):
    g0: LineSegment StartX=-212.269 StartY=-43.9083 StartZ=0 EndX=-207.197 EndY=-33.0326 EndZ=0
    g1: LineSegment StartX=-207.197 StartY=-33.0326 StartZ=0 EndX=-207.56 EndY=-32.8635 EndZ=0
    g2: LineSegment StartX=-207.56 StartY=-32.8635 StartZ=0 EndX=-212.631 EndY=-43.7392 EndZ=0
    g3: LineSegment StartX=-212.631 StartY=-43.7392 StartZ=0 EndX=-212.269 EndY=-43.9083 EndZ=0
  constraints (11):
    c: Coincident(g1,g0)
    c: Coincident(g2,g1)
    c: Coincident(g3,g2)
    c: Coincident(g3,g0)
    c: Parallel(g-3,g0)
    c: Parallel(g0,g2)
    c: Perpendicular(g0,g3)
    c: Perpendicular(g1,g0)
    c: Distance(g3) = 0.4
    c: Distance(g2) = 12
    c: Coincident(g0,g-3)
FEATURE [Part::Extrusion] Extrude074  label="Extrude buco per saldature e diodo driver solenoide"
  Base = -> Sketch072
  Dir = (0,-1,2e-16)
  DirMode = 2
  FaceMakerClass = Part::FaceMakerBullseye
  FaceMakerMode = 3
  LengthFwd = 14.6
  LengthRev = 0
  Solid = true
  Symmetric = true
FEATURE [Part::Cut] Cut042
  Base = -> Cut041
  Refine = true
  Tool = -> Extrude074
FEATURE [Sketcher::SketchObject] Sketch073  label="fori slargati blocco solenoide"
  ArcFitTolerance = 1e-06
  AttachmentSupport = -> [XY_Plane]
  ExternalGeometry = -> [Sketch030]
  FullyConstrained = true
  MakeInternals = false
  MapMode = 5
  sketch-geometry (2):
    g0: Circle CenterX=-152.209 CenterY=6.95 CenterZ=0 NormalX=0 NormalY=0 NormalZ=1 AngleXU=0 Radius=3.7
    g1: Circle CenterX=-130.41 CenterY=-6.95 CenterZ=0 NormalX=0 NormalY=0 NormalZ=1 AngleXU=0 Radius=3.7
  constraints (4):
    c: Diameter(g0) = 7.4
    c: Coincident(g0,g-3)
    c: Diameter(g1) = 7.4
    c: Coincident(g1,g-4)
FEATURE [Part::Extrusion] Extrude075  label="Extrude fori slargati blocco solenoide"
  Base = -> Sketch073
  Dir = (0,0,1)
  DirMode = 2
  FaceMakerClass = Part::FaceMakerBullseye
  FaceMakerMode = 3
  LengthFwd = 1.5
  LengthRev = 0
  Placement = pos=(0,0,36.4) rot=(0,0,1;0rad)
  Solid = true
  Symmetric = false
FEATURE [Part::Cut] Cut043
  Base = -> Cut042
  Refine = true
  Tool = -> Extrude075
FEATURE [Sketcher::SketchObject] Sketch074  label="lato sx pistola"
  ArcFitTolerance = 1e-06
  AttachmentSupport = -> [XZ_Plane]
  ExternalGeometry = -> [Sketch016,Sketch,Sketch058]
  FullyConstrained = true
  MakeInternals = false
  MapMode = 5
  Placement = pos=(0,0,0) rot=(1,0,0;1.5708rad)
  sketch-geometry (37):
    g0: LineSegment StartX=-82.8 StartY=3.2 StartZ=0 EndX=0 EndY=3.2 EndZ=0
    g1: LineSegment StartX=-82.8 StartY=3.2 StartZ=0 EndX=-82.8 EndY=6.2 EndZ=0
    g2: LineSegment [constr] StartX=-107.6 StartY=18 StartZ=0 EndX=-107.6 EndY=20 EndZ=0
    g3: LineSegment [constr] StartX=-132.428 StartY=18 StartZ=0 EndX=-132.428 EndY=20 EndZ=0
    g4: LineSegment StartX=-132.428 StartY=20 StartZ=0 EndX=-107.6 EndY=20 EndZ=0
    g5: ArcOfCircle CenterX=-107.6 CenterY=4 CenterZ=0 NormalX=0 NormalY=0 NormalZ=1 AngleXU=0 Radius=16 StartAngle=0.137937 EndAngle=1.5708
    g6: LineSegment StartX=-82.8 StartY=6.2 StartZ=0 EndX=-91.752 EndY=6.2 EndZ=0
    g7: LineSegment [constr] StartX=-145.743 StartY=8.32624 StartZ=0 EndX=-147.645 EndY=8.94427 EndZ=0
    g8: ArcOfCircle CenterX=-132.428 CenterY=4 CenterZ=0 NormalX=0 NormalY=0 NormalZ=1 AngleXU=0 Radius=16 StartAngle=1.5708 EndAngle=2.82743
    g9: LineSegment StartX=-215.932 StartY=-80.4316 StartZ=0 EndX=-176.685 EndY=-80.4316 EndZ=0
    g10: LineSegment StartX=-147.645 StartY=8.94427 StartZ=0 EndX=-176.685 EndY=-80.4316 EndZ=0
    g11: LineSegment [constr] StartX=-193.988 StartY=-2.33927 StartZ=0 EndX=-192.176 EndY=-3.18451 EndZ=0
    g12: LineSegment [constr] StartX=-217.232 StartY=-52.1862 StartZ=0 EndX=-215.42 EndY=-53.0314 EndZ=0
    g13: LineSegment StartX=-192.176 StartY=-3.18451 StartZ=0 EndX=-215.42 EndY=-53.0314 EndZ=0
    g14: ArcOfCircle CenterX=-184.801 CenterY=-67.3089 CenterZ=0 NormalX=0 NormalY=0 NormalZ=1 AngleXU=0 Radius=33.7833 StartAngle=2.70526 EndAngle=3.54053
    g15: ArcOfCircle CenterX=-207.583 CenterY=4 CenterZ=0 NormalX=0 NormalY=0 NormalZ=1 AngleXU=0 Radius=17 StartAngle=5.84685 EndAngle=7.56663
    g16: LineSegment StartX=-202.765 StartY=20.303 StartZ=0 EndX=-195.887 EndY=39.2 EndZ=0
    g17: LineSegment [constr] StartX=-193.885 StartY=33.0037 StartZ=0 EndX=-197.644 EndY=34.3718 EndZ=0
    g18: LineSegment StartX=-195.887 StartY=39.2 StartZ=0 EndX=0 EndY=39.2 EndZ=0
    g19: LineSegment StartX=0 StartY=3.2 StartZ=0 EndX=0 EndY=39.2 EndZ=0
    g20: LineSegment StartX=-189.939 StartY=31.5672 StartZ=0 EndX=-192.333 EndY=24.9893 EndZ=0
    g21: LineSegment StartX=-196.467 StartY=26.4942 StartZ=0 EndX=-194.073 EndY=33.0721 EndZ=0
    g22: Circle CenterX=-213.443 CenterY=-76.8316 CenterZ=0 NormalX=0 NormalY=0 NormalZ=1 AngleXU=0 Radius=1.8
    g23: Circle CenterX=-179.305 CenterY=-76.8316 CenterZ=0 NormalX=0 NormalY=0 NormalZ=1 AngleXU=0 Radius=1.8
    g24: Circle CenterX=-184.08 CenterY=34.8 CenterZ=0 NormalX=0 NormalY=0 NormalZ=1 AngleXU=0 Radius=1.8
    g25: Circle CenterX=-78.51 CenterY=34.8 CenterZ=0 NormalX=0 NormalY=0 NormalZ=1 AngleXU=0 Radius=1.8
    g26: Circle CenterX=-78.51 CenterY=7.6 CenterZ=0 NormalX=0 NormalY=0 NormalZ=1 AngleXU=0 Radius=1.8
    g27: Circle CenterX=-5.6 CenterY=34.8 CenterZ=0 NormalX=0 NormalY=0 NormalZ=1 AngleXU=0 Radius=1.8
    g28: Circle CenterX=-5.6 CenterY=7.6 CenterZ=0 NormalX=0 NormalY=0 NormalZ=1 AngleXU=0 Radius=1.8
    g29: LineSegment StartX=-190.127 StartY=31.6356 StartZ=0 EndX=-189.939 EndY=31.5672 EndZ=0
    g30: LineSegment StartX=-194.073 StartY=33.0721 StartZ=0 EndX=-193.885 EndY=33.0037 EndZ=0
    g31: LineSegment StartX=-193.885 StartY=33.0037 StartZ=0 EndX=-190.127 EndY=31.6356 EndZ=0
    g32: LineSegment StartX=-196.467 StartY=26.4942 StartZ=0 EndX=-192.333 EndY=24.9893 EndZ=0
    g33: Circle CenterX=-19 CenterY=21.2 CenterZ=0 NormalX=0 NormalY=0 NormalZ=1 AngleXU=0 Radius=6.3
    g34: Circle CenterX=-42 CenterY=21.2 CenterZ=0 NormalX=0 NormalY=0 NormalZ=1 AngleXU=0 Radius=6.3
    g35: Circle CenterX=-65 CenterY=21.2 CenterZ=0 NormalX=0 NormalY=0 NormalZ=1 AngleXU=0 Radius=6.3
    g36: LineSegment [constr] StartX=-4 StartY=21.2 StartZ=0 EndX=-65 EndY=21.2 EndZ=0
  constraints (96):
    c: Coincident(g0,g-41)
    c: Horizontal(g0)
    c: PointOnObject(g0,g-39)
    c: Coincident(g1,g0)
    c: Vertical(g1)
    c: DistanceY(g1,g1) = 3
    c: Coincident(g2,g-17)
    c: Vertical(g2)
    c: Coincident(g3,g-16)
    c: Vertical(g3)
    c: DistanceY(g2,g2) = 2
    c: DistanceY(g3,g3) = 2
    c: Coincident(g4,g3)
    c: Coincident(g4,g2)
    c: Coincident(g5,g-17)
    c: Coincident(g5,g2)
    c: Coincident(g6,g1)
    c: Horizontal(g6)
    c: Coincident(g6,g5)
    c: Coincident(g7,g-15)
    c: Coincident(g8,g7)
    c: Coincident(g8,g3)
    c: Coincident(g8,g-15)
    c: Horizontal(g9)
    c: DistanceY(g-13,g9) = 2
    c: Coincident(g10,g7)
    c: Parallel(g10,g-14)
    c: Coincident(g9,g10)
    c: Distance(g11) = 2
    c: Coincident(g11,g-11)
    c: Perpendicular(g-11,g11)
    c: Distance(g12) = 2
    c: Coincident(g12,g-12)
    c: Perpendicular(g-11,g12)
    c: Coincident(g13,g11)
    c: Coincident(g13,g12)
    c: Coincident(g14,g-32)
    c: Coincident(g14,g12)
    c: Coincident(g14,g9)
    c: Coincident(g15,g-10)
    c: Coincident(g15,g11)
    c: Parallel(g16,g-22)
    c: Distance(g17) = 4
    c: PointOnObject(g17,g16)
    c: Coincident(g15,g16)
    c: Horizontal(g18)
    c: Coincident(g18,g16)
    c: Coincident(g19,g0)
    c: PointOnObject(g19,g-39)
    c: DistanceY(g19,g-36) = 2
    c: Coincident(g18,g19)
    c: Diameter(g22) = 3.6
    c: Coincident(g22,g-9)
    c: Diameter(g23) = 3.6
    c: Coincident(g23,g-8)
    c: Diameter(g24) = 3.6
    c: Diameter(g25) = 3.6
    c: Diameter(g26) = 3.6
    c: Diameter(g27) = 3.6
    c: Diameter(g28) = 3.6
    c: Coincident(g27,g-4)
    c: Coincident(g28,g-3)
    c: Coincident(g25,g-6)
    c: Coincident(g26,g-5)
    c: Coincident(g24,g-7)
    c: Parallel(g20,g-21)
    c: Equal(g20,g-21)
    c: Parallel(g21,g-19)
    c: Equal(g21,g-19)
    c: Distance(g29) = 0.2
    c: Distance(g30) = 0.2
    c: Parallel(g29,g-20)
    c: Parallel(g31,g-20)
    c: Equal(g31,g-20)
    c: Coincident(g30,g31)
    c: Coincident(g31,g29)
    c: Coincident(g29,g-21)
    c: Parallel(g30,g31)
    c: Coincident(g17,g30)
    c: Coincident(g20,g29)
    c: Coincident(g21,g30)
    c: Perpendicular(g16,g17)
    c: Coincident(g32,g21)
    c: Coincident(g32,g20)
    c: Perpendicular(g10,g7)
    c: Diameter(g33) = 12.6
    c: Diameter(g34) = 12.6
    c: Diameter(g35) = 12.6
    c: Horizontal(g36)
    c: PointOnObject(g33,g36)
    c: PointOnObject(g34,g36)
    c: DistanceX(g34,g33) = 23
    c: DistanceX(g35,g34) = 23
    c: DistanceX(g33,g36) = 15
    c: Symmetric(g-24,g-24,g36)
    c: Coincident(g36,g35)
FEATURE [Sketcher::SketchObject] Sketch075  label="lato dx pistola"
  ArcFitTolerance = 1e-06
  AttachmentSupport = -> [XZ_Plane]
  ExternalGeometry = -> [Sketch016,Sketch,Sketch058,Sketch074]
  FullyConstrained = true
  MakeInternals = false
  MapMode = 5
  Placement = pos=(0,0,0) rot=(1,0,0;1.5708rad)
  sketch-geometry (61):
    g0: LineSegment StartX=-82.8 StartY=3.2 StartZ=0 EndX=0 EndY=3.2 EndZ=0
    g1: LineSegment StartX=-82.8 StartY=3.2 StartZ=0 EndX=-82.8 EndY=6.2 EndZ=0
    g2: LineSegment [constr] StartX=-107.6 StartY=18 StartZ=0 EndX=-107.6 EndY=20 EndZ=0
    g3: LineSegment [constr] StartX=-132.428 StartY=18 StartZ=0 EndX=-132.428 EndY=20 EndZ=0
    g4: LineSegment StartX=-132.428 StartY=20 StartZ=0 EndX=-107.6 EndY=20 EndZ=0
    g5: ArcOfCircle CenterX=-107.6 CenterY=4 CenterZ=0 NormalX=0 NormalY=0 NormalZ=1 AngleXU=0 Radius=16 StartAngle=0.137937 EndAngle=1.5708
    g6: LineSegment StartX=-82.8 StartY=6.2 StartZ=0 EndX=-91.752 EndY=6.2 EndZ=0
    g7: LineSegment [constr] StartX=-145.743 StartY=8.32624 StartZ=0 EndX=-147.645 EndY=8.94427 EndZ=0
    g8: ArcOfCircle CenterX=-132.428 CenterY=4 CenterZ=0 NormalX=0 NormalY=0 NormalZ=1 AngleXU=0 Radius=16 StartAngle=1.5708 EndAngle=2.82743
    g9: LineSegment StartX=-215.932 StartY=-80.4316 StartZ=0 EndX=-176.685 EndY=-80.4316 EndZ=0
    g10: LineSegment StartX=-147.645 StartY=8.94427 StartZ=0 EndX=-176.685 EndY=-80.4316 EndZ=0
    g11: LineSegment [constr] StartX=-193.988 StartY=-2.33927 StartZ=0 EndX=-192.176 EndY=-3.18451 EndZ=0
    g12: LineSegment [constr] StartX=-217.232 StartY=-52.1862 StartZ=0 EndX=-215.42 EndY=-53.0314 EndZ=0
    g13: LineSegment StartX=-192.176 StartY=-3.18451 StartZ=0 EndX=-215.42 EndY=-53.0314 EndZ=0
    g14: ArcOfCircle CenterX=-184.801 CenterY=-67.3089 CenterZ=0 NormalX=0 NormalY=0 NormalZ=1 AngleXU=0 Radius=33.7833 StartAngle=2.70526 EndAngle=3.54053
    g15: ArcOfCircle CenterX=-207.583 CenterY=4 CenterZ=0 NormalX=0 NormalY=0 NormalZ=1 AngleXU=0 Radius=17 StartAngle=5.84685 EndAngle=7.56663
    g16: LineSegment StartX=-202.765 StartY=20.303 StartZ=0 EndX=-195.887 EndY=39.2 EndZ=0
    g17: LineSegment [constr] StartX=-193.885 StartY=33.0037 StartZ=0 EndX=-197.644 EndY=34.3718 EndZ=0
    g18: LineSegment StartX=-195.887 StartY=39.2 StartZ=0 EndX=0 EndY=39.2 EndZ=0
    g19: LineSegment StartX=0 StartY=3.2 StartZ=0 EndX=0 EndY=39.2 EndZ=0
    g20: LineSegment StartX=-189.939 StartY=31.5672 StartZ=0 EndX=-192.333 EndY=24.9893 EndZ=0
    g21: LineSegment StartX=-196.467 StartY=26.4942 StartZ=0 EndX=-194.073 EndY=33.0721 EndZ=0
    g22: Circle CenterX=-213.443 CenterY=-76.8316 CenterZ=0 NormalX=0 NormalY=0 NormalZ=1 AngleXU=0 Radius=1.8
    g23: Circle CenterX=-179.305 CenterY=-76.8316 CenterZ=0 NormalX=0 NormalY=0 NormalZ=1 AngleXU=0 Radius=1.8
    g24: Circle CenterX=-184.08 CenterY=34.8 CenterZ=0 NormalX=0 NormalY=0 NormalZ=1 AngleXU=0 Radius=1.8
    g25: Circle CenterX=-78.51 CenterY=34.8 CenterZ=0 NormalX=0 NormalY=0 NormalZ=1 AngleXU=0 Radius=1.8
    g26: Circle CenterX=-78.51 CenterY=7.6 CenterZ=0 NormalX=0 NormalY=0 NormalZ=1 AngleXU=0 Radius=1.8
    g27: Circle CenterX=-5.6 CenterY=34.8 CenterZ=0 NormalX=0 NormalY=0 NormalZ=1 AngleXU=0 Radius=1.8
    g28: Circle CenterX=-5.6 CenterY=7.6 CenterZ=0 NormalX=0 NormalY=0 NormalZ=1 AngleXU=0 Radius=1.8
    g29: LineSegment StartX=-190.127 StartY=31.6356 StartZ=0 EndX=-189.939 EndY=31.5672 EndZ=0
    g30: LineSegment StartX=-194.073 StartY=33.0721 StartZ=0 EndX=-193.885 EndY=33.0037 EndZ=0
    g31: LineSegment StartX=-193.885 StartY=33.0037 StartZ=0 EndX=-190.127 EndY=31.6356 EndZ=0
    g32: LineSegment StartX=-196.467 StartY=26.4942 StartZ=0 EndX=-192.333 EndY=24.9893 EndZ=0
    g33: LineSegment [constr] StartX=-4 StartY=21.2 StartZ=0 EndX=-87.91 EndY=21.2 EndZ=0
    g34: GeomPoint [constr] X=-4 Y=21.2 Z=0
    g35: LineSegment [constr] StartX=-15.2 StartY=33.7 StartZ=0 EndX=-15.2 EndY=8.7 EndZ=0
    g36: LineSegment [constr] StartX=-15.2 StartY=33.7 StartZ=0 EndX=-56.2 EndY=33.7 EndZ=0
    g37: LineSegment [constr] StartX=-15.2 StartY=8.7 StartZ=0 EndX=-56.2 EndY=8.7 EndZ=0
    g38: LineSegment [constr] StartX=-56.2 StartY=33.7 StartZ=0 EndX=-56.2 EndY=8.7 EndZ=0
    g39: Circle CenterX=-18.6 CenterY=30.3 CenterZ=0 NormalX=0 NormalY=0 NormalZ=1 AngleXU=0 Radius=3.4
    g40: Circle CenterX=-18.6 CenterY=12.1 CenterZ=0 NormalX=0 NormalY=0 NormalZ=1 AngleXU=0 Radius=3.4
    g41: Circle CenterX=-43.2 CenterY=30.3 CenterZ=0 NormalX=0 NormalY=0 NormalZ=1 AngleXU=0 Radius=3.4
    g42: Circle CenterX=-43.2 CenterY=12.1 CenterZ=0 NormalX=0 NormalY=0 NormalZ=1 AngleXU=0 Radius=3.4
    g43: LineSegment [constr] StartX=-4 StartY=21.2 StartZ=0 EndX=-15.2 EndY=21.2 EndZ=0
    g44: LineSegment [constr] StartX=-15.2 StartY=21.2 StartZ=0 EndX=-36.2 EndY=21.2 EndZ=0
    g45: LineSegment [constr] StartX=-41.5 StartY=16.2 StartZ=0 EndX=-30.9 EndY=16.2 EndZ=0
    g46: LineSegment [constr] StartX=-30.9 StartY=16.2 StartZ=0 EndX=-30.9 EndY=26.2 EndZ=0
    g47: LineSegment [constr] StartX=-30.9 StartY=26.2 StartZ=0 EndX=-41.5 EndY=26.2 EndZ=0
    g48: LineSegment [constr] StartX=-41.5 StartY=26.2 StartZ=0 EndX=-41.5 EndY=16.2 EndZ=0
    g49: GeomPoint [constr] X=-36.2 Y=21.2 Z=0
    g50: Circle CenterX=-36.2 CenterY=21.2 CenterZ=0 NormalX=0 NormalY=0 NormalZ=1 AngleXU=0 Radius=2.8
    g51: LineSegment [constr] StartX=-24.2 StartY=26.7 StartZ=0 EndX=-24.2 EndY=15.7 EndZ=0
    g52: Circle CenterX=-24.2 CenterY=26.7 CenterZ=0 NormalX=0 NormalY=0 NormalZ=1 AngleXU=0 Radius=3
    g53: Circle CenterX=-24.2 CenterY=15.7 CenterZ=0 NormalX=0 NormalY=0 NormalZ=1 AngleXU=0 Radius=3
    g54: GeomPoint X=-18.6 Y=30.3 Z=0
    g55: GeomPoint X=-18.6 Y=12.1 Z=0
    g56: GeomPoint X=-43.2 Y=12.1 Z=0
    g57: GeomPoint X=-43.2 Y=30.3 Z=0
    g58: Circle CenterX=-65 CenterY=21.2 CenterZ=0 NormalX=0 NormalY=0 NormalZ=1 AngleXU=0 Radius=1.5
    g59: Circle CenterX=-42 CenterY=21.2 CenterZ=0 NormalX=0 NormalY=0 NormalZ=1 AngleXU=0 Radius=1.5
    g60: Circle CenterX=-19 CenterY=21.2 CenterZ=0 NormalX=0 NormalY=0 NormalZ=1 AngleXU=0 Radius=1.5
  constraints (149):
    c: Coincident(g0,g-41)
    c: Horizontal(g0)
    c: PointOnObject(g0,g-39)
    c: Coincident(g1,g0)
    c: Vertical(g1)
    c: DistanceY(g1,g1) = 3
    c: Coincident(g2,g-17)
    c: Vertical(g2)
    c: Coincident(g3,g-16)
    c: Vertical(g3)
    c: DistanceY(g2,g2) = 2
    c: DistanceY(g3,g3) = 2
    c: Coincident(g4,g3)
    c: Coincident(g4,g2)
    c: Coincident(g5,g-17)
    c: Coincident(g5,g2)
    c: Coincident(g6,g1)
    c: Horizontal(g6)
    c: Coincident(g6,g5)
    c: Coincident(g7,g-15)
    c: Coincident(g8,g7)
    c: Coincident(g8,g3)
    c: Coincident(g8,g-15)
    c: Horizontal(g9)
    c: DistanceY(g-13,g9) = 2
    c: Coincident(g10,g7)
    c: Parallel(g10,g-14)
    c: Coincident(g9,g10)
    c: Distance(g11) = 2
    c: Coincident(g11,g-11)
    c: Perpendicular(g-11,g11)
    c: Distance(g12) = 2
    c: Coincident(g12,g-12)
    c: Perpendicular(g-11,g12)
    c: Coincident(g13,g11)
    c: Coincident(g13,g12)
    c: Coincident(g14,g-32)
    c: Coincident(g14,g12)
    c: Coincident(g14,g9)
    c: Coincident(g15,g-10)
    c: Coincident(g15,g11)
    c: Parallel(g16,g-22)
    c: Distance(g17) = 4
    c: PointOnObject(g17,g16)
    c: Coincident(g15,g16)
    c: Horizontal(g18)
    c: Coincident(g18,g16)
    c: Coincident(g19,g0)
    c: PointOnObject(g19,g-39)
    c: DistanceY(g19,g-36) = 2
    c: Coincident(g18,g19)
    c: Diameter(g22) = 3.6
    c: Coincident(g22,g-9)
    c: Diameter(g23) = 3.6
    c: Coincident(g23,g-8)
    c: Diameter(g24) = 3.6
    c: Diameter(g25) = 3.6
    c: Diameter(g26) = 3.6
    c: Diameter(g27) = 3.6
    c: Diameter(g28) = 3.6
    c: Coincident(g27,g-4)
    c: Coincident(g28,g-3)
    c: Coincident(g25,g-6)
    c: Coincident(g26,g-5)
    c: Coincident(g24,g-7)
    c: Parallel(g20,g-21)
    c: Equal(g20,g-21)
    c: Parallel(g21,g-19)
    c: Equal(g21,g-19)
    c: Distance(g29) = 0.2
    c: Distance(g30) = 0.2
    c: Parallel(g29,g-20)
    c: Parallel(g31,g-20)
    c: Equal(g31,g-20)
    c: Coincident(g30,g31)
    c: Coincident(g31,g29)
    c: Coincident(g29,g-21)
    c: Parallel(g30,g31)
    c: Coincident(g17,g30)
    c: Coincident(g20,g29)
    c: Coincident(g21,g30)
    c: Perpendicular(g16,g17)
    c: Coincident(g32,g21)
    c: Coincident(g32,g20)
    c: Perpendicular(g10,g7)
    c: Horizontal(g33)
    c: Symmetric(g-24,g-24,g33)
    c: PointOnObject(g33,g-28)
    c: Symmetric(g-24,g-24,g34)
    c: DistanceY(g35,g35) = 25
    c: Symmetric(g35,g35,g33)
    c: Distance(g36) = 41
    c: Coincident(g36,g35)
    c: Horizontal(g36)
    c: Coincident(g37,g35)
    c: Horizontal(g37)
    c: Coincident(g38,g36)
    c: Vertical(g38)
    c: Coincident(g37,g38)
    c: Diameter(g39) = 6.8
    c: Diameter(g40) = 6.8
    c: Tangent(g39,g36)
    c: Tangent(g40,g37)
    c: Tangent(g39,g35)
    c: Tangent(g40,g35)
    c: Diameter(g41) = 6.8
    c: Diameter(g42) = 6.8
    c: Tangent(g41,g36)
    c: Tangent(g42,g37)
    c: DistanceX(g41,g39) = 24.6
    c: DistanceX(g42,g40) = 24.6
    c: Distance(g43) = 11.2
    c: Coincident(g43,g33)
    c: PointOnObject(g43,g33)
    c: PointOnObject(g43,g35)
    c: Distance(g44) = 21
    c: Coincident(g44,g43)
    c: PointOnObject(g44,g33)
    c: Coincident(g45,g46)
    c: Coincident(g46,g47)
    c: Coincident(g47,g48)
    c: Coincident(g48,g45)
    c: Horizontal(g45)
    c: Horizontal(g47)
    c: Vertical(g46)
    c: Vertical(g48)
    c: Symmetric(g47,g45,g49)
    c: Distance(g46,g48) = 10.6
    c: Distance(g45,g47) = 10
    c: Coincident(g49,g44)
    c: Diameter(g50) = 5.6
    c: Coincident(g50,g44)
    c: Distance(g51) = 11
    c: Symmetric(g51,g51,g33)
    c: DistanceX(g51,g43) = 9
    c: Diameter(g52) = 6
    c: Coincident(g52,g51)
    c: Diameter(g53) = 6
    c: Coincident(g53,g51)
    c: Coincident(g40,g55)
    c: Coincident(g39,g54)
    c: Coincident(g41,g57)
    c: Coincident(g42,g56)
    c: Diameter(g58) = 3
    c: Diameter(g59) = 3
    c: Diameter(g60) = 3
    c: Coincident(g58,g-44)
    c: Coincident(g59,g-46)
    c: Coincident(g60,g-45)
FEATURE [Sketcher::SketchObject] Sketch078
  ArcFitTolerance = 1e-06
  AttachmentSupport = -> [XZ_Plane005]
  FullyConstrained = true
  MakeInternals = false
  MapMode = 5
  Placement = pos=(0,0,0) rot=(1,0,0;1.5708rad)
  sketch-geometry (5):
    g0: LineSegment [constr] StartX=0 StartY=5.5 StartZ=0 EndX=0 EndY=-5.5 EndZ=0
    g1: ArcOfCircle CenterX=0 CenterY=5.5 CenterZ=0 NormalX=0 NormalY=0 NormalZ=1 AngleXU=0 Radius=2.7 StartAngle=0 EndAngle=3.14159
    g2: ArcOfCircle CenterX=0 CenterY=-5.5 CenterZ=0 NormalX=0 NormalY=0 NormalZ=1 AngleXU=0 Radius=2.7 StartAngle=3.1416 EndAngle=6.28318
    g3: LineSegment StartX=-2.7 StartY=5.5 StartZ=0 EndX=-2.7 EndY=-5.50001 EndZ=0
    g4: LineSegment StartX=2.7 StartY=5.5 StartZ=0 EndX=2.7 EndY=-5.50001 EndZ=0
  constraints (13):
    c: Distance(g0) = 11
    c: Vertical(g0)
    c: Symmetric(g0,g0,g-1)
    c: Radius(g1) = 2.7
    c: Coincident(g1,g0)
    c: Radius(g2) = 2.7
    c: Coincident(g2,g0)
    c: Vertical(g3)
    c: Vertical(g4)
    c: Coincident(g2,g4)
    c: Coincident(g2,g3)
    c: Tangent(g3,g1) = -1.5708
    c: Tangent(g4,g1) = 1.5708
FEATURE [PartDesign::Pad] Pad002
  Direction = (0,-1,2e-16)
  Length = 0.8
  Length2 = 10
  Placement = pos=(0,0,0) rot=(1,0,0;1.5708rad)
  Profile = -> Sketch078
  ReferenceAxis = -> Sketch078 [N_Axis]
  Refine = true
  Suppressed = false
  Type = 0
FEATURE [Sketcher::SketchObject] Sketch079
  ArcFitTolerance = 1e-06
  AttachmentSupport = -> [XZ_Plane005]
  ExternalGeometry = -> [Sketch078]
  FullyConstrained = true
  MakeInternals = false
  MapMode = 5
  Placement = pos=(0,0,0) rot=(1,0,0;1.5708rad)
  sketch-geometry (2):
    g0: Circle CenterX=-1e-16 CenterY=5.5 CenterZ=0 NormalX=0 NormalY=0 NormalZ=1 AngleXU=0 Radius=2.7
    g1: Circle CenterX=0 CenterY=-5.5 CenterZ=0 NormalX=0 NormalY=0 NormalZ=1 AngleXU=0 Radius=2.7
  constraints (4):
    c: Coincident(g0,g-3)
    c: PointOnObject(g-3,g0)
    c: Coincident(g1,g-4)
    c: Equal(g1,g-4)
FEATURE [PartDesign::Pad] Pad003
  BaseFeature = -> Pad002
  Direction = (0,-1,2e-16)
  Length = 5
  Length2 = 10
  Placement = pos=(0,0,0) rot=(1,0,0;1.5708rad)
  Profile = -> Sketch079
  ReferenceAxis = -> Sketch079 [N_Axis]
  Refine = true
  Suppressed = false
  Type = 0
FEATURE [PartDesign::Fillet] Fillet001
  Base = -> Pad003 [Edge16,Edge14]
  BaseFeature = -> Pad003
  Placement = pos=(0,0,0) rot=(1,0,0;1.5708rad)
  Radius = 0.4
  Refine = true
  SupportTransform = false
  Suppressed = false
  UseAllEdges = false
FEATURE [PartDesign::Body] Body005  label="pulsanti lato destro"
  AllowCompound = false
  Group = -> [Sketch078,Pad002,Sketch079,Pad003,Fillet001]
  Origin = -> Origin005
  Tip = -> Fillet001
FEATURE [PartDesign::SubShapeBinder] Binder
  BindCopyOnChange = 0
  BindMode = 0
  ClaimChildren = false
  Context = -> Body006 [Binder.]
  Fuse = false
  MakeFace = true
  OffsetFill = false
  OffsetIntersection = false
  OffsetJoinType = 0
  OffsetOpenResult = false
  PartialLoad = false
  Refine = true
  Relative = true
  Support = -> [Body[Sketch074.]]
  _Version = 2
FEATURE [PartDesign::SubShapeBinder] Binder001
  BindCopyOnChange = 0
  BindMode = 0
  ClaimChildren = false
  Context = -> Body007 [Binder001.]
  Fuse = false
  MakeFace = true
  OffsetFill = false
  OffsetIntersection = false
  OffsetJoinType = 0
  OffsetOpenResult = false
  PartialLoad = false
  Refine = true
  Relative = true
  Support = -> [Body[Sketch075.]]
  _Version = 2
FEATURE [Mesh::Feature] logo_per_PCB_definitivo_positivo
  Placement = pos=(-191,17,-66) rot=(0,1,1;0rad)
FEATURE [Sketcher::SketchObject] Sketch114  label="Sketch114 - base lato DX"
  ArcFitTolerance = 1e-06
  AttachmentSupport = -> [Binder001]
  ExternalGeometry = -> [Binder001]
  FullyConstrained = true
  MakeInternals = false
  MapMode = 5
  Placement = pos=(0,1e-15,0) rot=(0,0.707107,0.707107;3.14159rad)
  sketch-geometry (30):
    g0: Circle CenterX=5.6 CenterY=34.8 CenterZ=0 NormalX=0 NormalY=0 NormalZ=1 AngleXU=0 Radius=1.8
    g1: Circle CenterX=5.6 CenterY=7.6 CenterZ=0 NormalX=0 NormalY=0 NormalZ=1 AngleXU=0 Radius=1.8
    g2: Circle CenterX=24.2 CenterY=26.7 CenterZ=0 NormalX=0 NormalY=0 NormalZ=1 AngleXU=0 Radius=3
    g3: Circle CenterX=24.2 CenterY=15.7 CenterZ=0 NormalX=0 NormalY=0 NormalZ=1 AngleXU=0 Radius=3
    g4: Circle CenterX=36.2 CenterY=21.2 CenterZ=0 NormalX=0 NormalY=0 NormalZ=1 AngleXU=0 Radius=2.8
    g5: Circle CenterX=78.51 CenterY=34.8 CenterZ=0 NormalX=0 NormalY=0 NormalZ=1 AngleXU=0 Radius=1.8
    g6: Circle CenterX=78.51 CenterY=7.6 CenterZ=0 NormalX=0 NormalY=0 NormalZ=1 AngleXU=0 Radius=1.8
    g7: Circle CenterX=184.08 CenterY=34.8 CenterZ=0 NormalX=0 NormalY=0 NormalZ=1 AngleXU=0 Radius=1.8
    g8: Circle CenterX=213.443 CenterY=-76.8316 CenterZ=0 NormalX=0 NormalY=0 NormalZ=1 AngleXU=0 Radius=1.8
    g9: Circle CenterX=179.305 CenterY=-76.8316 CenterZ=0 NormalX=0 NormalY=0 NormalZ=1 AngleXU=0 Radius=1.8
    g10: ArcOfCircle [constr] CenterX=132.428 CenterY=4 CenterZ=0 NormalX=0 NormalY=0 NormalZ=1 AngleXU=0 Radius=16 StartAngle=0.314159 EndAngle=1.5708
    g11: ArcOfCircle CenterX=107.6 CenterY=4 CenterZ=0 NormalX=0 NormalY=0 NormalZ=1 AngleXU=0 Radius=16 StartAngle=1.5708 EndAngle=3.00366
    g12: ArcOfCircle CenterX=207.583 CenterY=4 CenterZ=0 NormalX=0 NormalY=0 NormalZ=1 AngleXU=0 Radius=17 StartAngle=1.85815 EndAngle=3.57792
    g13: ArcOfCircle CenterX=184.801 CenterY=-67.3089 CenterZ=0 NormalX=0 NormalY=0 NormalZ=1 AngleXU=0 Radius=33.7833 StartAngle=5.88425 EndAngle=6.71952
    g14: LineSegment StartX=0 StartY=39.2 StartZ=0 EndX=0 EndY=3.2 EndZ=0
    g15: LineSegment StartX=0 StartY=3.2 StartZ=0 EndX=82.8 EndY=3.2 EndZ=0
    g16: LineSegment StartX=82.8 StartY=3.2 StartZ=0 EndX=82.8 EndY=6.2 EndZ=0
    g17: LineSegment StartX=82.8 StartY=6.2 StartZ=0 EndX=91.752 EndY=6.2 EndZ=0
    g18: LineSegment StartX=107.6 StartY=20 StartZ=0 EndX=132.428 EndY=20 EndZ=0
    g19: LineSegment StartX=147.645 StartY=8.94427 StartZ=0 EndX=176.685 EndY=-80.4316 EndZ=0
    g20: LineSegment StartX=176.685 StartY=-80.4316 StartZ=0 EndX=215.932 EndY=-80.4316 EndZ=0
    g21: LineSegment StartX=215.42 StartY=-53.0314 StartZ=0 EndX=192.176 EndY=-3.18451 EndZ=0
    g22: LineSegment StartX=202.765 StartY=20.303 StartZ=0 EndX=195.887 EndY=39.2 EndZ=0
    g23: LineSegment StartX=195.887 StartY=39.2 StartZ=0 EndX=0 EndY=39.2 EndZ=0
    g24: LineSegment StartX=196.467 StartY=26.4942 StartZ=0 EndX=194.073 EndY=33.0721 EndZ=0
    g25: LineSegment StartX=194.073 StartY=33.0721 StartZ=0 EndX=189.939 EndY=31.5672 EndZ=0
    g26: LineSegment StartX=189.939 StartY=31.5672 StartZ=0 EndX=192.333 EndY=24.9893 EndZ=0
    g27: LineSegment StartX=192.333 StartY=24.9893 StartZ=0 EndX=196.467 EndY=26.4942 EndZ=0
    g28: LineSegment StartX=132.428 StartY=20 StartZ=0 EndX=144.053 EndY=20 EndZ=0
    g29: LineSegment StartX=144.053 StartY=20 StartZ=0 EndX=147.645 EndY=8.94427 EndZ=0
  constraints (65):
    c: Equal(g0,g-25)
    c: Equal(g2,g-29)
    c: Equal(g3,g-30)
    c: Equal(g4,g-28)
    c: Equal(g1,g-26)
    c: Coincident(g0,g-25)
    c: Coincident(g1,g-26)
    c: Coincident(g2,g-29)
    c: Coincident(g3,g-30)
    c: Coincident(g4,g-28)
    c: Equal(g5,g-23)
    c: Equal(g6,g-24)
    c: Coincident(g5,g-23)
    c: Coincident(g6,g-24)
    c: Equal(g7,g-20)
    c: Coincident(g7,g-20)
    c: Equal(g9,g-22)
    c: Coincident(g9,g-22)
    c: Equal(g8,g-21)
    c: Coincident(g8,g-21)
    c: Equal(g13,g-12)
    c: Equal(g12,g-14)
    c: Equal(g10,g-9)
    c: Equal(g11,g-7)
    c: Coincident(g14,g-27)
    c: Coincident(g14,g-27)
    c: Coincident(g15,g14)
    c: Coincident(g15,g-5)
    c: Coincident(g16,g15)
    c: Coincident(g16,g-6)
    c: Coincident(g17,g16)
    c: Coincident(g17,g-7)
    c: Coincident(g11,g17)
    c: Coincident(g11,g-8)
    c: Coincident(g18,g11)
    c: Coincident(g18,g-9)
    c: Coincident(g10,g18)
    c: Coincident(g10,g-10)
    c: Coincident(g19,g10)
    c: Coincident(g19,g-11)
    c: Coincident(g20,g19)
    c: Coincident(g20,g-12)
    c: Coincident(g13,g20)
    c: Coincident(g13,g-13)
    c: Coincident(g21,g13)
    c: Coincident(g21,g-14)
    c: Coincident(g12,g21)
    c: Coincident(g12,g-15)
    c: Coincident(g22,g12)
    c: Coincident(g22,g-15)
    c: Coincident(g23,g22)
    c: Coincident(g23,g14)
    c: Coincident(g24,g-18)
    c: Coincident(g24,g-16)
    c: Coincident(g25,g24)
    c: Coincident(g25,g-19)
    c: Coincident(g26,g25)
    c: Coincident(g26,g-19)
    c: Coincident(g27,g26)
    c: Coincident(g27,g24)
    c: Coincident(g29,g10)
    c: Coincident(g28,g10)
    c: Coincident(g29,g28)
    c: Parallel(g28,g18)
    c: Parallel(g29,g19)
FEATURE [PartDesign::Pad] Pad011
  Direction = (0,1,-2e-16)
  Length = 2
  Length2 = 10
  Profile = -> Sketch114
  ReferenceAxis = -> Sketch114 [N_Axis]
  Refine = true
  Reversed = true
  Suppressed = false
  Type = 0
FEATURE [Sketcher::SketchObject] Sketch115
  ArcFitTolerance = 1e-06
  AttachmentSupport = -> [Pad011]
  ExternalGeometry = -> [Binder001]
  FullyConstrained = true
  MakeInternals = false
  MapMode = 5
  Placement = pos=(0,1.7e-15,0) rot=(0,0.707107,0.707107;3.14159rad)
  sketch-geometry (4):
    g0: ArcOfCircle CenterX=24.2 CenterY=26.7 CenterZ=0 NormalX=0 NormalY=0 NormalZ=1 AngleXU=0 Radius=3 StartAngle=4.48384e-08 EndAngle=3.14159
    g1: ArcOfCircle CenterX=24.2 CenterY=15.7 CenterZ=0 NormalX=0 NormalY=0 NormalZ=1 AngleXU=0 Radius=3 StartAngle=3.14159 EndAngle=6.28318
    g2: LineSegment StartX=21.2 StartY=26.7 StartZ=0 EndX=21.2 EndY=15.7 EndZ=0
    g3: LineSegment StartX=27.2 StartY=26.7 StartZ=0 EndX=27.2 EndY=15.7 EndZ=0
  constraints (12):
    c: Equal(g1,g-4)
    c: Equal(g0,g-3)
    c: Coincident(g0,g-3)
    c: Coincident(g1,g-4)
    c: Vertical(g2)
    c: Vertical(g3)
    c: Tangent(g3,g-3)
    c: Tangent(g2,g-3)
    c: Coincident(g0,g2)
    c: Coincident(g0,g3)
    c: Coincident(g1,g2)
    c: Coincident(g3,g1)
FEATURE [Sketcher::SketchObject] Sketch117  label="Sketch117 - fori per inserto M3 x 3 x 4.5"
  ArcFitTolerance = 1e-06
  AttachmentSupport = -> [Pad011]
  ExternalGeometry = -> [Binder001]
  FullyConstrained = true
  MakeInternals = false
  MapMode = 5
  Placement = pos=(0,1.7e-15,0) rot=(0,0.707107,0.707107;3.14159rad)
  sketch-geometry (4):
    g0: Circle CenterX=43.2 CenterY=30.3 CenterZ=0 NormalX=0 NormalY=0 NormalZ=1 AngleXU=0 Radius=2.25
    g1: Circle CenterX=43.2 CenterY=12.1 CenterZ=0 NormalX=0 NormalY=0 NormalZ=1 AngleXU=0 Radius=2.25
    g2: Circle CenterX=18.6 CenterY=30.3 CenterZ=0 NormalX=0 NormalY=0 NormalZ=1 AngleXU=0 Radius=2.25
    g3: Circle CenterX=18.6 CenterY=12.1 CenterZ=0 NormalX=0 NormalY=0 NormalZ=1 AngleXU=0 Radius=2.25
  constraints (8):
    c: Diameter(g0) = 4.5
    c: Diameter(g1) = 4.5
    c: Diameter(g2) = 4.5
    c: Diameter(g3) = 4.5
    c: Coincident(g2,g-3)
    c: Coincident(g3,g-6)
    c: Coincident(g0,g-4)
    c: Coincident(g1,g-5)
FEATURE [Sketcher::SketchObject] Sketch118
  ArcFitTolerance = 1e-06
  AttachmentSupport = -> [Pad011]
  ExternalGeometry = -> [Binder001]
  FullyConstrained = true
  MakeInternals = false
  MapMode = 5
  Placement = pos=(0,-2,0) rot=(1,0,0;1.5708rad)
  sketch-geometry (12):
    g0: Circle CenterX=-78.51 CenterY=34.8 CenterZ=0 NormalX=0 NormalY=0 NormalZ=1 AngleXU=0 Radius=1.8
    g1: Circle CenterX=-78.51 CenterY=7.6 CenterZ=0 NormalX=0 NormalY=0 NormalZ=1 AngleXU=0 Radius=1.8
    g2: Circle CenterX=-5.6 CenterY=34.8 CenterZ=0 NormalX=0 NormalY=0 NormalZ=1 AngleXU=0 Radius=1.8
    g3: Circle CenterX=-5.6 CenterY=7.6 CenterZ=0 NormalX=0 NormalY=0 NormalZ=1 AngleXU=0 Radius=1.8
    g4: LineSegment StartX=0 StartY=39.2 StartZ=0 EndX=0 EndY=3.2 EndZ=0
    g5: LineSegment StartX=0 StartY=3.2 StartZ=0 EndX=-82.8 EndY=3.2 EndZ=0
    g6: LineSegment StartX=-82.8 StartY=3.2 StartZ=0 EndX=-82.8 EndY=39.2 EndZ=0
    g7: LineSegment StartX=-82.8 StartY=39.2 StartZ=0 EndX=0 EndY=39.2 EndZ=0
    g8: ArcOfCircle CenterX=-65 CenterY=21.2 CenterZ=0 NormalX=0 NormalY=0 NormalZ=1 AngleXU=0 Radius=10 StartAngle=1.5708 EndAngle=4.71239
    g9: ArcOfCircle CenterX=-19 CenterY=21.2 CenterZ=0 NormalX=0 NormalY=0 NormalZ=1 AngleXU=0 Radius=10 StartAngle=4.71239 EndAngle=7.85398
    g10: LineSegment StartX=-65 StartY=31.2 StartZ=0 EndX=-19 EndY=31.2 EndZ=0
    g11: LineSegment StartX=-65 StartY=11.2 StartZ=0 EndX=-19 EndY=11.2 EndZ=0
  constraints (25):
    c: Equal(g2,g-5)
    c: Equal(g3,g-7)
    c: Equal(g1,g-6)
    c: Equal(g0,g-4)
    c: Coincident(g0,g-4)
    c: Coincident(g1,g-6)
    c: Coincident(g3,g-7)
    c: Coincident(g2,g-5)
    c: Coincident(g4,g-8)
    c: Coincident(g4,g-9)
    c: Coincident(g5,g4)
    c: Coincident(g5,g-10)
    c: Coincident(g6,g5)
    c: PointOnObject(g6,g-3)
    c: Vertical(g6)
    c: Coincident(g7,g6)
    c: Coincident(g7,g4)
    c: Tangent(g8,g10) = 1.5708
    c: Tangent(g8,g11) = -1.5708
    c: Tangent(g9,g10) = 1.5708
    c: Tangent(g9,g11) = -1.5708
    c: Equal(g8,g9)
    c: Radius(g8) = 10
    c: Coincident(g8,g-11)
    c: Coincident(g9,g-12)
FEATURE [Sketcher::SketchObject] Sketch120
  ArcFitTolerance = 1e-06
  AttachmentSupport = -> [Pad011]
  ExternalGeometry = -> [Binder001]
  FullyConstrained = true
  MakeInternals = false
  MapMode = 5
  Placement = pos=(0,-2,0) rot=(1,0,0;1.5708rad)
  sketch-geometry (4):
    g0: LineSegment StartX=-137.815 StartY=39.2 StartZ=0 EndX=-142.655 EndY=24.303 EndZ=0
    g1: LineSegment StartX=-137.815 StartY=39.2 StartZ=0 EndX=-110.815 EndY=39.2 EndZ=0
    g2: LineSegment StartX=-142.655 StartY=24.303 StartZ=0 EndX=-110.815 EndY=24.303 EndZ=0
    g3: ArcOfCircle CenterX=-92.2534 CenterY=31.7515 CenterZ=0 NormalX=0 NormalY=0 NormalZ=1 AngleXU=0 Radius=20 StartAngle=2.75997 EndAngle=3.52321
  constraints (12):
    c: PointOnObject(g0,g-3)
    c: Coincident(g1,g0)
    c: PointOnObject(g1,g-3)
    c: Coincident(g2,g0)
    c: Horizontal(g2)
    c: Tangent(g0,g-4)
    c: Vertical(g2,g1)
    c: DistanceX(g1,g1) = 27
    c: DistanceY(g-6,g0) = 4
    c: Radius(g3) = 20
    c: Coincident(g3,g1)
    c: Coincident(g3,g2)
FEATURE [Sketcher::SketchObject] Sketch121
  ArcFitTolerance = 1e-06
  AttachmentSupport = -> [Pad011]
  ExternalGeometry = -> [Binder001]
  FullyConstrained = true
  MakeInternals = false
  MapMode = 5
  Placement = pos=(0,-2,0) rot=(1,0,0;1.5708rad)
  sketch-geometry (15):
    g0: LineSegment StartX=-137.815 StartY=39.2 StartZ=0 EndX=-143.955 EndY=20.303 EndZ=0
    g1: LineSegment StartX=-143.955 StartY=20.303 StartZ=0 EndX=-190.141 EndY=20.303 EndZ=0
    g2: LineSegment StartX=-190.141 StartY=20.303 StartZ=0 EndX=-186.139 EndY=31.3 EndZ=0
    g3: LineSegment StartX=-178.754 StartY=39.2 StartZ=0 EndX=-180.791 EndY=33.6029 EndZ=0
    g4: ArcOfCircle CenterX=-184.08 CenterY=34.8 CenterZ=0 NormalX=0 NormalY=0 NormalZ=1 AngleXU=0 Radius=3.5 StartAngle=4.71239 EndAngle=5.93412
    g5: LineSegment StartX=-184.08 StartY=31.3 StartZ=0 EndX=-186.139 EndY=31.3 EndZ=0
    g6: LineSegment StartX=-137.815 StartY=39.2 StartZ=0 EndX=-156.815 EndY=39.2 EndZ=0
    g7: LineSegment StartX=-168.815 StartY=39.2 StartZ=0 EndX=-178.754 EndY=39.2 EndZ=0
    g8: LineSegment StartX=-157.815 StartY=39.2 StartZ=0 EndX=-167.815 EndY=39.2 EndZ=0
    g9: LineSegment StartX=-168.815 StartY=31.2 StartZ=0 EndX=-156.815 EndY=31.2 EndZ=0
    g10: LineSegment StartX=-167.436 StartY=36.2 StartZ=0 EndX=-157.436 EndY=36.2 EndZ=0
    g11: ArcOfCircle CenterX=-176.411 CenterY=35.2 CenterZ=0 NormalX=0 NormalY=0 NormalZ=1 AngleXU=0 Radius=20 StartAngle=6.08183 EndAngle=6.48454
    g12: ArcOfCircle CenterX=-188.411 CenterY=35.2 CenterZ=0 NormalX=0 NormalY=0 NormalZ=1 AngleXU=0 Radius=20 StartAngle=6.08183 EndAngle=6.48454
    g13: ArcOfCircle CenterX=-177.411 CenterY=35.2 CenterZ=0 NormalX=0 NormalY=0 NormalZ=1 AngleXU=0 Radius=20 StartAngle=0.0500209 EndAngle=0.201358
    g14: ArcOfCircle CenterX=-187.411 CenterY=35.2 CenterZ=0 NormalX=0 NormalY=0 NormalZ=1 AngleXU=0 Radius=20 StartAngle=0.0500209 EndAngle=0.201358
  constraints (46):
    c: PointOnObject(g0,g-3)
    c: Tangent(g0,g-5)
    c: Coincident(g1,g0)
    c: Horizontal(g1)
    c: Coincident(g2,g1)
    c: PointOnObject(g3,g-3)
    c: Parallel(g3,g-6)
    c: Parallel(g2,g-6)
    c: Radius(g4) = 3.5
    c: Coincident(g4,g-7)
    c: Tangent(g3,g4) = 1.5708
    c: Horizontal(g5)
    c: Tangent(g5,g4) = 1.5708
    c: DistanceX(g-8,g5) = 3.8
    c: Coincident(g2,g5)
    c: Coincident(g6,g0)
    c: PointOnObject(g6,g-3)
    c: DistanceX(g6,g6) = 19
    c: PointOnObject(g7,g-3)
    c: DistanceX(g7,g6) = 12
    c: Coincident(g7,g3)
    c: PointOnObject(g8,g-3)
    c: PointOnObject(g8,g-3)
    c: DistanceX(g8,g8) = 10
    c: DistanceX(g8,g6) = 1
    c: Horizontal(g9)
    c: Vertical(g7,g9)
    c: Vertical(g6,g9)
    c: DistanceY(g9,g7) = 8
    c: Horizontal(g10)
    c: Equal(g8,g10)
    c: DistanceY(g10,g8) = 3
    c: Radius(g11) = 20
    c: Coincident(g11,g6)
    c: Coincident(g11,g9)
    c: Radius(g12) = 20
    c: Coincident(g12,g7)
    c: Coincident(g12,g9)
    c: Equal(g13,g11)
    c: Coincident(g13,g8)
    c: Coincident(g13,g10)
    c: Horizontal(g13,g11)
    c: Equal(g14,g12)
    c: Coincident(g14,g8)
    c: Coincident(g14,g10)
    c: Horizontal(g1,g-6)
FEATURE [Sketcher::SketchObject] Sketch122
  ArcFitTolerance = 1e-06
  AttachmentSupport = -> [Pad011]
  ExternalGeometry = -> [Binder001]
  FullyConstrained = true
  MakeInternals = false
  MapMode = 5
  Placement = pos=(0,-2,0) rot=(1,0,0;1.5708rad)
  sketch-geometry (8):
    g0: LineSegment StartX=-202.765 StartY=20.303 StartZ=0 EndX=-143.955 EndY=20.303 EndZ=0
    g1: ArcOfCircle CenterX=-184.801 CenterY=-67.3089 CenterZ=0 NormalX=0 NormalY=0 NormalZ=1 AngleXU=0 Radius=33.7833 StartAngle=2.70526 EndAngle=3.54053
    g2: LineSegment StartX=-176.685 StartY=-80.4316 StartZ=0 EndX=-215.932 EndY=-80.4316 EndZ=0
    g3: LineSegment StartX=-215.42 StartY=-53.0315 StartZ=0 EndX=-192.176 EndY=-3.18454 EndZ=0
    g4: ArcOfCircle CenterX=-207.583 CenterY=4 CenterZ=0 NormalX=0 NormalY=0 NormalZ=1 AngleXU=0 Radius=17 StartAngle=5.84685 EndAngle=7.56663
    g5: Circle CenterX=-213.443 CenterY=-76.8316 CenterZ=0 NormalX=0 NormalY=0 NormalZ=1 AngleXU=0 Radius=3
    g6: Circle CenterX=-179.305 CenterY=-76.8316 CenterZ=0 NormalX=0 NormalY=0 NormalZ=1 AngleXU=0 Radius=3
    g7: LineSegment StartX=-143.955 StartY=20.303 StartZ=0 EndX=-176.685 EndY=-80.4316 EndZ=0
  constraints (18):
    c: Coincident(g0,g-6)
    c: Coincident(g1,g-7)
    c: Coincident(g1,g-8)
    c: Coincident(g2,g1)
    c: Tangent(g3,g-5)
    c: Coincident(g4,g-6)
    c: Coincident(g4,g0)
    c: Coincident(g3,g4)
    c: Coincident(g1,g3)
    c: Diameter(g5) = 6
    c: Diameter(g6) = 6
    c: Coincident(g5,g-9)
    c: Coincident(g6,g-10)
    c: Horizontal(g0)
    c: Horizontal(g2)
    c: Coincident(g7,g0)
    c: Coincident(g7,g2)
    c: Tangent(g7,g-4)
FEATURE [Sketcher::SketchObject] Sketch123
  ArcFitTolerance = 1e-06
  AttachmentSupport = -> [Pad011]
  ExternalGeometry = -> [Binder001]
  FullyConstrained = true
  MakeInternals = false
  MapMode = 5
  Placement = pos=(0,-2,0) rot=(1,0,0;1.5708rad)
  sketch-geometry (4):
    g0: LineSegment StartX=-108 StartY=36.8 StartZ=0 EndX=-90 EndY=36.8 EndZ=0
    g1: LineSegment StartX=-108 StartY=36.8 StartZ=0 EndX=-108 EndY=26.8 EndZ=0
    g2: LineSegment StartX=-108 StartY=26.8 StartZ=0 EndX=-90 EndY=26.8 EndZ=0
    g3: ArcOfCircle CenterX=-94 CenterY=31.8 CenterZ=0 NormalX=0 NormalY=0 NormalZ=1 AngleXU=0 Radius=6.40312 StartAngle=5.38713 EndAngle=7.17924
  constraints (13):
    c: Horizontal(g0)
    c: Coincident(g1,g0)
    c: Vertical(g1)
    c: Coincident(g2,g1)
    c: Horizontal(g2)
    c: DistanceX(g0,g0) = 18
    c: DistanceY(g1,g1) = 10
    c: Equal(g0,g2)
    c: DistanceX(g0,g-3) = 90
    c: DistanceY(g0,g-3) = 2.4
    c: Coincident(g3,g0)
    c: Coincident(g3,g2)
    c: DistanceX(g3,g0) = 4
FEATURE [PartDesign::Chamfer] Chamfer014
  Angle = 45
  Base = -> Pad011 [Edge80,Edge4,Edge7]
  BaseFeature = -> Pad011
  ChamferType = 0
  FlipDirection = false
  Refine = true
  Size = 1.9
  Size2 = 1
  SupportTransform = false
  Suppressed = false
  UseAllEdges = false
FEATURE [PartDesign::Pocket] Pocket006
  BaseFeature = -> Chamfer014
  Direction = (0,-1,2e-16)
  Length = 1.2
  Length2 = 5
  Profile = -> Sketch115
  ReferenceAxis = -> Sketch115 [N_Axis]
  Refine = true
  Suppressed = false
  Type = 0
FEATURE [Sketcher::SketchObject] Sketch116  label="Sketch116 - pieno per inserto M3 x 3 x 4,5"
  ArcFitTolerance = 1e-06
  AttachmentSupport = -> [Pocket006]
  ExternalGeometry = -> [Binder001]
  FullyConstrained = true
  MakeInternals = false
  MapMode = 5
  Placement = pos=(0,1.7e-15,0) rot=(0,0.707107,0.707107;3.14159rad)
  sketch-geometry (4):
    g0: Circle CenterX=43.2 CenterY=30.3 CenterZ=0 NormalX=0 NormalY=0 NormalZ=1 AngleXU=0 Radius=3.4
    g1: Circle CenterX=43.2 CenterY=12.1 CenterZ=0 NormalX=0 NormalY=0 NormalZ=1 AngleXU=0 Radius=3.4
    g2: Circle CenterX=18.6 CenterY=30.3 CenterZ=0 NormalX=0 NormalY=0 NormalZ=1 AngleXU=0 Radius=3.4
    g3: Circle CenterX=18.6 CenterY=12.1 CenterZ=0 NormalX=0 NormalY=0 NormalZ=1 AngleXU=0 Radius=3.4
  constraints (8):
    c: Diameter(g0) = 6.8
    c: Diameter(g1) = 6.8
    c: Diameter(g2) = 6.8
    c: Diameter(g3) = 6.8
    c: Coincident(g2,g-3)
    c: Coincident(g0,g-4)
    c: Coincident(g3,g-6)
    c: Coincident(g1,g-5)
FEATURE [PartDesign::Pad] Pad012
  BaseFeature = -> Pocket006
  Direction = (0,1,-2e-16)
  Length = 2.4
  Length2 = 10
  Profile = -> Sketch116
  ReferenceAxis = -> Sketch116 [N_Axis]
  Refine = true
  Suppressed = false
  Type = 0
FEATURE [PartDesign::Pocket] Pocket007
  BaseFeature = -> Pad012
  Direction = (0,-1,2e-16)
  Length = 0.6
  Length2 = 2.4
  Profile = -> Sketch117
  ReferenceAxis = -> Sketch117 [N_Axis]
  Refine = true
  Suppressed = false
  Type = 4
FEATURE [PartDesign::Pad] Pad013
  BaseFeature = -> Pocket007
  Direction = (0,-1,2e-16)
  Length = 1.6
  Length2 = 10
  Profile = -> Sketch118
  ReferenceAxis = -> Sketch118 [N_Axis]
  Refine = true
  Suppressed = false
  Type = 0
FEATURE [Sketcher::SketchObject] Sketch119
  ArcFitTolerance = 1e-06
  AttachmentSupport = -> [Pad013]
  ExternalGeometry = -> [Binder001]
  FullyConstrained = true
  MakeInternals = false
  MapMode = 5
  Placement = pos=(0,-3.6,0) rot=(1,0,0;1.5708rad)
  sketch-geometry (21):
    g0: LineSegment [constr] StartX=-82.8 StartY=3.2 StartZ=0 EndX=-82.8 EndY=39.2 EndZ=0
    g1: ArcOfCircle CenterX=-78.51 CenterY=34.8 CenterZ=0 NormalX=0 NormalY=0 NormalZ=1 AngleXU=0 Radius=3.5 StartAngle=4.71239 EndAngle=6.28319
    g2: ArcOfCircle CenterX=-78.51 CenterY=7.6 CenterZ=0 NormalX=0 NormalY=0 NormalZ=1 AngleXU=0 Radius=3.5 StartAngle=0 EndAngle=1.5708
    g3: ArcOfCircle CenterX=-5.6 CenterY=34.8 CenterZ=0 NormalX=0 NormalY=0 NormalZ=1 AngleXU=0 Radius=3.5 StartAngle=3.14159 EndAngle=4.71239
    g4: ArcOfCircle CenterX=-5.6 CenterY=7.6 CenterZ=0 NormalX=0 NormalY=0 NormalZ=1 AngleXU=0 Radius=3.5 StartAngle=1.5708 EndAngle=3.14159
    g5: LineSegment StartX=0 StartY=39.2 StartZ=0 EndX=0 EndY=31.3 EndZ=0
    g6: LineSegment StartX=0 StartY=39.2 StartZ=0 EndX=-9.1 EndY=39.2 EndZ=0
    g7: LineSegment StartX=0 StartY=3.2 StartZ=0 EndX=0 EndY=11.1 EndZ=0
    g8: LineSegment StartX=0 StartY=3.2 StartZ=0 EndX=-9.1 EndY=3.2 EndZ=0
    g9: LineSegment StartX=-82.8 StartY=3.2 StartZ=0 EndX=-75.01 EndY=3.2 EndZ=0
    g10: LineSegment StartX=-82.8 StartY=3.2 StartZ=0 EndX=-82.8 EndY=11.1 EndZ=0
    g11: LineSegment StartX=-82.8 StartY=39.2 StartZ=0 EndX=-82.8 EndY=31.3 EndZ=0
    g12: LineSegment StartX=-82.8 StartY=39.2 StartZ=0 EndX=-75.01 EndY=39.2 EndZ=0
    g13: LineSegment StartX=-82.8 StartY=31.3 StartZ=0 EndX=-78.51 EndY=31.3 EndZ=0
    g14: LineSegment StartX=-75.01 StartY=39.2 StartZ=0 EndX=-75.01 EndY=34.8 EndZ=0
    g15: LineSegment StartX=-82.8 StartY=11.1 StartZ=0 EndX=-78.51 EndY=11.1 EndZ=0
    g16: LineSegment StartX=-75.01 StartY=3.2 StartZ=0 EndX=-75.01 EndY=7.6 EndZ=0
    g17: LineSegment StartX=-9.1 StartY=39.2 StartZ=0 EndX=-9.1 EndY=34.8 EndZ=0
    g18: LineSegment StartX=0 StartY=31.3 StartZ=0 EndX=-5.6 EndY=31.3 EndZ=0
    g19: LineSegment StartX=0 StartY=11.1 StartZ=0 EndX=-5.6 EndY=11.1 EndZ=0
    g20: LineSegment StartX=-9.1 StartY=3.2 StartZ=0 EndX=-9.1 EndY=7.6 EndZ=0
  constraints (51):
    c: Coincident(g0,g-10)
    c: PointOnObject(g0,g-8)
    c: Vertical(g0)
    c: Coincident(g1,g-3)
    c: Coincident(g2,g-4)
    c: Coincident(g3,g-5)
    c: Coincident(g4,g-6)
    c: Radius(g4) = 3.5
    c: Radius(g3) = 3.5
    c: Radius(g1) = 3.5
    c: Radius(g2) = 3.5
    c: Coincident(g5,g-9)
    c: PointOnObject(g5,g-9)
    c: Coincident(g6,g5)
    c: PointOnObject(g6,g-8)
    c: Coincident(g7,g-9)
    c: PointOnObject(g7,g-9)
    c: Coincident(g8,g7)
    c: PointOnObject(g8,g-7)
    c: Coincident(g9,g0)
    c: PointOnObject(g9,g-7)
    c: Coincident(g10,g0)
    c: PointOnObject(g10,g0)
    c: Coincident(g11,g0)
    c: PointOnObject(g11,g0)
    c: Coincident(g12,g0)
    c: PointOnObject(g12,g-8)
    c: Coincident(g13,g11)
    c: Horizontal(g13)
    c: Coincident(g14,g12)
    c: Vertical(g14)
    c: Coincident(g15,g10)
    c: Horizontal(g15)
    c: Coincident(g16,g9)
    c: Vertical(g16)
    c: Coincident(g17,g6)
    c: Vertical(g17)
    c: Coincident(g18,g5)
    c: Horizontal(g18)
    c: Coincident(g19,g7)
    c: Horizontal(g19)
    c: Coincident(g20,g8)
    c: Vertical(g20)
    c: Tangent(g20,g4) = 1.5708
    c: Tangent(g4,g19) = -1.5708
    c: Tangent(g18,g3) = 1.5708
    c: Tangent(g3,g17) = -1.5708
    c: Tangent(g13,g1) = -1.5708
    c: Tangent(g1,g14) = 1.5708
    c: Tangent(g16,g2) = -1.5708
    c: Tangent(g2,g15) = 1.5708
FEATURE [PartDesign::Pocket] Pocket008
  BaseFeature = -> Pad013
  Direction = (0,1,-2e-16)
  Length = 1.6
  Length2 = 5
  Profile = -> Sketch119
  ReferenceAxis = -> Sketch119 [N_Axis]
  Refine = true
  Suppressed = false
  Type = 0
FEATURE [PartDesign::Pad] Pad017
  BaseFeature = -> Pocket008
  Direction = (0,-1,2e-16)
  Length = 1.6
  Length2 = 10
  Profile = -> Sketch123
  ReferenceAxis = -> Sketch123 [N_Axis]
  Refine = true
  Suppressed = false
  Type = 0
FEATURE [Sketcher::SketchObject] Sketch125
  ArcFitTolerance = 1e-06
  AttachmentSupport = -> [Pad017]
  ExternalGeometry = -> [Pad017]
  FullyConstrained = true
  MakeInternals = false
  MapMode = 5
  Placement = pos=(0,-3.6,8e-16) rot=(1,0,0;1.5708rad)
  sketch-geometry (20):
    g0: LineSegment StartX=-108 StartY=35.8 StartZ=0 EndX=-108 EndY=35 EndZ=0
    g1: LineSegment StartX=-108 StartY=35 StartZ=0 EndX=-97 EndY=35 EndZ=0
    g2: LineSegment StartX=-97 StartY=35 StartZ=0 EndX=-97 EndY=35.8 EndZ=0
    g3: LineSegment StartX=-97 StartY=35.8 StartZ=0 EndX=-108 EndY=35.8 EndZ=0
    g4: LineSegment StartX=-108 StartY=28.6 StartZ=0 EndX=-108 EndY=27.8 EndZ=0
    g5: LineSegment StartX=-108 StartY=27.8 StartZ=0 EndX=-97 EndY=27.8 EndZ=0
    g6: LineSegment StartX=-97 StartY=27.8 StartZ=0 EndX=-97 EndY=28.6 EndZ=0
    g7: LineSegment StartX=-97 StartY=28.6 StartZ=0 EndX=-108 EndY=28.6 EndZ=0
    g8: LineSegment StartX=-108 StartY=30.4 StartZ=0 EndX=-108 EndY=29.6 EndZ=0
    g9: LineSegment StartX=-108 StartY=29.6 StartZ=0 EndX=-97 EndY=29.6 EndZ=0
    g10: LineSegment StartX=-97 StartY=29.6 StartZ=0 EndX=-97 EndY=30.4 EndZ=0
    g11: LineSegment StartX=-97 StartY=30.4 StartZ=0 EndX=-108 EndY=30.4 EndZ=0
    g12: LineSegment StartX=-108 StartY=32.2 StartZ=0 EndX=-108 EndY=31.4 EndZ=0
    g13: LineSegment StartX=-108 StartY=31.4 StartZ=0 EndX=-97 EndY=31.4 EndZ=0
    g14: LineSegment StartX=-97 StartY=31.4 StartZ=0 EndX=-97 EndY=32.2 EndZ=0
    g15: LineSegment StartX=-97 StartY=32.2 StartZ=0 EndX=-108 EndY=32.2 EndZ=0
    g16: LineSegment StartX=-108 StartY=34 StartZ=0 EndX=-108 EndY=33.2 EndZ=0
    g17: LineSegment StartX=-108 StartY=33.2 StartZ=0 EndX=-97 EndY=33.2 EndZ=0
    g18: LineSegment StartX=-97 StartY=33.2 StartZ=0 EndX=-97 EndY=34 EndZ=0
    g19: LineSegment StartX=-97 StartY=34 StartZ=0 EndX=-108 EndY=34 EndZ=0
  constraints (55):
    c: Coincident(g1,g0)
    c: Horizontal(g1)
    c: Coincident(g2,g1)
    c: Vertical(g2)
    c: Coincident(g3,g2)
    c: Horizontal(g3)
    c: Coincident(g3,g0)
    c: DistanceX(g1,g1) = 11
    c: DistanceY(g2,g2) = 0.8
    c: Coincident(g5,g4)
    c: Horizontal(g5)
    c: Coincident(g6,g5)
    c: Vertical(g6)
    c: Coincident(g7,g6)
    c: Horizontal(g7)
    c: Coincident(g7,g4)
    c: Coincident(g9,g8)
    c: Horizontal(g9)
    c: Coincident(g10,g9)
    c: Vertical(g10)
    c: Coincident(g11,g10)
    c: Horizontal(g11)
    c: Coincident(g11,g8)
    c: Coincident(g13,g12)
    c: Horizontal(g13)
    c: Coincident(g14,g13)
    c: Vertical(g14)
    c: Coincident(g15,g14)
    c: Horizontal(g15)
    c: Coincident(g15,g12)
    c: Coincident(g17,g16)
    c: Horizontal(g17)
    c: Coincident(g18,g17)
    c: Vertical(g18)
    c: Coincident(g19,g18)
    c: Horizontal(g19)
    c: Coincident(g19,g16)
    c: Equal(g3,g19)
    c: Equal(g3,g15)
    c: Equal(g3,g11)
    c: Equal(g3,g7)
    c: Equal(g2,g18)
    c: Equal(g2,g14)
    c: Equal(g2,g10)
    c: Equal(g2,g6)
    c: DistanceY(g-4,g4) = 1
    c: DistanceY(g4,g8) = 1
    c: DistanceY(g8,g12) = 1
    c: DistanceY(g12,g16) = 1
    c: DistanceY(g16,g0) = 1
    c: Tangent(g0,g-5)
    c: Tangent(g16,g-5)
    c: Tangent(g12,g-5)
    c: Tangent(g8,g-5)
    c: Tangent(g4,g-5)
FEATURE [PartDesign::Chamfer] Chamfer009
  Angle = 45
  Base = -> Pad017 [Edge151,Edge154]
  BaseFeature = -> Pad017
  ChamferType = 1
  FlipDirection = false
  Refine = true
  Size = 1.5
  Size2 = 2.8
  SupportTransform = false
  Suppressed = false
  UseAllEdges = false
FEATURE [PartDesign::Pocket] Pocket009
  BaseFeature = -> Chamfer009
  Direction = (0,1,-2e-16)
  Length = 1
  Length2 = 5
  Profile = -> Sketch125
  ReferenceAxis = -> Sketch125 [N_Axis]
  Refine = true
  Suppressed = false
  Type = 0
FEATURE [PartDesign::Pad] Pad014
  BaseFeature = -> Pocket009
  Direction = (0,-1,2e-16)
  Length = 0.8
  Length2 = 10
  Profile = -> Sketch120
  ReferenceAxis = -> Sketch120 [N_Axis]
  Refine = true
  Suppressed = false
  Type = 0
FEATURE [Sketcher::SketchObject] Sketch124
  ArcFitTolerance = 1e-06
  AttachmentSupport = -> [Pad014]
  ExternalGeometry = -> [Binder001]
  FullyConstrained = true
  MakeInternals = false
  MapMode = 5
  Placement = pos=(0,-2.8,6e-16) rot=(1,0,0;1.5708rad)
  sketch-geometry (4):
    g0: LineSegment StartX=-129 StartY=39.2 StartZ=0 EndX=-131.599 EndY=31.2 EndZ=0
    g1: LineSegment StartX=-118 StartY=39.2 StartZ=0 EndX=-120.599 EndY=31.2 EndZ=0
    g2: LineSegment StartX=-129 StartY=39.2 StartZ=0 EndX=-118 EndY=39.2 EndZ=0
    g3: LineSegment StartX=-120.599 StartY=31.2 StartZ=0 EndX=-131.599 EndY=31.2 EndZ=0
  constraints (12):
    c: PointOnObject(g0,g-3)
    c: PointOnObject(g1,g-3)
    c: Parallel(g-4,g0)
    c: Parallel(g-4,g1)
    c: Coincident(g2,g0)
    c: Coincident(g2,g1)
    c: DistanceX(g2,g2) = 11
    c: DistanceY(g1,g1) = 8
    c: Coincident(g3,g1)
    c: Horizontal(g3)
    c: Coincident(g3,g0)
    c: DistanceX(g1,g-3) = 118
FEATURE [PartDesign::Pad] Pad018
  BaseFeature = -> Pad014
  Direction = (0,-1,2e-16)
  Length = 1.2
  Length2 = 10
  Profile = -> Sketch124
  ReferenceAxis = -> Sketch124 [N_Axis]
  Refine = true
  Suppressed = false
  Type = 0
FEATURE [Sketcher::SketchObject] Sketch126
  ArcFitTolerance = 1e-06
  AttachmentSupport = -> [Pad018]
  ExternalGeometry = -> [Pad018]
  FullyConstrained = true
  MakeInternals = false
  MapMode = 5
  Placement = pos=(0,-4,0) rot=(1,0,0;1.5708rad)
  sketch-geometry (8):
    g0: LineSegment StartX=-129.877 StartY=36.5 StartZ=0 EndX=-130.137 EndY=35.7 EndZ=0
    g1: LineSegment StartX=-130.69 StartY=34 StartZ=0 EndX=-130.95 EndY=33.2 EndZ=0
    g2: LineSegment StartX=-129.877 StartY=36.5 StartZ=0 EndX=-118.877 EndY=36.5 EndZ=0
    g3: LineSegment StartX=-130.137 StartY=35.7 StartZ=0 EndX=-119.137 EndY=35.7 EndZ=0
    g4: LineSegment StartX=-130.69 StartY=34 StartZ=0 EndX=-119.69 EndY=34 EndZ=0
    g5: LineSegment StartX=-130.95 StartY=33.2 StartZ=0 EndX=-119.95 EndY=33.2 EndZ=0
    g6: LineSegment StartX=-118.877 StartY=36.5 StartZ=0 EndX=-119.137 EndY=35.7 EndZ=0
    g7: LineSegment StartX=-119.69 StartY=34 StartZ=0 EndX=-119.95 EndY=33.2 EndZ=0
  constraints (20):
    c: Coincident(g2,g0)
    c: Horizontal(g2)
    c: Coincident(g3,g0)
    c: Horizontal(g3)
    c: Coincident(g4,g1)
    c: Horizontal(g4)
    c: Coincident(g5,g1)
    c: Horizontal(g5)
    c: Coincident(g6,g2)
    c: Coincident(g6,g3)
    c: Coincident(g7,g4)
    c: Coincident(g7,g5)
    c: Tangent(g0,g-4)
    c: Tangent(g6,g-5)
    c: Tangent(g1,g-4)
    c: Tangent(g7,g-5)
    c: DistanceY(g3,g2) = 0.8
    c: DistanceY(g5,g4) = 0.8
    c: DistanceY(g-6,g1) = 2
    c: DistanceY(g-6,g0) = 4.5
FEATURE [PartDesign::Chamfer] Chamfer008
  Angle = 45
  Base = -> Pad018 [Edge257]
  BaseFeature = -> Pad018
  ChamferType = 1
  FlipDirection = false
  Refine = true
  Size = 1
  Size2 = 6
  SupportTransform = false
  Suppressed = false
  UseAllEdges = false
FEATURE [PartDesign::Pocket] Pocket010
  BaseFeature = -> Chamfer008
  Direction = (0,1,-2e-16)
  Length = 1
  Length2 = 5
  Profile = -> Sketch126
  ReferenceAxis = -> Sketch126 [N_Axis]
  Refine = true
  Suppressed = false
  Type = 0
FEATURE [PartDesign::Pad] Pad015
  BaseFeature = -> Pocket010
  Direction = (0,-1,2e-16)
  Length = 2
  Length2 = 10
  Profile = -> Sketch121
  ReferenceAxis = -> Sketch121 [N_Axis]
  Refine = true
  Suppressed = false
  Type = 0
FEATURE [PartDesign::Pad] Pad016
  BaseFeature = -> Pad015
  Direction = (0,-1,2e-16)
  Length = 1.6
  Length2 = 10
  Profile = -> Sketch122
  ReferenceAxis = -> Sketch122 [N_Axis]
  Refine = true
  Suppressed = false
  Type = 0
FEATURE [Sketcher::SketchObject] Sketch129
  ArcFitTolerance = 1e-06
  AttachmentSupport = -> [Pad016]
  ExternalGeometry = -> [Binder001]
  FullyConstrained = true
  MakeInternals = false
  MapMode = 5
  Placement = pos=(0,-3.6,0) rot=(1,0,0;1.5708rad)
  sketch-geometry (12):
    g0: LineSegment [constr] StartX=-192.176 StartY=-3.18451 StartZ=0 EndX=-181.223 EndY=20.303 EndZ=0
    g1: LineSegment [constr] StartX=-202.765 StartY=20.303 StartZ=0 EndX=-181.223 EndY=20.303 EndZ=0
    g2: LineSegment StartX=-202.765 StartY=20.303 StartZ=0 EndX=-181.223 EndY=20.303 EndZ=0
    g3: LineSegment StartX=-192.176 StartY=-3.18451 StartZ=0 EndX=-196.804 EndY=-13.1107 EndZ=0
    g4: ArcOfCircle CenterX=-207.583 CenterY=4 CenterZ=0 NormalX=0 NormalY=0 NormalZ=1 AngleXU=0 Radius=17 StartAngle=5.84685 EndAngle=7.56663
    g5: ArcOfEllipse CenterX=-181.223 CenterY=8.55923 CenterZ=0 NormalX=0 NormalY=0 NormalZ=1 MajorRadius=23.4779 MinorRadius=11.7437 AngleXU=2e-16 StartAngle=4.71239 EndAngle=7.85398
    g6: LineSegment [constr] StartX=-157.745 StartY=8.55923 StartZ=0 EndX=-204.701 EndY=8.55923 EndZ=0
    g7: LineSegment [constr] StartX=-181.223 StartY=20.303 StartZ=0 EndX=-181.223 EndY=-3.18451 EndZ=0
    g8: GeomPoint [constr] X=-160.894 Y=8.55923 Z=0
    g9: GeomPoint [constr] X=-201.553 Y=8.55923 Z=0
    g10: ArcOfCircle CenterX=-181.223 CenterY=-20.3763 CenterZ=0 NormalX=0 NormalY=0 NormalZ=1 AngleXU=0 Radius=17.1918 StartAngle=1.57079 EndAngle=2.70526
    g11: GeomPoint [constr] X=-181.223 Y=-3.18451 Z=0
  constraints (23):
    c: Coincident(g0,g-5)
    c: Coincident(g1,g-6)
    c: Horizontal(g1)
    c: Coincident(g1,g0)
    c: Parallel(g0,g-4)
    c: Coincident(g2,g1)
    c: Coincident(g2,g0)
    c: Coincident(g3,g0)
    c: Equal(g4,g-5)
    c: Coincident(g4,g1)
    c: Coincident(g4,g0)
    c: InternalAlignment(g6-g9 -> g5) x4
    c: Vertical(g5,g0)
    c: Horizontal(g6)
    c: Coincident(g5,g0)
    c: DistanceX(g6,g-3) = 10.1
    c: Tangent(g10,g3) = -1.5708
    c: PointOnObject(g11,g10)
    c: Tangent(g5,g10,g11) = 1.5708
    c: Coincident(g10,g5)
    c: Coincident(g11,g7)
    c: Parallel(g3,g-4)
    c: Horizontal(g5,g0)
FEATURE [Sketcher::SketchObject] Sketch130
  ArcFitTolerance = 1e-06
  AttachmentOffset = pos=(0,0,-1.6) rot=(0,0,1;0rad)
  AttachmentSupport = -> [Pad016]
  ExternalGeometry = -> [Binder001]
  FullyConstrained = true
  MakeInternals = false
  MapMode = 5
  Placement = pos=(0,-2,-4e-16) rot=(1,0,0;1.5708rad)
  sketch-geometry (12):
    g0: LineSegment [constr] StartX=-192.176 StartY=-3.18451 StartZ=0 EndX=-181.223 EndY=20.303 EndZ=0
    g1: LineSegment [constr] StartX=-202.765 StartY=20.303 StartZ=0 EndX=-181.223 EndY=20.303 EndZ=0
    g2: LineSegment StartX=-202.765 StartY=20.303 StartZ=0 EndX=-181.223 EndY=20.303 EndZ=0
    g3: LineSegment StartX=-192.176 StartY=-3.18451 StartZ=0 EndX=-193.827 EndY=-6.72678 EndZ=0
    g4: ArcOfCircle CenterX=-207.583 CenterY=4 CenterZ=0 NormalX=0 NormalY=0 NormalZ=1 AngleXU=0 Radius=17 StartAngle=5.84685 EndAngle=7.56663
    g5: ArcOfEllipse CenterX=-181.223 CenterY=10.803 CenterZ=0 NormalX=0 NormalY=0 NormalZ=1 MajorRadius=14.4779 MinorRadius=9.5 AngleXU=0 StartAngle=4.71239 EndAngle=7.85398
    g6: LineSegment [constr] StartX=-166.745 StartY=10.803 StartZ=0 EndX=-195.701 EndY=10.803 EndZ=0
    g7: LineSegment [constr] StartX=-181.223 StartY=20.303 StartZ=0 EndX=-181.223 EndY=1.30297 EndZ=0
    g8: GeomPoint [constr] X=-170.298 Y=10.803 Z=0
    g9: GeomPoint [constr] X=-192.148 Y=10.803 Z=0
    g10: ArcOfCircle CenterX=-181.223 CenterY=-12.6042 CenterZ=0 NormalX=0 NormalY=0 NormalZ=1 AngleXU=0 Radius=13.9072 StartAngle=1.5708 EndAngle=2.70526
    g11: GeomPoint [constr] X=-181.223 Y=1.30297 Z=0
  constraints (23):
    c: Coincident(g0,g-5)
    c: Coincident(g1,g-6)
    c: Horizontal(g1)
    c: Coincident(g1,g0)
    c: Parallel(g0,g-4)
    c: Coincident(g2,g1)
    c: Coincident(g2,g0)
    c: Coincident(g3,g0)
    c: Equal(g4,g-5)
    c: Coincident(g4,g1)
    c: Coincident(g4,g0)
    c: InternalAlignment(g6-g9 -> g5) x4
    c: Vertical(g5,g0)
    c: Horizontal(g6)
    c: Coincident(g5,g0)
    c: DistanceX(g6,g-3) = 19.1
    c: Tangent(g10,g3) = -1.5708
    c: PointOnObject(g11,g10)
    c: Tangent(g5,g10,g11) = 1.5708
    c: Coincident(g10,g5)
    c: Coincident(g11,g7)
    c: Parallel(g3,g-4)
    c: DistanceY(g5,g0) = 19
FEATURE [Part::Part2DObjectPython] Clone2D001  label="Sketch130 (2D)"  # Draft 2D object (typed FeaturePython)
  Fuse = false
  Objects = -> [Sketch130]
  Placement = pos=(0,-2,-4e-16) rot=(1,0,0;1.5708rad)
  Scale = (1,1,1)
FEATURE [Sketcher::SketchObject] Sketch131
  ArcFitTolerance = 1e-06
  AttachmentOffset = pos=(0,0,-3.5) rot=(0,0,1;0rad)
  AttachmentSupport = -> [Pad016]
  ExternalGeometry = -> [Binder001]
  FullyConstrained = true
  MakeInternals = false
  MapMode = 5
  Placement = pos=(0,-0.1,-8e-16) rot=(1,0,0;1.5708rad)
  sketch-geometry (1):
    g0: GeomPoint X=-197.47 Y=8.55923 Z=0
  constraints (1):
    c: Symmetric(g-6,g-4,g0)
FEATURE [Sketcher::SketchObject] Sketch132
  ArcFitTolerance = 1e-06
  AttachmentSupport = -> [Pad016]
  ExternalGeometry = -> [Binder001]
  FullyConstrained = true
  MakeInternals = false
  MapMode = 5
  Placement = pos=(0,-3.6,0) rot=(1,0,0;1.5708rad)
  sketch-geometry (3):
    g0: LineSegment [constr] StartX=-215.42 StartY=-53.0314 StartZ=0 EndX=-167.782 EndY=-53.0314 EndZ=0
    g1: Circle CenterX=-191.282 CenterY=-53.0314 CenterZ=0 NormalX=0 NormalY=0 NormalZ=1 AngleXU=0 Radius=11.5
    g2: Circle CenterX=-191.282 CenterY=-53.0314 CenterZ=0 NormalX=0 NormalY=0 NormalZ=1 AngleXU=0 Radius=10.7
  constraints (8):
    c: Coincident(g0,g-3)
    c: PointOnObject(g0,g-4)
    c: Horizontal(g0)
    c: Diameter(g1) = 23
    c: PointOnObject(g1,g0)
    c: DistanceX(g1,g0) = 23.5
    c: Diameter(g2) = 21.4
    c: Coincident(g2,g1)
FEATURE [Part::Part2DObjectPython] ShapeString  # Draft 2D object (typed FeaturePython)
  FontFile = <path>
  Fuse = false
  Justification = 6
  JustificationReference = 0
  KeepLeftMargin = false
  MakeFace = true
  ObliqueAngle = 0
  Placement = pos=(-199,-3.6,-57.5) rot=(1,0,0;1.5708rad)
  ScaleToSize = true
  Size = 10
  String = AS
  Tracking = 0
FEATURE [Sketcher::SketchObject] Sketch133
  ArcFitTolerance = 1e-06
  AttachmentSupport = -> [Binder]
  ExternalGeometry = -> [Binder]
  FullyConstrained = true
  MakeInternals = false
  MapMode = 5
  Placement = pos=(0,9e-16,0) rot=(0,0.707107,0.707107;3.14159rad)
  sketch-geometry (30):
    g0: LineSegment StartX=0 StartY=39.2 StartZ=0 EndX=0 EndY=3.2 EndZ=0
    g1: LineSegment StartX=0 StartY=3.2 StartZ=0 EndX=82.8 EndY=3.2 EndZ=0
    g2: LineSegment StartX=82.8 StartY=3.2 StartZ=0 EndX=82.8 EndY=6.2 EndZ=0
    g3: LineSegment StartX=82.8 StartY=6.2 StartZ=0 EndX=91.752 EndY=6.2 EndZ=0
    g4: LineSegment StartX=0 StartY=39.2 StartZ=0 EndX=195.887 EndY=39.2 EndZ=0
    g5: LineSegment StartX=195.887 StartY=39.2 StartZ=0 EndX=202.765 EndY=20.303 EndZ=0
    g6: LineSegment StartX=192.333 StartY=24.9893 StartZ=0 EndX=196.467 EndY=26.4942 EndZ=0
    g7: LineSegment StartX=196.467 StartY=26.4942 StartZ=0 EndX=194.073 EndY=33.0721 EndZ=0
    g8: LineSegment StartX=194.073 StartY=33.0721 StartZ=0 EndX=189.939 EndY=31.5672 EndZ=0
    g9: LineSegment StartX=189.939 StartY=31.5672 StartZ=0 EndX=192.333 EndY=24.9893 EndZ=0
    g10: ArcOfCircle CenterX=107.6 CenterY=4 CenterZ=0 NormalX=0 NormalY=0 NormalZ=1 AngleXU=0 Radius=16 StartAngle=1.5708 EndAngle=3.00366
    g11: LineSegment StartX=107.6 StartY=20 StartZ=0 EndX=132.428 EndY=20 EndZ=0
    g12: ArcOfCircle [constr] CenterX=132.428 CenterY=4 CenterZ=0 NormalX=0 NormalY=0 NormalZ=1 AngleXU=0 Radius=16 StartAngle=0.314159 EndAngle=1.5708
    g13: LineSegment StartX=147.645 StartY=8.94427 StartZ=0 EndX=176.685 EndY=-80.4316 EndZ=0
    g14: LineSegment StartX=176.685 StartY=-80.4316 StartZ=0 EndX=215.932 EndY=-80.4316 EndZ=0
    g15: ArcOfCircle CenterX=207.583 CenterY=4 CenterZ=0 NormalX=0 NormalY=0 NormalZ=1 AngleXU=0 Radius=17 StartAngle=1.85815 EndAngle=3.57792
    g16: ArcOfCircle CenterX=184.801 CenterY=-67.3089 CenterZ=0 NormalX=0 NormalY=0 NormalZ=1 AngleXU=0 Radius=33.7833 StartAngle=5.88425 EndAngle=6.71952
    g17: LineSegment StartX=192.176 StartY=-3.18451 StartZ=0 EndX=215.42 EndY=-53.0314 EndZ=0
    g18: Circle CenterX=5.6 CenterY=34.8 CenterZ=0 NormalX=0 NormalY=0 NormalZ=1 AngleXU=0 Radius=1.8
    g19: Circle CenterX=5.6 CenterY=7.6 CenterZ=0 NormalX=0 NormalY=0 NormalZ=1 AngleXU=0 Radius=1.8
    g20: Circle CenterX=78.51 CenterY=34.8 CenterZ=0 NormalX=0 NormalY=0 NormalZ=1 AngleXU=0 Radius=1.8
    g21: Circle CenterX=78.51 CenterY=7.6 CenterZ=0 NormalX=0 NormalY=0 NormalZ=1 AngleXU=0 Radius=1.8
    g22: Circle CenterX=184.08 CenterY=34.8 CenterZ=0 NormalX=0 NormalY=0 NormalZ=1 AngleXU=0 Radius=1.8
    g23: Circle CenterX=179.305 CenterY=-76.8316 CenterZ=0 NormalX=0 NormalY=0 NormalZ=1 AngleXU=0 Radius=1.8
    g24: Circle CenterX=213.443 CenterY=-76.8316 CenterZ=0 NormalX=0 NormalY=0 NormalZ=1 AngleXU=0 Radius=1.8
    g25: Circle CenterX=19 CenterY=21.2 CenterZ=0 NormalX=0 NormalY=0 NormalZ=1 AngleXU=0 Radius=6.3
    g26: Circle CenterX=42 CenterY=21.2 CenterZ=0 NormalX=0 NormalY=0 NormalZ=1 AngleXU=0 Radius=6.3
    g27: Circle CenterX=65 CenterY=21.2 CenterZ=0 NormalX=0 NormalY=0 NormalZ=1 AngleXU=0 Radius=6.3
    g28: LineSegment StartX=132.428 StartY=20 StartZ=0 EndX=144.053 EndY=20 EndZ=0
    g29: LineSegment StartX=147.645 StartY=8.94427 StartZ=0 EndX=144.053 EndY=20 EndZ=0
  constraints (65):
    c: Coincident(g0,g-4)
    c: Coincident(g0,g-5)
    c: Coincident(g1,g0)
    c: Coincident(g1,g-6)
    c: Coincident(g2,g1)
    c: Coincident(g2,g-7)
    c: Coincident(g3,g2)
    c: Coincident(g3,g-8)
    c: Coincident(g4,g0)
    c: Coincident(g4,g-16)
    c: Coincident(g5,g4)
    c: Coincident(g5,g-16)
    c: Coincident(g6,g-20)
    c: Coincident(g6,g-21)
    c: Coincident(g7,g6)
    c: Coincident(g7,g-23)
    c: Coincident(g8,g7)
    c: Coincident(g8,g-22)
    c: Coincident(g9,g8)
    c: Coincident(g9,g6)
    c: Equal(g10,g-8)
    c: Coincident(g10,g3)
    c: Coincident(g10,g-9)
    c: Coincident(g11,g10)
    c: Coincident(g11,g-10)
    c: Equal(g12,g-10)
    c: Coincident(g12,g11)
    c: Coincident(g12,g-11)
    c: Coincident(g13,g12)
    c: Coincident(g13,g-12)
    c: Coincident(g14,g13)
    c: Coincident(g14,g-13)
    c: Equal(g15,g-15)
    c: Coincident(g15,g5)
    c: Coincident(g15,g-15)
    c: Equal(g16,g-13)
    c: Coincident(g16,g14)
    c: Coincident(g16,g-14)
    c: Coincident(g17,g15)
    c: Coincident(g17,g16)
    c: Equal(g18,g-28)
    c: Equal(g19,g-29)
    c: Equal(g20,g-26)
    c: Equal(g21,g-27)
    c: Equal(g22,g-17)
    c: Equal(g24,g-25)
    c: Equal(g23,g-24)
    c: Coincident(g23,g-24)
    c: Coincident(g24,g-25)
    c: Coincident(g22,g-17)
    c: Coincident(g20,g-26)
    c: Coincident(g21,g-27)
    c: Coincident(g18,g-28)
    c: Coincident(g19,g-29)
    c: Equal(g25,g-30)
    c: Equal(g26,g-31)
    c: Equal(g27,g-32)
    c: Coincident(g25,g-30)
    c: Coincident(g26,g-31)
    c: Coincident(g27,g-32)
    c: Parallel(g28,g11)
    c: Parallel(g29,g13)
    c: Coincident(g28,g11)
    c: Coincident(g29,g12)
    c: Coincident(g29,g28)
FEATURE [PartDesign::Pad] Pad019
  Direction = (0,1,-2e-16)
  Length = 2
  Length2 = 10
  Profile = -> Sketch133
  ReferenceAxis = -> Sketch133 [N_Axis]
  Refine = true
  Suppressed = false
  Type = 0
FEATURE [Sketcher::SketchObject] Sketch091  label="Sketch091 - forma anteriore"
  ArcFitTolerance = 1e-06
  AttachmentSupport = -> [Pad019]
  ExternalGeometry = -> [Binder]
  FullyConstrained = true
  MakeInternals = false
  MapMode = 5
  Placement = pos=(0,2,0) rot=(0,0.707107,0.707107;3.14159rad)
  sketch-geometry (12):
    g0: Circle CenterX=5.6 CenterY=34.8 CenterZ=0 NormalX=0 NormalY=0 NormalZ=1 AngleXU=0 Radius=1.8
    g1: Circle CenterX=5.6 CenterY=7.6 CenterZ=0 NormalX=0 NormalY=0 NormalZ=1 AngleXU=0 Radius=1.8
    g2: Circle CenterX=78.51 CenterY=34.8 CenterZ=0 NormalX=0 NormalY=0 NormalZ=1 AngleXU=0 Radius=1.8
    g3: Circle CenterX=78.51 CenterY=7.6 CenterZ=0 NormalX=0 NormalY=0 NormalZ=1 AngleXU=0 Radius=1.8
    g4: LineSegment StartX=0 StartY=39.2 StartZ=0 EndX=0 EndY=3.2 EndZ=0
    g5: LineSegment StartX=0 StartY=3.2 StartZ=0 EndX=82.8 EndY=3.2 EndZ=0
    g6: LineSegment StartX=82.8 StartY=3.2 StartZ=0 EndX=82.8 EndY=39.2 EndZ=0
    g7: LineSegment StartX=82.8 StartY=39.2 StartZ=0 EndX=0 EndY=39.2 EndZ=0
    g8: ArcOfCircle CenterX=19 CenterY=21.2 CenterZ=0 NormalX=0 NormalY=0 NormalZ=1 AngleXU=0 Radius=10 StartAngle=1.5708 EndAngle=4.71239
    g9: ArcOfCircle CenterX=65 CenterY=21.2 CenterZ=0 NormalX=0 NormalY=0 NormalZ=1 AngleXU=0 Radius=10 StartAngle=4.71239 EndAngle=7.85398
    g10: LineSegment StartX=19 StartY=31.2 StartZ=0 EndX=65 EndY=31.2 EndZ=0
    g11: LineSegment StartX=19 StartY=11.2 StartZ=0 EndX=65 EndY=11.2 EndZ=0
  constraints (25):
    c: Equal(g2,g-7)
    c: Equal(g3,g-8)
    c: Equal(g1,g-13)
    c: Equal(g0,g-12)
    c: Coincident(g0,g-12)
    c: Coincident(g1,g-13)
    c: Coincident(g3,g-8)
    c: Coincident(g2,g-7)
    c: Coincident(g4,g-4)
    c: Coincident(g4,g-5)
    c: Coincident(g5,g4)
    c: Coincident(g5,g-6)
    c: Coincident(g6,g5)
    c: PointOnObject(g6,g-3)
    c: Vertical(g6)
    c: Coincident(g7,g6)
    c: Coincident(g7,g4)
    c: Tangent(g8,g10) = 1.5708
    c: Tangent(g8,g11) = -1.5708
    c: Tangent(g9,g10) = 1.5708
    c: Tangent(g9,g11) = -1.5708
    c: Equal(g8,g9)
    c: Radius(g8) = 10
    c: Coincident(g8,g-11)
    c: Coincident(g9,g-9)
FEATURE [Sketcher::SketchObject] Sketch093  label="Sketch093 - scavi interni pulsanti"
  ArcFitTolerance = 1e-06
  AttachmentSupport = -> [Pad019]
  ExternalGeometry = -> [Binder]
  FullyConstrained = true
  MakeInternals = false
  MapMode = 5
  Placement = pos=(0,1.8e-15,0) rot=(1,0,0;1.5708rad)
  sketch-geometry (3):
    g0: Circle CenterX=-65 CenterY=21.2 CenterZ=0 NormalX=0 NormalY=0 NormalZ=1 AngleXU=0 Radius=7.3
    g1: Circle CenterX=-42 CenterY=21.2 CenterZ=0 NormalX=0 NormalY=0 NormalZ=1 AngleXU=0 Radius=7.3
    g2: Circle CenterX=-19 CenterY=21.2 CenterZ=0 NormalX=0 NormalY=0 NormalZ=1 AngleXU=0 Radius=7.3
  constraints (6):
    c: Coincident(g0,g-3)
    c: Coincident(g1,g-4)
    c: Coincident(g2,g-5)
    c: Diameter(g0) = 14.6
    c: Diameter(g1) = 14.6
    c: Diameter(g2) = 14.6
FEATURE [Sketcher::SketchObject] Sketch094  label="Sketch094 - forma centrale"
  ArcFitTolerance = 1e-06
  AttachmentSupport = -> [Pad019]
  ExternalGeometry = -> [Binder]
  FullyConstrained = true
  MakeInternals = false
  MapMode = 5
  Placement = pos=(0,2,0) rot=(0,0.707107,0.707107;3.14159rad)
  sketch-geometry (4):
    g0: LineSegment StartX=137.815 StartY=39.2 StartZ=0 EndX=142.655 EndY=24.303 EndZ=0
    g1: LineSegment StartX=110.815 StartY=24.303 StartZ=0 EndX=142.655 EndY=24.303 EndZ=0
    g2: LineSegment StartX=137.815 StartY=39.2 StartZ=0 EndX=110.815 EndY=39.2 EndZ=0
    g3: ArcOfCircle CenterX=92.2534 CenterY=31.7515 CenterZ=0 NormalX=0 NormalY=0 NormalZ=1 AngleXU=0 Radius=20 StartAngle=5.90156 EndAngle=6.66481
  constraints (12):
    c: PointOnObject(g0,g-3)
    c: Tangent(g0,g-5)
    c: Horizontal(g1)
    c: Coincident(g1,g0)
    c: Coincident(g2,g0)
    c: PointOnObject(g2,g-3)
    c: DistanceX(g2,g2) = 27
    c: Vertical(g1,g2)
    c: Coincident(g3,g2)
    c: Radius(g3) = 20
    c: Coincident(g3,g1)
    c: DistanceY(g-6,g0) = 4
FEATURE [Sketcher::SketchObject] Sketch095  label="Sketch095 - forma posteriore"
  ArcFitTolerance = 1e-06
  AttachmentSupport = -> [Pad019]
  ExternalGeometry = -> [Binder]
  FullyConstrained = true
  MakeInternals = false
  MapMode = 5
  Placement = pos=(0,2,0) rot=(0,0.707107,0.707107;3.14159rad)
  sketch-geometry (15):
    g0: LineSegment StartX=137.815 StartY=39.2 StartZ=0 EndX=143.955 EndY=20.303 EndZ=0
    g1: LineSegment StartX=143.955 StartY=20.303 StartZ=0 EndX=190.141 EndY=20.303 EndZ=0
    g2: ArcOfCircle CenterX=184.08 CenterY=34.8 CenterZ=0 NormalX=0 NormalY=0 NormalZ=1 AngleXU=0 Radius=3.5 StartAngle=3.49066 EndAngle=4.71239
    g3: LineSegment StartX=180.791 StartY=33.6029 StartZ=0 EndX=178.754 EndY=39.2 EndZ=0
    g4: LineSegment StartX=184.08 StartY=31.3 StartZ=0 EndX=186.139 EndY=31.3 EndZ=0
    g5: LineSegment StartX=190.141 StartY=20.303 StartZ=0 EndX=186.139 EndY=31.3 EndZ=0
    g6: LineSegment StartX=137.815 StartY=39.2 StartZ=0 EndX=156.815 EndY=39.2 EndZ=0
    g7: LineSegment StartX=178.754 StartY=39.2 StartZ=0 EndX=168.815 EndY=39.2 EndZ=0
    g8: LineSegment StartX=156.815 StartY=31.2 StartZ=0 EndX=168.815 EndY=31.2 EndZ=0
    g9: ArcOfCircle CenterX=176.411 CenterY=35.2 CenterZ=0 NormalX=0 NormalY=0 NormalZ=1 AngleXU=0 Radius=20 StartAngle=2.94023 EndAngle=3.34295
    g10: ArcOfCircle CenterX=188.411 CenterY=35.2 CenterZ=0 NormalX=0 NormalY=0 NormalZ=1 AngleXU=0 Radius=20 StartAngle=2.94023 EndAngle=3.34295
    g11: LineSegment StartX=157.815 StartY=39.2 StartZ=0 EndX=167.815 EndY=39.2 EndZ=0
    g12: LineSegment StartX=157.436 StartY=36.2 StartZ=0 EndX=167.436 EndY=36.2 EndZ=0
    g13: ArcOfCircle CenterX=177.411 CenterY=35.2 CenterZ=0 NormalX=0 NormalY=0 NormalZ=1 AngleXU=0 Radius=20 StartAngle=2.94023 EndAngle=3.09157
    g14: ArcOfCircle CenterX=187.411 CenterY=35.2 CenterZ=0 NormalX=0 NormalY=0 NormalZ=1 AngleXU=0 Radius=20 StartAngle=2.94023 EndAngle=3.09157
  constraints (46):
    c: PointOnObject(g0,g-3)
    c: Tangent(g0,g-6)
    c: Coincident(g1,g0)
    c: Horizontal(g1)
    c: Radius(g2) = 3.5
    c: Coincident(g2,g-5)
    c: PointOnObject(g3,g-3)
    c: Parallel(g3,g-4)
    c: Tangent(g3,g2) = 1.5708
    c: Horizontal(g4)
    c: Tangent(g4,g2) = -1.5708
    c: Coincident(g5,g1)
    c: Parallel(g5,g-4)
    c: Coincident(g5,g4)
    c: DistanceX(g4,g-8) = 3.8
    c: Coincident(g6,g0)
    c: PointOnObject(g6,g-3)
    c: Coincident(g7,g3)
    c: PointOnObject(g7,g-3)
    c: Horizontal(g8)
    c: DistanceX(g6,g7) = 12
    c: Vertical(g8,g6)
    c: Vertical(g7,g8)
    c: DistanceY(g8,g6) = 8
    c: Coincident(g9,g8)
    c: Coincident(g9,g6)
    c: Coincident(g10,g7)
    c: Coincident(g10,g8)
    c: Radius(g9) = 20
    c: Radius(g10) = 20
    c: PointOnObject(g11,g-3)
    c: PointOnObject(g11,g-3)
    c: DistanceX(g11,g11) = 10
    c: DistanceX(g6,g11) = 1
    c: Horizontal(g12)
    c: Equal(g12,g11)
    c: DistanceY(g12,g11) = 3
    c: Coincident(g13,g11)
    c: Coincident(g13,g12)
    c: Radius(g13) = 20
    c: Coincident(g14,g11)
    c: Coincident(g14,g12)
    c: Radius(g14) = 20
    c: DistanceX(g0,g6) = 19
    c: Horizontal(g9,g13)
    c: Horizontal(g0,g-4)
FEATURE [Sketcher::SketchObject] Sketch096  label="Sketch096 - forma impugnatura"
  ArcFitTolerance = 1e-06
  AttachmentSupport = -> [Pad019]
  ExternalGeometry = -> [Binder]
  FullyConstrained = true
  MakeInternals = false
  MapMode = 5
  Placement = pos=(0,2,0) rot=(0,0.707107,0.707107;3.14159rad)
  sketch-geometry (8):
    g0: LineSegment StartX=176.685 StartY=-80.4316 StartZ=0 EndX=143.955 EndY=20.303 EndZ=0
    g1: LineSegment StartX=176.685 StartY=-80.4316 StartZ=0 EndX=215.932 EndY=-80.4316 EndZ=0
    g2: Circle CenterX=179.305 CenterY=-76.8316 CenterZ=0 NormalX=0 NormalY=0 NormalZ=1 AngleXU=0 Radius=3
    g3: Circle CenterX=213.443 CenterY=-76.8316 CenterZ=0 NormalX=0 NormalY=0 NormalZ=1 AngleXU=0 Radius=3
    g4: LineSegment StartX=143.955 StartY=20.303 StartZ=0 EndX=202.765 EndY=20.303 EndZ=0
    g5: LineSegment StartX=215.42 StartY=-53.0314 StartZ=0 EndX=192.176 EndY=-3.18451 EndZ=0
    g6: ArcOfCircle CenterX=184.801 CenterY=-67.3089 CenterZ=0 NormalX=0 NormalY=0 NormalZ=1 AngleXU=0 Radius=33.7833 StartAngle=5.88425 EndAngle=6.71952
    g7: ArcOfCircle CenterX=207.583 CenterY=4 CenterZ=0 NormalX=0 NormalY=0 NormalZ=1 AngleXU=0 Radius=17 StartAngle=1.85815 EndAngle=3.57792
  constraints (19):
    c: Coincident(g0,g-4)
    c: PointOnObject(g0,g-3)
    c: Horizontal(g0,g-7)
    c: Coincident(g1,g0)
    c: Coincident(g1,g-5)
    c: Diameter(g2) = 6
    c: Diameter(g3) = 6
    c: Coincident(g2,g-9)
    c: Coincident(g3,g-10)
    c: Coincident(g4,g0)
    c: Coincident(g5,g-6)
    c: Coincident(g6,g1)
    c: Coincident(g6,g5)
    c: Equal(g-5,g6)
    c: Coincident(g5,g-7)
    c: Coincident(g4,g-7)
    c: Tangent(g7,g-7)
    c: Coincident(g7,g4)
    c: Coincident(g7,g5)
FEATURE [Sketcher::SketchObject] Sketch097
  ArcFitTolerance = 1e-06
  AttachmentSupport = -> [Pad019]
  ExternalGeometry = -> [Binder]
  FullyConstrained = true
  MakeInternals = false
  MapMode = 5
  Placement = pos=(0,2,0) rot=(0,0.707107,0.707107;3.14159rad)
  sketch-geometry (4):
    g0: LineSegment StartX=90 StartY=36.8 StartZ=0 EndX=108 EndY=36.8 EndZ=0
    g1: LineSegment StartX=108 StartY=36.8 StartZ=0 EndX=108 EndY=26.8 EndZ=0
    g2: LineSegment StartX=108 StartY=26.8 StartZ=0 EndX=90 EndY=26.8 EndZ=0
    g3: ArcOfCircle CenterX=94 CenterY=31.8 CenterZ=0 NormalX=0 NormalY=0 NormalZ=1 AngleXU=0 Radius=6.40312 StartAngle=2.24554 EndAngle=4.03765
  constraints (13):
    c: Horizontal(g0)
    c: Coincident(g1,g0)
    c: Vertical(g1)
    c: DistanceX(g0,g0) = 18
    c: DistanceY(g1,g1) = 10
    c: Coincident(g2,g1)
    c: Horizontal(g2)
    c: Equal(g2,g0)
    c: DistanceY(g0,g-3) = 2.4
    c: Coincident(g3,g0)
    c: Coincident(g3,g2)
    c: DistanceX(g2,g3) = 4
    c: DistanceX(g-3,g0) = 90
FEATURE [PartDesign::Chamfer] Chamfer015
  Angle = 45
  Base = -> Pad019 [Edge19,Edge22,Edge79]
  BaseFeature = -> Pad019
  ChamferType = 0
  FlipDirection = false
  Refine = true
  Size = 1.9
  Size2 = 1
  SupportTransform = false
  Suppressed = false
  UseAllEdges = false
FEATURE [PartDesign::Pocket] Pocket002
  BaseFeature = -> Chamfer015
  Direction = (0,1,-2e-16)
  Length = 1.2
  Length2 = 5
  Profile = -> Sketch093
  ReferenceAxis = -> Sketch093 [N_Axis]
  Refine = true
  Suppressed = false
  Type = 0
FEATURE [PartDesign::Pad] Pad005
  BaseFeature = -> Pocket002
  Direction = (0,1,-2e-16)
  Length = 1.6
  Length2 = 10
  Profile = -> Sketch091
  ReferenceAxis = -> Sketch091 [N_Axis]
  Refine = true
  Suppressed = false
  Type = 0
FEATURE [Sketcher::SketchObject] Sketch092  label="Sketch092 - scavi per viti anteriori"
  ArcFitTolerance = 1e-06
  AttachmentSupport = -> [Pad005]
  ExternalGeometry = -> [Binder]
  FullyConstrained = true
  MakeInternals = false
  MapMode = 5
  Placement = pos=(0,3.6,0) rot=(0,0.707107,0.707107;3.14159rad)
  sketch-geometry (20):
    g0: ArcOfCircle CenterX=5.6 CenterY=7.6 CenterZ=0 NormalX=0 NormalY=0 NormalZ=1 AngleXU=0 Radius=3.5 StartAngle=0 EndAngle=1.5708
    g1: ArcOfCircle CenterX=5.6 CenterY=34.8 CenterZ=0 NormalX=0 NormalY=0 NormalZ=1 AngleXU=0 Radius=3.5 StartAngle=4.71239 EndAngle=6.28319
    g2: ArcOfCircle CenterX=78.51 CenterY=34.8 CenterZ=0 NormalX=0 NormalY=0 NormalZ=1 AngleXU=0 Radius=3.5 StartAngle=3.14159 EndAngle=4.71239
    g3: ArcOfCircle CenterX=78.51 CenterY=7.6 CenterZ=0 NormalX=0 NormalY=0 NormalZ=1 AngleXU=0 Radius=3.5 StartAngle=1.5708 EndAngle=3.14159
    g4: LineSegment StartX=0 StartY=3.2 StartZ=0 EndX=0 EndY=11.1 EndZ=0
    g5: LineSegment StartX=0 StartY=11.1 StartZ=0 EndX=5.6 EndY=11.1 EndZ=0
    g6: LineSegment StartX=0 StartY=3.2 StartZ=0 EndX=9.1 EndY=3.2 EndZ=0
    g7: LineSegment StartX=9.1 StartY=3.2 StartZ=0 EndX=9.1 EndY=7.6 EndZ=0
    g8: LineSegment StartX=0 StartY=39.2 StartZ=0 EndX=0 EndY=31.3 EndZ=0
    g9: LineSegment StartX=0 StartY=31.3 StartZ=0 EndX=5.6 EndY=31.3 EndZ=0
    g10: LineSegment StartX=0 StartY=39.2 StartZ=0 EndX=9.1 EndY=39.2 EndZ=0
    g11: LineSegment StartX=9.1 StartY=39.2 StartZ=0 EndX=9.1 EndY=34.8 EndZ=0
    g12: LineSegment StartX=82.8 StartY=39.2 StartZ=0 EndX=75.01 EndY=39.2 EndZ=0
    g13: LineSegment StartX=82.8 StartY=39.2 StartZ=0 EndX=82.8 EndY=31.3 EndZ=0
    g14: LineSegment StartX=82.8 StartY=31.3 StartZ=0 EndX=78.51 EndY=31.3 EndZ=0
    g15: LineSegment StartX=82.8 StartY=3.2 StartZ=0 EndX=75.01 EndY=3.2 EndZ=0
    g16: LineSegment StartX=75.01 StartY=3.2 StartZ=0 EndX=75.01 EndY=7.6 EndZ=0
    g17: LineSegment StartX=82.8 StartY=3.2 StartZ=0 EndX=82.8 EndY=11.1 EndZ=0
    g18: LineSegment StartX=82.8 StartY=11.1 StartZ=0 EndX=78.51 EndY=11.1 EndZ=0
    g19: LineSegment StartX=75.01 StartY=39.2 StartZ=0 EndX=75.01 EndY=34.8 EndZ=0
  constraints (48):
    c: Radius(g0) = 3.5
    c: Coincident(g0,g-10)
    c: Radius(g1) = 3.5
    c: Coincident(g1,g-9)
    c: Radius(g2) = 3.5
    c: Coincident(g2,g-8)
    c: Radius(g3) = 3.5
    c: Coincident(g3,g-7)
    c: Coincident(g4,g-5)
    c: PointOnObject(g4,g-4)
    c: Coincident(g5,g4)
    c: Horizontal(g5)
    c: Coincident(g6,g4)
    c: PointOnObject(g6,g-5)
    c: Coincident(g7,g6)
    c: Vertical(g7)
    c: Coincident(g8,g-4)
    c: PointOnObject(g8,g-4)
    c: Coincident(g9,g8)
    c: Horizontal(g9)
    c: Coincident(g10,g8)
    c: PointOnObject(g10,g-3)
    c: Coincident(g11,g10)
    c: Vertical(g11)
    c: PointOnObject(g12,g-3)
    c: PointOnObject(g12,g-3)
    c: Coincident(g13,g12)
    c: Vertical(g13)
    c: Coincident(g14,g13)
    c: Horizontal(g14)
    c: Coincident(g15,g-6)
    c: PointOnObject(g15,g-5)
    c: Coincident(g16,g15)
    c: Vertical(g16)
    c: Coincident(g17,g15)
    c: Coincident(g18,g17)
    c: Horizontal(g18)
    c: Tangent(g3,g18) = -1.5708
    c: Tangent(g16,g3) = 1.5708
    c: Coincident(g19,g12)
    c: Vertical(g19)
    c: Tangent(g2,g19) = -1.5708
    c: Tangent(g2,g14) = 1.5708
    c: Tangent(g0,g7) = -1.5708
    c: Tangent(g0,g5) = 1.5708
    c: Tangent(g9,g1) = -1.5708
    c: Tangent(g1,g11) = 1.5708
    c: Tangent(g17,g13)
FEATURE [PartDesign::Pocket] Pocket001
  BaseFeature = -> Pad005
  Direction = (0,-1,2e-16)
  Length = 1.6
  Length2 = 5
  Profile = -> Sketch092
  ReferenceAxis = -> Sketch092 [N_Axis]
  Refine = true
  Suppressed = false
  Type = 0
FEATURE [PartDesign::Pad] Pad006
  BaseFeature = -> Pocket001
  Direction = (0,1,-2e-16)
  Length = 0.8
  Length2 = 10
  Profile = -> Sketch094
  ReferenceAxis = -> Sketch094 [N_Axis]
  Refine = true
  Suppressed = false
  Type = 0
FEATURE [PartDesign::Pad] Pad007
  BaseFeature = -> Pad006
  Direction = (0,1,-2e-16)
  Length = 2
  Length2 = 10
  Profile = -> Sketch095
  ReferenceAxis = -> Sketch095 [N_Axis]
  Refine = true
  Suppressed = false
  Type = 0
FEATURE [PartDesign::Pad] Pad008  label="Pad008 - forma impugnatura"
  BaseFeature = -> Pad007
  Direction = (0,1,-2e-16)
  Length = 1.6
  Length2 = 10
  Profile = -> Sketch096
  ReferenceAxis = -> Sketch096 [N_Axis]
  Refine = true
  Suppressed = false
  Type = 0
FEATURE [PartDesign::Pad] Pad009
  BaseFeature = -> Pad008
  Direction = (0,1,-2e-16)
  Length = 1.6
  Length2 = 10
  Profile = -> Sketch097
  ReferenceAxis = -> Sketch097 [N_Axis]
  Refine = true
  Suppressed = false
  Type = 0
FEATURE [Sketcher::SketchObject] Sketch098
  ArcFitTolerance = 1e-06
  AttachmentSupport = -> [Pad006]
  ExternalGeometry = -> [Binder]
  FullyConstrained = true
  MakeInternals = false
  MapMode = 5
  Placement = pos=(0,2.8,-7e-16) rot=(0,0.707107,0.707107;3.14159rad)
  sketch-geometry (4):
    g0: LineSegment StartX=118 StartY=39.2 StartZ=0 EndX=129 EndY=39.2 EndZ=0
    g1: LineSegment StartX=120.599 StartY=31.2 StartZ=0 EndX=131.599 EndY=31.2 EndZ=0
    g2: LineSegment StartX=129 StartY=39.2 StartZ=0 EndX=131.599 EndY=31.2 EndZ=0
    g3: LineSegment StartX=118 StartY=39.2 StartZ=0 EndX=120.599 EndY=31.2 EndZ=0
  constraints (12):
    c: PointOnObject(g0,g-3)
    c: PointOnObject(g0,g-3)
    c: DistanceX(g0,g0) = 11
    c: Horizontal(g1)
    c: Equal(g1,g0)
    c: Coincident(g2,g0)
    c: Coincident(g3,g0)
    c: Parallel(g-4,g2)
    c: Coincident(g1,g2)
    c: Coincident(g1,g3)
    c: DistanceY(g1,g0) = 8
    c: DistanceX(g-3,g0) = 118
FEATURE [Sketcher::SketchObject] Sketch099
  ArcFitTolerance = 1e-06
  AttachmentSupport = -> [Pad008]
  ExternalGeometry = -> [Binder]
  FullyConstrained = true
  MakeInternals = false
  MapMode = 5
  Placement = pos=(0,3.6,0) rot=(0,0.707107,0.707107;3.14159rad)
  sketch-geometry (13):
    g0: LineSegment StartX=192.176 StartY=-3.18451 StartZ=0 EndX=196.804 EndY=-13.1108 EndZ=0
    g1: LineSegment [constr] StartX=202.765 StartY=20.303 StartZ=0 EndX=181.223 EndY=20.303 EndZ=0
    g2: LineSegment [constr] StartX=181.223 StartY=20.303 StartZ=0 EndX=181.223 EndY=-3.18451 EndZ=0
    g3: ArcOfCircle CenterX=181.223 CenterY=-20.3764 CenterZ=0 NormalX=0 NormalY=0 NormalZ=1 AngleXU=0 Radius=17.1918 StartAngle=0.436332 EndAngle=1.57079
    g4: ArcOfEllipse CenterX=181.223 CenterY=8.55923 CenterZ=0 NormalX=0 NormalY=0 NormalZ=1 MajorRadius=23.4779 MinorRadius=11.7437 AngleXU=0 StartAngle=1.5708 EndAngle=4.71239
    g5: LineSegment [constr] StartX=204.701 StartY=8.55923 StartZ=0 EndX=157.745 EndY=8.55923 EndZ=0
    g6: LineSegment [constr] StartX=181.223 StartY=20.303 StartZ=0 EndX=181.223 EndY=-3.18451 EndZ=0
    g7: GeomPoint [constr] X=201.553 Y=8.55923 Z=0
    g8: GeomPoint [constr] X=160.894 Y=8.55923 Z=0
    g9: GeomPoint [constr] X=181.223 Y=-3.18451 Z=0
    g10: LineSegment StartX=181.223 StartY=20.303 StartZ=0 EndX=202.765 EndY=20.303 EndZ=0
    g11: ArcOfCircle CenterX=207.583 CenterY=4 CenterZ=0 NormalX=0 NormalY=0 NormalZ=1 AngleXU=0 Radius=17 StartAngle=1.85815 EndAngle=3.57792
    g12: LineSegment [constr] StartX=172.411 StartY=39.2 StartZ=0 EndX=192.176 EndY=-3.18451 EndZ=0
  constraints (27):
    c: Coincident(g1,g-7)
    c: Horizontal(g1)
    c: Coincident(g2,g1)
    c: Vertical(g2)
    c: Horizontal(g2,g0)
    c: Coincident(g3,g0)
    c: Coincident(g3,g2)
    c: InternalAlignment(g5-g8 -> g4) x4
    c: Horizontal(g5)
    c: PointOnObject(g4,g2)
    c: Coincident(g4,g1)
    c: DistanceX(g-3,g5) = 10.1
    c: Coincident(g4,g2)
    c: Tangent(g3,g-5)
    c: PointOnObject(g9,g4)
    c: PointOnObject(g9,g3)
    c: Tangent(g4,g3,g9) = 1.5708
    c: Coincident(g10,g1)
    c: Coincident(g10,g1)
    c: Equal(g11,g-4)
    c: Coincident(g11,g1)
    c: Coincident(g11,g0)
    c: PointOnObject(g12,g-6)
    c: PointOnObject(g1,g12)
    c: Tangent(g12,g-5) = -1.5708
    c: Tangent(g0,g-5) = -1.5708
    c: Horizontal(g9,g12)
FEATURE [Sketcher::SketchObject] Sketch106  label="Sketch106 - smusso impuniatura interno"
  ArcFitTolerance = 1e-06
  AttachmentSupport = -> [Pad008]
  ExternalGeometry = -> [Pad008]
  FullyConstrained = true
  MakeInternals = false
  MapMode = 5
  Placement = pos=(0,-1.585e-13,-80.4316) rot=(1,0,0;3.14159rad)
  sketch-geometry (9):
    g0: LineSegment StartX=-176.685 StartY=-3.6 StartZ=0 EndX=-176.685 EndY=-6.7e-15 EndZ=0
    g1: LineSegment [constr] StartX=-176.685 StartY=-7.37e-14 StartZ=0 EndX=-176.685 EndY=-6.8e-15 EndZ=0
    g2: LineSegment [constr] StartX=-186.685 StartY=-3.6 StartZ=0 EndX=-186.685 EndY=-6.7e-15 EndZ=0
    g3: ArcOfEllipse CenterX=-186.685 CenterY=-6.8e-15 CenterZ=0 NormalX=0 NormalY=0 NormalZ=1 MajorRadius=10 MinorRadius=3.6 AngleXU=-3.14159 StartAngle=1.5708 EndAngle=3.14159
    g4: LineSegment [constr] StartX=-196.685 StartY=-5.9e-15 StartZ=0 EndX=-176.685 EndY=-5.9e-15 EndZ=0
    g5: LineSegment [constr] StartX=-186.685 StartY=-3.6 StartZ=0 EndX=-186.685 EndY=3.6 EndZ=0
    g6: GeomPoint [constr] X=-196.015 Y=-6.9e-15 Z=0
    g7: GeomPoint [constr] X=-177.356 Y=-4.9e-15 Z=0
    g8: LineSegment StartX=-176.685 StartY=-3.6 StartZ=0 EndX=-186.685 EndY=-3.6 EndZ=0
  constraints (15):
    c: PointOnObject(g2,g-3)
    c: Coincident(g1,g-5)
    c: DistanceY(g1,g1) = 0
    c: Coincident(g0,g1)
    c: DistanceX(g2,g-5) = 10
    c: Vertical(g2)
    c: Horizontal(g2,g0)
    c: InternalAlignment(g4-g7 -> g3) x4
    c: Coincident(g3,g2)
    c: Horizontal(g4)
    c: Coincident(g3,g0)
    c: Tangent(g0,g-5) = 1.5708
    c: Coincident(g3,g2)
    c: Coincident(g8,g0)
    c: Coincident(g8,g2)
FEATURE [Sketcher::SketchObject] Sketch107  label="Sketch107 - smusso impugnatura esterno"
  ArcFitTolerance = 1e-06
  AttachmentSupport = -> [Pad008]
  ExternalGeometry = -> [Pad008]
  FullyConstrained = true
  MakeInternals = false
  MapMode = 5
  Placement = pos=(0,-1.585e-13,-80.4316) rot=(1,0,0;3.14159rad)
  sketch-geometry (9):
    g0: LineSegment [constr] StartX=-215.932 StartY=-1.416e-13 StartZ=0 EndX=-215.932 EndY=-1.416e-13 EndZ=0
    g1: LineSegment StartX=-215.932 StartY=-3.6 StartZ=0 EndX=-215.932 EndY=-1.417e-13 EndZ=0
    g2: LineSegment StartX=-215.932 StartY=-3.6 StartZ=0 EndX=-205.932 EndY=-3.6 EndZ=0
    g3: LineSegment [constr] StartX=-205.932 StartY=-3.6 StartZ=0 EndX=-205.932 EndY=-1.417e-13 EndZ=0
    g4: ArcOfEllipse CenterX=-205.932 CenterY=-1.416e-13 CenterZ=0 NormalX=0 NormalY=0 NormalZ=1 MajorRadius=10 MinorRadius=3.6 AngleXU=3.14159 StartAngle=-2.66e-14 EndAngle=1.5708
    g5: LineSegment [constr] StartX=-215.932 StartY=-1.416e-13 StartZ=0 EndX=-195.932 EndY=-1.416e-13 EndZ=0
    g6: LineSegment [constr] StartX=-205.932 StartY=-3.6 StartZ=0 EndX=-205.932 EndY=3.6 EndZ=0
    g7: GeomPoint [constr] X=-215.262 Y=-1.281e-13 Z=0
    g8: GeomPoint [constr] X=-196.602 Y=-1.551e-13 Z=0
  constraints (16):
    c: Coincident(g0,g-6)
    c: PointOnObject(g0,g-6)
    c: DistanceY(g0,g0) = 0
    c: Coincident(g1,g-6)
    c: Coincident(g1,g0)
    c: Tangent(g2,g-3)
    c: DistanceX(g2,g2) = 10
    c: Coincident(g3,g2)
    c: Vertical(g3)
    c: Horizontal(g3,g0)
    c: InternalAlignment(g5-g8 -> g4) x4
    c: Coincident(g4,g3)
    c: Horizontal(g5)
    c: Coincident(g4,g0)
    c: Coincident(g4,g2)
    c: PointOnObject(g2,g1)
FEATURE [Sketcher::SketchObject] Sketch108
  ArcFitTolerance = 1e-06
  AttachmentOffset = pos=(0,0,-1.6) rot=(0,0,1;0rad)
  AttachmentSupport = -> [Pad008]
  ExternalGeometry = -> [Binder]
  FullyConstrained = true
  MakeInternals = false
  MapMode = 5
  Placement = pos=(0,2,4e-16) rot=(0,0.707107,0.707107;3.14159rad)
  sketch-geometry (14):
    g0: LineSegment StartX=192.176 StartY=-3.18451 StartZ=0 EndX=193.827 EndY=-6.72678 EndZ=0
    g1: LineSegment [constr] StartX=202.765 StartY=20.303 StartZ=0 EndX=181.223 EndY=20.303 EndZ=0
    g2: LineSegment [constr] StartX=181.223 StartY=20.303 StartZ=0 EndX=181.223 EndY=1.30297 EndZ=0
    g3: ArcOfCircle CenterX=181.223 CenterY=-12.6042 CenterZ=0 NormalX=0 NormalY=0 NormalZ=1 AngleXU=0 Radius=13.9072 StartAngle=0.436332 EndAngle=1.5708
    g4: ArcOfEllipse CenterX=181.223 CenterY=10.803 CenterZ=0 NormalX=0 NormalY=0 NormalZ=1 MajorRadius=14.4779 MinorRadius=9.5 AngleXU=0 StartAngle=1.5708 EndAngle=4.71239
    g5: LineSegment [constr] StartX=195.701 StartY=10.803 StartZ=0 EndX=166.745 EndY=10.803 EndZ=0
    g6: LineSegment [constr] StartX=181.223 StartY=20.303 StartZ=0 EndX=181.223 EndY=1.30297 EndZ=0
    g7: GeomPoint [constr] X=192.148 Y=10.803 Z=0
    g8: GeomPoint [constr] X=170.298 Y=10.803 Z=0
    g9: LineSegment StartX=181.223 StartY=20.303 StartZ=0 EndX=202.765 EndY=20.303 EndZ=0
    g10: ArcOfCircle CenterX=207.583 CenterY=4 CenterZ=0 NormalX=0 NormalY=0 NormalZ=1 AngleXU=0 Radius=17 StartAngle=1.85815 EndAngle=3.57792
    g11: LineSegment [constr] StartX=172.411 StartY=39.2 StartZ=0 EndX=192.176 EndY=-3.18451 EndZ=0
    g12: GeomPoint [constr] X=181.223 Y=1.30297 Z=0
    g13: GeomPoint [constr] X=181.223 Y=1.30297 Z=0
  constraints (28):
    c: Coincident(g1,g-7)
    c: Horizontal(g1)
    c: Coincident(g2,g1)
    c: Vertical(g2)
    c: Coincident(g3,g2)
    c: InternalAlignment(g5-g8 -> g4) x4
    c: Horizontal(g5)
    c: PointOnObject(g4,g2)
    c: Coincident(g4,g1)
    c: DistanceX(g-3,g5) = 19.1
    c: Coincident(g4,g2)
    c: Coincident(g9,g1)
    c: Coincident(g9,g1)
    c: Coincident(g10,g1)
    c: Coincident(g10,g0)
    c: PointOnObject(g11,g-6)
    c: PointOnObject(g1,g11)
    c: DistanceY(g2,g1) = 19
    c: Coincident(g10,g-4)
    c: PointOnObject(g12,g4)
    c: PointOnObject(g12,g3)
    c: Tangent(g11,g-5) = -1.5708
    c: Tangent(g0,g-5) = -1.5708
    c: Tangent(g3,g0) = 1.5708
    c: PointOnObject(g13,g4)
    c: PointOnObject(g13,g3)
    c: Tangent(g4,g3,g13) = 1.5708
    c: Horizontal(g11,g0)
FEATURE [Part::Part2DObjectPython] Clone2D  label="Sketch108 (2D)"  # Draft 2D object (typed FeaturePython)
  Fuse = false
  Objects = -> [Sketch108]
  Placement = pos=(0,2,4e-16) rot=(0,0.707107,0.707107;3.14159rad)
  Scale = (1,1,1)
FEATURE [Sketcher::SketchObject] Sketch109
  ArcFitTolerance = 1e-06
  AttachmentOffset = pos=(0,0,-3.5) rot=(0,0,1;0rad)
  AttachmentSupport = -> [Pad008]
  ExternalGeometry = -> [Binder]
  FullyConstrained = true
  MakeInternals = false
  MapMode = 5
  Placement = pos=(0,0.1,8e-16) rot=(0,0.707107,0.707107;3.14159rad)
  sketch-geometry (1):
    g0: GeomPoint X=197.47 Y=8.55923 Z=0
  constraints (1):
    c: Symmetric(g-7,g-5,g0)
FEATURE [PartDesign::Chamfer] Chamfer005
  Angle = 45
  Base = -> Pad009 [Edge215,Edge212]
  BaseFeature = -> Pad009
  ChamferType = 1
  FlipDirection = false
  Refine = true
  Size = 1.5
  Size2 = 2.8
  SupportTransform = false
  Suppressed = false
  UseAllEdges = false
FEATURE [Sketcher::SketchObject] Sketch111
  ArcFitTolerance = 1e-06
  AttachmentSupport = -> [Pad009]
  ExternalGeometry = -> [Pad009]
  FullyConstrained = true
  MakeInternals = false
  MapMode = 5
  Placement = pos=(0,3.6,-8e-16) rot=(0,0.707107,0.707107;3.14159rad)
  sketch-geometry (21):
    g0: LineSegment [constr] StartX=97 StartY=36.8 StartZ=0 EndX=97 EndY=26.8 EndZ=0
    g1: LineSegment StartX=97 StartY=28.6 StartZ=0 EndX=97 EndY=27.8 EndZ=0
    g2: LineSegment StartX=97 StartY=27.8 StartZ=0 EndX=108 EndY=27.8 EndZ=0
    g3: LineSegment StartX=108 StartY=27.8 StartZ=0 EndX=108 EndY=28.6 EndZ=0
    g4: LineSegment StartX=108 StartY=28.6 StartZ=0 EndX=97 EndY=28.6 EndZ=0
    g5: LineSegment StartX=97 StartY=35.8 StartZ=0 EndX=97 EndY=35 EndZ=0
    g6: LineSegment StartX=97 StartY=35 StartZ=0 EndX=108 EndY=35 EndZ=0
    g7: LineSegment StartX=108 StartY=35 StartZ=0 EndX=108 EndY=35.8 EndZ=0
    g8: LineSegment StartX=108 StartY=35.8 StartZ=0 EndX=97 EndY=35.8 EndZ=0
    g9: LineSegment StartX=97 StartY=30.4 StartZ=0 EndX=97 EndY=29.6 EndZ=0
    g10: LineSegment StartX=97 StartY=29.6 StartZ=0 EndX=108 EndY=29.6 EndZ=0
    g11: LineSegment StartX=108 StartY=29.6 StartZ=0 EndX=108 EndY=30.4 EndZ=0
    g12: LineSegment StartX=108 StartY=30.4 StartZ=0 EndX=97 EndY=30.4 EndZ=0
    g13: LineSegment StartX=97 StartY=34 StartZ=0 EndX=97 EndY=33.2 EndZ=0
    g14: LineSegment StartX=97 StartY=33.2 StartZ=0 EndX=108 EndY=33.2 EndZ=0
    g15: LineSegment StartX=108 StartY=33.2 StartZ=0 EndX=108 EndY=34 EndZ=0
    g16: LineSegment StartX=108 StartY=34 StartZ=0 EndX=97 EndY=34 EndZ=0
    g17: LineSegment StartX=97 StartY=32.2 StartZ=0 EndX=97 EndY=31.4 EndZ=0
    g18: LineSegment StartX=97 StartY=31.4 StartZ=0 EndX=108 EndY=31.4 EndZ=0
    g19: LineSegment StartX=108 StartY=31.4 StartZ=0 EndX=108 EndY=32.2 EndZ=0
    g20: LineSegment StartX=108 StartY=32.2 StartZ=0 EndX=97 EndY=32.2 EndZ=0
  constraints (54):
    c: Vertical(g0)
    c: PointOnObject(g0,g-3)
    c: PointOnObject(g0,g-4)
    c: DistanceX(g0,g-5) = 11
    c: Coincident(g1,g2)
    c: Coincident(g2,g3)
    c: Coincident(g3,g4)
    c: Coincident(g4,g1)
    c: Horizontal(g2)
    c: Horizontal(g4)
    c: Tangent(g1,g0)
    c: Tangent(g3,g-5)
    c: DistanceY(g2,g3) = 0.8
    c: Coincident(g5,g6)
    c: Coincident(g6,g7)
    c: Coincident(g7,g8)
    c: Coincident(g8,g5)
    c: Horizontal(g6)
    c: Horizontal(g8)
    c: DistanceY(g6,g7) = 0.8
    c: Coincident(g9,g10)
    c: Coincident(g10,g11)
    c: Coincident(g11,g12)
    c: Coincident(g12,g9)
    c: Horizontal(g10)
    c: Horizontal(g12)
    c: DistanceY(g10,g11) = 0.8
    c: Tangent(g5,g0)
    c: Tangent(g7,g-5)
    c: Tangent(g9,g0)
    c: Tangent(g11,g-5)
    c: Coincident(g13,g14)
    c: Coincident(g14,g15)
    c: Coincident(g15,g16)
    c: Coincident(g16,g13)
    c: Horizontal(g14)
    c: Horizontal(g16)
    c: DistanceY(g14,g15) = 0.8
    c: Tangent(g13,g0)
    c: Tangent(g15,g-5)
    c: Coincident(g17,g18)
    c: Coincident(g18,g19)
    c: Coincident(g19,g20)
    c: Coincident(g20,g17)
    c: Horizontal(g18)
    c: Horizontal(g20)
    c: DistanceY(g18,g19) = 0.8
    c: Tangent(g17,g0)
    c: Tangent(g19,g-5)
    c: DistanceY(g1,g9) = 1
    c: DistanceY(g9,g17) = 1
    c: DistanceY(g17,g13) = 1
    c: DistanceY(g13,g5) = 1
    c: DistanceY(g0,g1) = 1
FEATURE [PartDesign::Pocket] Pocket004
  BaseFeature = -> Chamfer005
  Direction = (0,-1,2e-16)
  Length = 1
  Length2 = 5
  Profile = -> Sketch111
  ReferenceAxis = -> Sketch111 [N_Axis]
  Refine = true
  Suppressed = false
  Type = 0
FEATURE [PartDesign::Pad] Pad010
  BaseFeature = -> Pocket004
  Direction = (0,1,-2e-16)
  Length = 1.2
  Length2 = 10
  Profile = -> Sketch098
  ReferenceAxis = -> Sketch098 [N_Axis]
  Refine = true
  Suppressed = false
  Type = 0
FEATURE [PartDesign::Chamfer] Chamfer006
  Angle = 45
  Base = -> Pad010 [Edge291]
  BaseFeature = -> Pad010
  ChamferType = 1
  FlipDirection = false
  Refine = true
  Size = 1
  Size2 = 6
  SupportTransform = false
  Suppressed = false
  UseAllEdges = false
FEATURE [Sketcher::SketchObject] Sketch110
  ArcFitTolerance = 1e-06
  AttachmentSupport = -> [Pad010]
  ExternalGeometry = -> [Sketch098]
  FullyConstrained = true
  MakeInternals = false
  MapMode = 5
  Placement = pos=(0,4,-9e-16) rot=(0,0.707107,0.707107;3.14159rad)
  sketch-geometry (8):
    g0: LineSegment StartX=119.69 StartY=34 StartZ=0 EndX=130.69 EndY=34 EndZ=0
    g1: LineSegment StartX=119.95 StartY=33.2 StartZ=0 EndX=130.95 EndY=33.2 EndZ=0
    g2: LineSegment StartX=119.137 StartY=35.7 StartZ=0 EndX=130.137 EndY=35.7 EndZ=0
    g3: LineSegment StartX=118.877 StartY=36.5 StartZ=0 EndX=129.877 EndY=36.5 EndZ=0
    g4: LineSegment StartX=118.877 StartY=36.5 StartZ=0 EndX=119.137 EndY=35.7 EndZ=0
    g5: LineSegment StartX=129.877 StartY=36.5 StartZ=0 EndX=130.137 EndY=35.7 EndZ=0
    g6: LineSegment StartX=119.69 StartY=34 StartZ=0 EndX=119.95 EndY=33.2 EndZ=0
    g7: LineSegment StartX=130.69 StartY=34 StartZ=0 EndX=130.95 EndY=33.2 EndZ=0
  constraints (24):
    c: Horizontal(g0)
    c: Horizontal(g1)
    c: Horizontal(g2)
    c: Horizontal(g3)
    c: Equal(g1,g-5)
    c: Equal(g0,g-5)
    c: Equal(g2,g-5)
    c: Equal(g3,g-5)
    c: PointOnObject(g0,g-3)
    c: PointOnObject(g1,g-3)
    c: PointOnObject(g2,g-3)
    c: PointOnObject(g3,g-3)
    c: Coincident(g4,g3)
    c: Coincident(g4,g2)
    c: Coincident(g5,g3)
    c: Coincident(g5,g2)
    c: Coincident(g6,g0)
    c: Coincident(g6,g1)
    c: Coincident(g7,g0)
    c: Coincident(g7,g1)
    c: DistanceY(g1,g0) = 0.8
    c: DistanceY(g2,g3) = 0.8
    c: DistanceY(g-5,g1) = 2
    c: DistanceY(g-5,g2) = 4.5
FEATURE [PartDesign::Pocket] Pocket003
  BaseFeature = -> Chamfer006
  Direction = (0,-1,2e-16)
  Length = 1
  Length2 = 5
  Profile = -> Sketch110
  ReferenceAxis = -> Sketch110 [N_Axis]
  Refine = true
  Suppressed = false
  Type = 0
FEATURE [PartDesign::SubtractivePipe] SubtractivePipe
  AuxilleryCurvelinear = true
  AuxillerySpineTangent = false
  BaseFeature = -> Pocket003
  Binormal = (0,0,0)
  Mode = 0
  Profile = -> Sketch106
  Refine = true
  Spine = -> Pad008 [Edge215]
  SpineTangent = false
  Suppressed = false
  Transformation = 0
  Transition = 0
FEATURE [PartDesign::SubtractivePipe] SubtractivePipe001
  AuxilleryCurvelinear = true
  AuxillerySpineTangent = false
  BaseFeature = -> SubtractivePipe
  Binormal = (0,0,0)
  Mode = 0
  Profile = -> Sketch107
  Refine = true
  Spine = -> Pad008 [Edge213,Edge216,Edge210]
  SpineTangent = false
  Suppressed = false
  Transformation = 0
  Transition = 0
FEATURE [PartDesign::SubtractiveLoft] SubtractiveLoft
  BaseFeature = -> SubtractivePipe001
  Closed = false
  Profile = -> Sketch099
  Refine = true
  Ruled = false
  Sections = -> [Sketch108]
  Suppressed = false
FEATURE [PartDesign::SubtractiveLoft] SubtractiveLoft001
  BaseFeature = -> SubtractiveLoft
  Closed = false
  Profile = -> Clone2D
  Refine = true
  Ruled = false
  Sections = -> [Sketch109]
  Suppressed = false
FEATURE [Sketcher::SketchObject] Sketch112
  ArcFitTolerance = 1e-06
  AttachmentSupport = -> [Pad008]
  ExternalGeometry = -> [Binder]
  FullyConstrained = true
  MakeInternals = false
  MapMode = 5
  Placement = pos=(0,3.6,0) rot=(0,0.707107,0.707107;3.14159rad)
  sketch-geometry (4):
    g0: LineSegment [constr] StartX=167.782 StartY=-53.0314 StartZ=0 EndX=215.42 EndY=-53.0314 EndZ=0
    g1: GeomPoint [constr] X=191.282 Y=-53.0314 Z=0
    g2: Circle CenterX=191.282 CenterY=-53.0314 CenterZ=0 NormalX=0 NormalY=0 NormalZ=1 AngleXU=0 Radius=11.5
    g3: Circle CenterX=191.282 CenterY=-53.0314 CenterZ=0 NormalX=0 NormalY=0 NormalZ=1 AngleXU=0 Radius=10.7
  constraints (9):
    c: Horizontal(g0)
    c: PointOnObject(g0,g-3)
    c: Diameter(g2) = 23
    c: Coincident(g2,g1)
    c: Diameter(g3) = 21.4
    c: Coincident(g3,g1)
    c: DistanceX(g0,g1) = 23.5
    c: PointOnObject(g1,g0)
    c: Coincident(g0,g-4)
FEATURE [PartDesign::Chamfer] Chamfer016
  Angle = 45
  Base = -> SubtractiveLoft001 [Edge118,Edge117,Edge119,Edge120,Edge109]
  BaseFeature = -> SubtractiveLoft001
  ChamferType = 0
  FlipDirection = false
  Refine = true
  Size = 1.5
  Size2 = 1
  SupportTransform = false
  Suppressed = false
  UseAllEdges = false
FEATURE [PartDesign::Chamfer] Chamfer017
  Angle = 45
  Base = -> Chamfer016 [Edge15]
  BaseFeature = -> Chamfer016
  ChamferType = 0
  FlipDirection = false
  Refine = true
  Size = 1.6
  Size2 = 1
  SupportTransform = false
  Suppressed = false
  UseAllEdges = false
FEATURE [PartDesign::Chamfer] Chamfer018
  Angle = 45
  Base = -> Chamfer017 [Edge10]
  BaseFeature = -> Chamfer017
  ChamferType = 0
  FlipDirection = false
  Refine = true
  Size = 3.5
  Size2 = 1
  SupportTransform = false
  Suppressed = false
  UseAllEdges = false
FEATURE [PartDesign::Chamfer] Chamfer019
  Angle = 45
  Base = -> Chamfer018 [Edge94]
  BaseFeature = -> Chamfer018
  ChamferType = 0
  FlipDirection = false
  Refine = true
  Size = 1.9
  Size2 = 1
  SupportTransform = false
  Suppressed = false
  UseAllEdges = false
FEATURE [PartDesign::Fillet] Fillet009
  Base = -> Chamfer019 [Edge83]
  BaseFeature = -> Chamfer019
  Radius = 1.1
  Refine = true
  SupportTransform = false
  Suppressed = false
  UseAllEdges = false
FEATURE [PartDesign::Fillet] Fillet010
  Base = -> Fillet009 [Edge76]
  BaseFeature = -> Fillet009
  Radius = 1.9
  Refine = true
  SupportTransform = false
  Suppressed = false
  UseAllEdges = false
FEATURE [PartDesign::Pocket] Pocket005
  BaseFeature = -> Fillet010
  Direction = (0,-1,2e-16)
  Length = 0.8
  Length2 = 5
  Profile = -> Sketch112
  ReferenceAxis = -> Sketch112 [N_Axis]
  Refine = true
  Suppressed = false
  Type = 0
FEATURE [Part::Part2DObjectPython] ShapeString001  # Draft 2D object (typed FeaturePython)
  FontFile = <path>
  Fuse = false
  Justification = 6
  JustificationReference = 0
  KeepLeftMargin = false
  MakeFace = true
  ObliqueAngle = 0
  Placement = pos=(-183.5,3.6,-57.5) rot=(0,0.707107,0.707107;3.14159rad)
  ScaleToSize = true
  Size = 10
  String = AS
  Tracking = 0
FEATURE [PartDesign::Pocket] Pocket013
  BaseFeature = -> Pocket005
  Direction = (-1e-16,-1,2e-16)
  Length = 1
  Length2 = 5
  Profile = -> ShapeString001
  ReferenceAxis = -> ShapeString001 [N_Axis]
  Refine = true
  Suppressed = false
  Type = 0
FEATURE [PartDesign::Body] Body006  label="lato SX"
  AllowCompound = false
  Group = -> [Binder,Pad019,Chamfer015,Pocket002,Sketch133,Sketch091,Pad005,Sketch092,Pocket001,Sketch093,Sketch094,Pad006,Sketch095,Pad007,Sketch096,Pad008,Sketch097,Pad009,Chamfer005,Pocket004,Sketch098,Pad010,Chamfer006,Pocket003,SubtractivePipe,SubtractivePipe001,Sketch099,Sketch106,Sketch107,Sketch108,Clone2D,Sketch109,SubtractiveLoft,SubtractiveLoft001,Sketch110,Sketch111,Sketch112,Chamfer016,Chamfer017,+7 more]
  Origin = -> Origin006
  Tip = -> Pocket013
FEATURE [PartDesign::Pad] Pad020
  Direction = (0,-1,2e-16)
  Length = 25.2
  Length2 = 10
  Midplane = true
  Placement = pos=(0,0,0) rot=(1,0,0;1.5708rad)
  Profile = -> Sketch021
  ReferenceAxis = -> Sketch021 [N_Axis]
  Refine = true
  Suppressed = false
  Type = 0
FEATURE [PartDesign::Body] Body001  label="perno fermo rumble e driver solenoide"
  AllowCompound = false
  Group = -> [Sketch021,Pad020]
  Origin = -> Origin001
  Tip = -> Pad020
FEATURE [PartDesign::Pad] Pad021
  Direction = (0,-1,2e-16)
  Length = 16.8
  Length2 = 10
  Midplane = true
  Placement = pos=(0,0,0) rot=(1,0,0;1.5708rad)
  Profile = -> Sketch061
  ReferenceAxis = -> Sketch061 [N_Axis]
  Refine = true
  Suppressed = false
  Type = 0
FEATURE [PartDesign::Pocket] Pocket014
  BaseFeature = -> Pad021
  Direction = (0,1,-2e-16)
  Length = 12.8
  Length2 = 5
  Midplane = true
  Placement = pos=(0,0,0) rot=(1,0,0;1.5708rad)
  Profile = -> Sketch062
  ReferenceAxis = -> Sketch062 [N_Axis]
  Refine = true
  Suppressed = false
  Type = 0
FEATURE [PartDesign::Pad] Pad022
  BaseFeature = -> Pocket014
  Direction = (0,-1,2e-16)
  Length = 7.6
  Length2 = 10
  Midplane = true
  Placement = pos=(0,0,0) rot=(1,0,0;1.5708rad)
  Profile = -> Sketch063
  ReferenceAxis = -> Sketch063 [N_Axis]
  Refine = true
  Suppressed = false
  Type = 0
FEATURE [PartDesign::Body] Body003  label="blocco switch"
  AllowCompound = false
  Group = -> [Sketch061,Sketch062,Sketch063,Pad021,Pocket014,Pad022]
  Origin = -> Origin003
  Tip = -> Pad022
FEATURE [PartDesign::Pad] Pad024
  Direction = (0,-1,2e-16)
  Length = 17
  Length2 = 10
  Midplane = true
  Placement = pos=(0,0,0) rot=(1,0,0;1.5708rad)
  Profile = -> Sketch045
  ReferenceAxis = -> Sketch045 [N_Axis]
  Refine = true
  Suppressed = false
  Type = 0
FEATURE [PartDesign::Pocket] Pocket015
  BaseFeature = -> Pad024
  Direction = (-1,0,0)
  Length = 8
  Length2 = 5
  Placement = pos=(0,0,0) rot=(1,0,0;1.5708rad)
  Profile = -> Sketch047
  ReferenceAxis = -> Sketch047 [N_Axis]
  Refine = true
  Reversed = true
  Suppressed = false
  Type = 0
FEATURE [PartDesign::Pocket] Pocket016
  BaseFeature = -> Pocket015
  Direction = (-1,0,0)
  Length = 1
  Length2 = 5
  Placement = pos=(0,0,0) rot=(1,0,0;1.5708rad)
  Profile = -> Sketch046
  ReferenceAxis = -> Sketch046 [N_Axis]
  Refine = true
  Reversed = true
  Suppressed = false
  Type = 0
FEATURE [PartDesign::Pocket] Pocket017
  BaseFeature = -> Pocket016
  Direction = (0,1,-2e-16)
  Length = 17
  Length2 = 5
  Midplane = true
  Placement = pos=(0,0,0) rot=(1,0,0;1.5708rad)
  Profile = -> Sketch048
  ReferenceAxis = -> Sketch048 [N_Axis]
  Refine = true
  Suppressed = false
  Type = 0
FEATURE [PartDesign::Pad] Pad025
  BaseFeature = -> Pocket017
  Direction = (0,-1,2e-16)
  Length = 17
  Length2 = 10
  Midplane = true
  Placement = pos=(0,0,0) rot=(1,0,0;1.5708rad)
  Profile = -> Sketch049
  ReferenceAxis = -> Sketch049 [N_Axis]
  Refine = true
  Suppressed = false
  Type = 0
FEATURE [PartDesign::Pad] Pad026
  BaseFeature = -> Pad025
  Direction = (0,-1,2e-16)
  Length = 17
  Length2 = 10
  Midplane = true
  Placement = pos=(0,0,0) rot=(1,0,0;1.5708rad)
  Profile = -> Sketch066
  ReferenceAxis = -> Sketch066 [N_Axis]
  Refine = true
  Suppressed = false
  Type = 0
FEATURE [PartDesign::Pad] Pad027
  BaseFeature = -> Pad026
  Direction = (0,-1,2e-16)
  Length = 5
  Length2 = 10
  Midplane = true
  Placement = pos=(0,0,0) rot=(1,0,0;1.5708rad)
  Profile = -> Sketch064
  ReferenceAxis = -> Sketch064 [N_Axis]
  Refine = true
  Suppressed = false
  Type = 0
FEATURE [PartDesign::Pad] Pad028
  BaseFeature = -> Pad027
  Direction = (1,0,0)
  Length = 1
  Length2 = 10
  Placement = pos=(0,0,0) rot=(1,0,0;1.5708rad)
  Profile = -> Sketch068
  ReferenceAxis = -> Sketch068 [N_Axis]
  Refine = true
  Reversed = true
  Suppressed = false
  Type = 0
FEATURE [PartDesign::Chamfer] Chamfer020
  Angle = 45
  Base = -> Pad028 [Edge73,Edge75,Edge78,Edge77]
  BaseFeature = -> Pad028
  ChamferType = 0
  FlipDirection = false
  Placement = pos=(0,0,0) rot=(1,0,0;1.5708rad)
  Refine = true
  Size = 0.5
  Size2 = 1
  SupportTransform = false
  Suppressed = false
  UseAllEdges = false
FEATURE [PartDesign::Body] Body002  label="supporto per neopixel"
  AllowCompound = false
  Group = -> [Sketch045,Sketch047,Sketch046,Sketch048,Sketch049,Sketch066,Sketch064,Sketch068,Pad024,Pocket015,Pocket016,Pocket017,Pad025,Pad026,Pad027,Pad028,Chamfer020]
  Origin = -> Origin002
  Tip = -> Chamfer020
FEATURE [Sketcher::SketchObject] Sketch134  label="perno fermo rumble002"
  ArcFitTolerance = 1e-06
  AttachmentSupport = -> [XZ_Plane008]
  FullyConstrained = true
  MakeInternals = false
  MapMode = 5
  Placement = pos=(0,0,0) rot=(1,0,0;1.5708rad)
  sketch-geometry (16):
    g0: LineSegment StartX=0 StartY=0.45 StartZ=0 EndX=0 EndY=1.55 EndZ=0
    g1: LineSegment StartX=0.45 StartY=2 StartZ=0 EndX=1.55 EndY=2 EndZ=0
    g2: LineSegment StartX=2 StartY=1.55 StartZ=0 EndX=2 EndY=0.45 EndZ=0
    g3: LineSegment StartX=1.55 StartY=0 StartZ=0 EndX=0.45 EndY=0 EndZ=0
    g4: ArcOfCircle [constr] CenterX=0.45 CenterY=1.55 CenterZ=0 NormalX=0 NormalY=0 NormalZ=1 AngleXU=0 Radius=0.45 StartAngle=1.5708 EndAngle=3.14159
    g5: GeomPoint [constr] X=0 Y=2 Z=0
    g6: LineSegment StartX=0.45 StartY=2 StartZ=0 EndX=0 EndY=1.55 EndZ=0
    g7: ArcOfCircle [constr] CenterX=1.55 CenterY=1.55 CenterZ=0 NormalX=0 NormalY=0 NormalZ=1 AngleXU=0 Radius=0.45 StartAngle=0 EndAngle=1.5708
    g8: GeomPoint [constr] X=2 Y=2 Z=0
    g9: LineSegment StartX=2 StartY=1.55 StartZ=0 EndX=1.55 EndY=2 EndZ=0
    g10: ArcOfCircle [constr] CenterX=1.55 CenterY=0.45 CenterZ=0 NormalX=0 NormalY=0 NormalZ=1 AngleXU=0 Radius=0.45 StartAngle=4.71239 EndAngle=6.28319
    g11: GeomPoint [constr] X=2 Y=0 Z=0
    g12: LineSegment StartX=1.55 StartY=0 StartZ=0 EndX=2 EndY=0.45 EndZ=0
    g13: ArcOfCircle [constr] CenterX=0.45 CenterY=0.45 CenterZ=0 NormalX=0 NormalY=0 NormalZ=1 AngleXU=0 Radius=0.45 StartAngle=3.14159 EndAngle=4.71239
    g14: GeomPoint [constr] X=0 Y=0 Z=0
    g15: LineSegment StartX=0 StartY=0.45 StartZ=0 EndX=0.45 EndY=0 EndZ=0
  constraints (35):
    c: Coincident(g14,g-1)
    c: PointOnObject(g5,g-2)
    c: Horizontal(g1)
    c: Vertical(g2)
    c: Horizontal(g3)
    c: DistanceX(g5,g8) = 2
    c: DistanceY(g11,g8) = 2
    c: PointOnObject(g5,g0)
    c: PointOnObject(g5,g1)
    c: Tangent(g0,g4) = 1.5708
    c: Tangent(g1,g4) = 1.5708
    c: Coincident(g6,g0)
    c: Coincident(g6,g1)
    c: PointOnObject(g8,g2)
    c: PointOnObject(g8,g1)
    c: Tangent(g2,g7) = 1.5708
    c: Tangent(g1,g7) = 1.5708
    c: Coincident(g9,g2)
    c: Coincident(g9,g1)
    c: PointOnObject(g11,g2)
    c: PointOnObject(g11,g3)
    c: Tangent(g2,g10) = 1.5708
    c: Tangent(g3,g10) = 1.5708
    c: Coincident(g12,g2)
    c: Coincident(g12,g3)
    c: PointOnObject(g14,g0)
    c: PointOnObject(g14,g3)
    c: Tangent(g0,g13) = 1.5708
    c: Tangent(g3,g13) = 1.5708
    c: Coincident(g15,g0)
    c: Coincident(g15,g3)
    c: Equal(g6,g9)
    c: Equal(g9,g12)
    c: Equal(g12,g15)
    c: DistanceX(g14,g3) = 0.45
FEATURE [PartDesign::Pad] Pad029
  Direction = (0,-1,2e-16)
  Length = 17
  Length2 = 10
  Midplane = true
  Placement = pos=(0,0,0) rot=(1,0,0;1.5708rad)
  Profile = -> Sketch134
  ReferenceAxis = -> Sketch134 [N_Axis]
  Refine = true
  Suppressed = false
  Type = 0
FEATURE [PartDesign::Body] Body008  label="perno fermo neopixel"
  AllowCompound = false
  Group = -> [Sketch134,Pad029]
  Origin = -> Origin008
  Tip = -> Pad029
FEATURE [Sketcher::SketchObject] Sketch135  label="perno fermo rumble003"
  ArcFitTolerance = 1e-06
  AttachmentSupport = -> [XZ_Plane009]
  FullyConstrained = true
  MakeInternals = false
  MapMode = 5
  Placement = pos=(0,0,0) rot=(1,0,0;1.5708rad)
  sketch-geometry (16):
    g0: LineSegment StartX=4.69e-14 StartY=0.8 StartZ=0 EndX=-3.04e-14 EndY=3.1 EndZ=0
    g1: LineSegment StartX=0.8 StartY=3.9 StartZ=0 EndX=3.1 EndY=3.9 EndZ=0
    g2: LineSegment StartX=3.9 StartY=3.1 StartZ=0 EndX=3.9 EndY=0.8 EndZ=0
    g3: LineSegment StartX=3.1 StartY=0 StartZ=0 EndX=0.8 EndY=0 EndZ=0
    g4: ArcOfCircle [constr] CenterX=0.8 CenterY=3.1 CenterZ=0 NormalX=0 NormalY=0 NormalZ=1 AngleXU=0 Radius=0.8 StartAngle=1.5708 EndAngle=3.14159
    g5: GeomPoint [constr] X=0 Y=3.9 Z=0
    g6: LineSegment StartX=0.8 StartY=3.9 StartZ=0 EndX=-3.04e-14 EndY=3.1 EndZ=0
    g7: ArcOfCircle [constr] CenterX=3.1 CenterY=3.1 CenterZ=0 NormalX=0 NormalY=0 NormalZ=1 AngleXU=0 Radius=0.8 StartAngle=-2.4e-14 EndAngle=1.5708
    g8: GeomPoint [constr] X=3.9 Y=3.9 Z=0
    g9: LineSegment StartX=3.9 StartY=3.1 StartZ=0 EndX=3.1 EndY=3.9 EndZ=0
    g10: ArcOfCircle [constr] CenterX=3.1 CenterY=0.8 CenterZ=0 NormalX=0 NormalY=0 NormalZ=1 AngleXU=0 Radius=0.8 StartAngle=4.71239 EndAngle=6.28319
    g11: GeomPoint [constr] X=3.9 Y=0 Z=0
    g12: LineSegment StartX=3.1 StartY=0 StartZ=0 EndX=3.9 EndY=0.8 EndZ=0
    g13: ArcOfCircle [constr] CenterX=0.8 CenterY=0.8 CenterZ=0 NormalX=0 NormalY=0 NormalZ=1 AngleXU=0 Radius=0.8 StartAngle=3.14159 EndAngle=4.71239
    g14: GeomPoint [constr] X=0 Y=0 Z=0
    g15: LineSegment StartX=4.69e-14 StartY=0.8 StartZ=0 EndX=0.8 EndY=0 EndZ=0
  constraints (35):
    c: Coincident(g14,g-1)
    c: PointOnObject(g5,g-2)
    c: Horizontal(g1)
    c: Vertical(g2)
    c: Horizontal(g3)
    c: DistanceX(g5,g8) = 3.9
    c: DistanceY(g11,g8) = 3.9
    c: PointOnObject(g5,g0)
    c: PointOnObject(g5,g1)
    c: Tangent(g0,g4) = 1.5708
    c: Tangent(g1,g4) = 1.5708
    c: Coincident(g6,g0)
    c: Coincident(g6,g1)
    c: PointOnObject(g8,g2)
    c: PointOnObject(g8,g1)
    c: Tangent(g2,g7) = 1.5708
    c: Tangent(g1,g7) = 1.5708
    c: Coincident(g9,g2)
    c: Coincident(g9,g1)
    c: PointOnObject(g11,g2)
    c: PointOnObject(g11,g3)
    c: Tangent(g2,g10) = 1.5708
    c: Tangent(g3,g10) = 1.5708
    c: Coincident(g12,g2)
    c: Coincident(g12,g3)
    c: PointOnObject(g14,g0)
    c: PointOnObject(g14,g3)
    c: Tangent(g0,g13) = 1.5708
    c: Tangent(g3,g13) = 1.5708
    c: Coincident(g15,g0)
    c: Coincident(g15,g3)
    c: Equal(g6,g9)
    c: Equal(g9,g12)
    c: Equal(g12,g15)
    c: DistanceX(g14,g3) = 0.8
FEATURE [PartDesign::Pad] Pad030
  Direction = (0,-1,2e-16)
  Length = 25.2
  Length2 = 10
  Midplane = true
  Placement = pos=(0,0,0) rot=(1,0,0;1.5708rad)
  Profile = -> Sketch135
  ReferenceAxis = -> Sketch135 [N_Axis]
  Refine = true
  Suppressed = false
  Type = 0
FEATURE [PartDesign::Body] Body009  label="perno fermo switch - caricabatterie - grilletto"
  AllowCompound = false
  Group = -> [Sketch135,Pad030]
  Origin = -> Origin009
  Tip = -> Pad030
FEATURE [Sketcher::SketchObject] Sketch136  label="scavo_rele"
  ArcFitTolerance = 1e-06
  AttachmentSupport = -> [XZ_Plane]
  ExternalGeometry = -> [Sketch]
  FullyConstrained = true
  MakeInternals = false
  MapMode = 5
  Placement = pos=(0,0,0) rot=(1,0,0;1.5708rad)
  sketch-geometry (7):
    g0: LineSegment [constr] StartX=-173.013 StartY=-62.644 StartZ=0 EndX=-176.535 EndY=-73.4861 EndZ=0
    g1: LineSegment [constr] StartX=-173.013 StartY=-62.644 StartZ=0 EndX=-170.35 EndY=-63.5093 EndZ=0
    g2: LineSegment [constr] StartX=-173.013 StartY=-62.644 StartZ=0 EndX=-176.627 EndY=-61.4698 EndZ=0
    g3: LineSegment StartX=-176.627 StartY=-61.4698 StartZ=0 EndX=-170.35 EndY=-63.5093 EndZ=0
    g4: LineSegment StartX=-176.627 StartY=-61.4698 StartZ=0 EndX=-180.149 EndY=-72.3118 EndZ=0
    g5: LineSegment StartX=-170.35 StartY=-63.5093 StartZ=0 EndX=-173.872 EndY=-74.3513 EndZ=0
    g6: LineSegment StartX=-180.149 StartY=-72.3118 StartZ=0 EndX=-173.872 EndY=-74.3513 EndZ=0
  constraints (19):
    c: Tangent(g0,g-3)
    c: Distance(g0,g-3) = 89
    c: Distance(g0,g0) = 11.4
    c: Coincident(g1,g0)
    c: Coincident(g2,g0)
    c: Distance(g2) = 3.8
    c: Distance(g1) = 2.8
    c: Perpendicular(g0,g1)
    c: Perpendicular(g0,g2)
    c: Coincident(g3,g2)
    c: Coincident(g3,g1)
    c: Equal(g4,g0)
    c: Equal(g5,g0)
    c: Parallel(g4,g0)
    c: Parallel(g5,g0)
    c: Coincident(g4,g2)
    c: Coincident(g5,g1)
    c: Coincident(g6,g4)
    c: Coincident(g6,g5)
FEATURE [Part::Extrusion] Extrude076  label="Extrude076 - scavo_rele"
  Base = -> Sketch136
  Dir = (0,-1,2e-16)
  DirMode = 2
  FaceMakerClass = Part::FaceMakerBullseye
  FaceMakerMode = 3
  LengthFwd = 17.8
  LengthRev = 0
  Solid = true
  Symmetric = true
FEATURE [Sketcher::SketchObject] Sketch137  label="scavo_nuovo_driver"
  ArcFitTolerance = 1e-06
  AttachmentSupport = -> [XZ_Plane]
  ExternalGeometry = -> [Sketch]
  FullyConstrained = true
  MakeInternals = false
  MapMode = 5
  Placement = pos=(0,0,0) rot=(1,0,0;1.5708rad)
  sketch-geometry (7):
    g0: LineSegment [constr] StartX=-167.759 StartY=-46.4761 StartZ=0 EndX=-172.58 EndY=-61.3126 EndZ=0
    g1: LineSegment [constr] StartX=-167.759 StartY=-46.4761 StartZ=0 EndX=-165.477 EndY=-47.2177 EndZ=0
    g2: LineSegment [constr] StartX=-167.759 StartY=-46.4761 StartZ=0 EndX=-171.373 EndY=-45.3018 EndZ=0
    g3: LineSegment StartX=-171.373 StartY=-45.3018 StartZ=0 EndX=-165.477 EndY=-47.2177 EndZ=0
    g4: LineSegment StartX=-171.373 StartY=-45.3018 StartZ=0 EndX=-176.194 EndY=-60.1383 EndZ=0
    g5: LineSegment StartX=-165.477 StartY=-47.2177 StartZ=0 EndX=-170.297 EndY=-62.0542 EndZ=0
    g6: LineSegment StartX=-176.194 StartY=-60.1383 StartZ=0 EndX=-170.297 EndY=-62.0542 EndZ=0
  constraints (19):
    c: Distance(g0,g-3) = 72
    c: Distance(g0) = 15.6
    c: Tangent(g0,g-3)
    c: Coincident(g1,g0)
    c: Coincident(g2,g0)
    c: Distance(g1) = 2.4
    c: Distance(g2) = 3.8
    c: Perpendicular(g0,g1)
    c: Perpendicular(g0,g2)
    c: Coincident(g3,g2)
    c: Coincident(g3,g1)
    c: Equal(g4,g0)
    c: Equal(g5,g0)
    c: Parallel(g4,g0)
    c: Parallel(g5,g0)
    c: Coincident(g4,g2)
    c: Coincident(g5,g1)
    c: Coincident(g6,g4)
    c: Coincident(g6,g5)
FEATURE [Part::Extrusion] Extrude077  label="Extrude077 - scavo_nuovo_driver"
  Base = -> Sketch137
  Dir = (0,-1,2e-16)
  DirMode = 2
  FaceMakerClass = Part::FaceMakerBullseye
  FaceMakerMode = 3
  LengthFwd = 20.8
  LengthRev = 0
  Solid = true
  Symmetric = true
FEATURE [Sketcher::SketchObject] Sketch138  label="scavo_nuovo_driver_alto"
  ArcFitTolerance = 1e-06
  AttachmentSupport = -> [XZ_Plane]
  ExternalGeometry = -> [Sketch]
  FullyConstrained = true
  MakeInternals = false
  MapMode = 5
  Placement = pos=(0,0,0) rot=(1,0,0;1.5708rad)
  sketch-geometry (7):
    g0: LineSegment [constr] StartX=-188.796 StartY=17.7274 StartZ=0 EndX=-187.75 EndY=4.97025 EndZ=0
    g1: LineSegment StartX=-187.75 StartY=4.97025 StartZ=0 EndX=-189.743 EndY=4.8067 EndZ=0
    g2: LineSegment StartX=-187.75 StartY=4.97025 StartZ=0 EndX=-182.766 EndY=5.37913 EndZ=0
    g3: LineSegment StartX=-190.79 StartY=17.5638 StartZ=0 EndX=-189.743 EndY=4.8067 EndZ=0
    g4: LineSegment StartX=-183.813 StartY=18.1363 StartZ=0 EndX=-182.766 EndY=5.37913 EndZ=0
    g5: LineSegment StartX=-190.79 StartY=17.5638 StartZ=0 EndX=-188.796 EndY=17.7274 EndZ=0
    g6: LineSegment StartX=-188.796 StartY=17.7274 StartZ=0 EndX=-183.813 EndY=18.1363 EndZ=0
  constraints (20):
    c: Distance(g0) = 12.8
    c: DistanceY(g-3,g0) = 9
    c: PointOnObject(g0,g-4)
    c: PointOnObject(g0,g-4)
    c: Coincident(g1,g0)
    c: Coincident(g2,g0)
    c: Distance(g1) = 2
    c: Distance(g2) = 5
    c: Perpendicular(g0,g1)
    c: Perpendicular(g0,g2)
    c: Equal(g3,g0)
    c: Parallel(g3,g0)
    c: Coincident(g3,g1)
    c: Equal(g4,g0)
    c: Parallel(g4,g0)
    c: Coincident(g4,g2)
    c: Coincident(g5,g3)
    c: Coincident(g5,g0)
    c: Coincident(g6,g0)
    c: Coincident(g6,g4)
FEATURE [Part::Extrusion] Extrude078  label="Extrude078 - scavo_nuovo_driver_alto"
  Base = -> Sketch138
  Dir = (0,-1,2e-16)
  DirMode = 2
  FaceMakerClass = Part::FaceMakerBullseye
  FaceMakerMode = 3
  LengthFwd = 16.6
  LengthRev = 0
  Solid = true
  Symmetric = true
FEATURE [Sketcher::SketchObject] Sketch139  label="fermi_nuovo_driver_alto"
  ArcFitTolerance = 1e-06
  AttachmentSupport = -> [XZ_Plane]
  ExternalGeometry = -> [Sketch138,Sketch]
  FullyConstrained = true
  MakeInternals = false
  MapMode = 5
  Placement = pos=(0,0,0) rot=(1,0,0;1.5708rad)
  sketch-geometry (17):
    g0: LineSegment [constr] StartX=-188.314 StartY=16.4295 StartZ=0 EndX=-187.885 EndY=13.7638 EndZ=0
    g1: LineSegment [constr] StartX=-187.885 StartY=13.7638 StartZ=0 EndX=-187.456 EndY=11.0981 EndZ=0
    g2: LineSegment StartX=-187.885 StartY=13.7638 StartZ=0 EndX=-187.71 EndY=12.6778 EndZ=0
    g3: LineSegment StartX=-187.885 StartY=13.7638 StartZ=0 EndX=-188.06 EndY=14.8499 EndZ=0
    g4: LineSegment StartX=-187.71 StartY=12.6778 StartZ=0 EndX=-185.538 EndY=13.0274 EndZ=0
    g5: LineSegment StartX=-188.06 StartY=14.8499 StartZ=0 EndX=-185.888 EndY=15.1994 EndZ=0
    g6: LineSegment StartX=-185.888 StartY=15.1994 StartZ=0 EndX=-185.538 EndY=13.0274 EndZ=0
    g7: LineSegment StartX=-187.456 StartY=11.0981 StartZ=0 EndX=-189.035 EndY=10.8439 EndZ=0
    g8: LineSegment StartX=-188.314 StartY=16.4295 StartZ=0 EndX=-189.893 EndY=16.1753 EndZ=0
    g9: LineSegment StartX=-189.893 StartY=16.1753 StartZ=0 EndX=-189.035 EndY=10.8439 EndZ=0
    g10: LineSegment StartX=-187.456 StartY=11.0981 StartZ=0 EndX=-185.284 EndY=11.4477 EndZ=0
    g11: LineSegment StartX=-188.314 StartY=16.4295 StartZ=0 EndX=-186.142 EndY=16.7791 EndZ=0
    g12: LineSegment StartX=-184.308 StartY=15.4537 StartZ=0 EndX=-183.958 EndY=13.2816 EndZ=0
    g13: ArcOfCircle CenterX=-185.888 CenterY=15.1994 CenterZ=0 NormalX=0 NormalY=0 NormalZ=1 AngleXU=0 Radius=1.6 StartAngle=0.15957 EndAngle=1.73037
    g14: GeomPoint [constr] X=-184.562 Y=17.0333 Z=0
    g15: ArcOfCircle CenterX=-185.538 CenterY=13.0274 CenterZ=0 NormalX=0 NormalY=0 NormalZ=1 AngleXU=0 Radius=1.6 StartAngle=4.87196 EndAngle=6.44276
    g16: GeomPoint [constr] X=-183.704 Y=11.7019 Z=0
  constraints (43):
    c: Tangent(g1,g0) = -1.5708
    c: Distance(g0) = 2.7
    c: Equal(g1,g0)
    c: Tangent(g1,g-5)
    c: Coincident(g2,g0)
    c: Coincident(g3,g0)
    c: Distance(g2) = 1.1
    c: Equal(g3,g2)
    c: PointOnObject(g3,g2)
    c: Coincident(g4,g2)
    c: Coincident(g5,g3)
    c: Distance(g4) = 2.2
    c: Equal(g4,g5)
    c: Perpendicular(g1,g4)
    c: Perpendicular(g0,g5)
    c: Coincident(g6,g5)
    c: Coincident(g6,g4)
    c: Coincident(g7,g1)
    c: Coincident(g8,g0)
    c: Distance(g7) = 1.6
    c: Equal(g7,g8)
    c: Perpendicular(g1,g7)
    c: Perpendicular(g8,g0)
    c: Coincident(g9,g8)
    c: Coincident(g9,g7)
    c: Coincident(g10,g1)
    c: Coincident(g11,g0)
    c: Distance(g10,g16) = 3.8
    c: Perpendicular(g1,g10)
    c: Perpendicular(g1,g11)
    c: DistanceY(g0,g-4) = 3.8
    c: PointOnObject(g14,g12)
    c: PointOnObject(g14,g11)
    c: Tangent(g12,g13) = 1.5708
    c: Tangent(g11,g13) = 1.5708
    c: PointOnObject(g16,g12)
    c: PointOnObject(g16,g10)
    c: Tangent(g12,g15) = 1.5708
    c: Tangent(g10,g15) = -1.5708
    c: Equal(g13,g15)
    c: Coincident(g13,g5)
    c: Parallel(g2,g0)
    c: PointOnObject(g0,g-5)
FEATURE [Part::Extrusion] Extrude079  label="Extrude079 - fermi_nuovo_driver_alto"
  Base = -> Sketch139
  Dir = (0,-1,2e-16)
  DirMode = 2
  FaceMakerClass = Part::FaceMakerBullseye
  FaceMakerMode = 3
  LengthFwd = 25.2
  LengthRev = 0
  Solid = true
  Symmetric = true
FEATURE [Sketcher::SketchObject] Sketch140  label="scavo_diodo_nuovo_driver_alto"
  ArcFitTolerance = 1e-06
  AttachmentSupport = -> [XZ_Plane]
  ExternalGeometry = -> [Sketch138]
  FullyConstrained = true
  MakeInternals = false
  MapMode = 5
  Placement = pos=(0,0,0) rot=(1,0,0;1.5708rad)
  sketch-geometry (4):
    g0: LineSegment StartX=-190.79 StartY=17.5638 StartZ=0 EndX=-189.743 EndY=4.8067 EndZ=0
    g1: LineSegment StartX=-193.78 StartY=17.3185 StartZ=0 EndX=-192.733 EndY=4.56137 EndZ=0
    g2: LineSegment StartX=-190.79 StartY=17.5638 StartZ=0 EndX=-193.78 EndY=17.3185 EndZ=0
    g3: LineSegment StartX=-192.733 StartY=4.56137 StartZ=0 EndX=-189.743 EndY=4.8067 EndZ=0
  constraints (11):
    c: Equal(g0,g-3)
    c: Parallel(g0,g-3)
    c: Equal(g1,g-3)
    c: Parallel(g1,g-3)
    c: Coincident(g2,g0)
    c: Distance(g2) = 3
    c: Perpendicular(g0,g2)
    c: Coincident(g1,g2)
    c: Coincident(g3,g1)
    c: Coincident(g3,g0)
    c: Coincident(g0,g-3)
FEATURE [Part::Extrusion] Extrude080  label="Extrude080 - scavo_diodo_nuovo_driver_alto"
  Base = -> Sketch140
  Dir = (0,-1,2e-16)
  DirMode = 2
  FaceMakerClass = Part::FaceMakerBullseye
  FaceMakerMode = 3
  LengthFwd = 4
  LengthRev = 0
  Placement = pos=(0,7.8,0) rot=(0,0,1;0rad)
  Solid = true
  Symmetric = false
FEATURE [Part::MultiFuse] Fusion001
  Refine = true
  Shapes = -> [Cut043,Extrude079]
FEATURE [Part::Cut] Cut044
  Base = -> Fusion001
  Refine = true
  Tool = -> Extrude078
FEATURE [Part::Cut] Cut045
  Base = -> Cut044
  Refine = true
  Tool = -> Extrude080
FEATURE [Sketcher::SketchObject] Sketch141  label="fermi_nuovo_driver"
  ArcFitTolerance = 1e-06
  AttachmentSupport = -> [XZ_Plane]
  ExternalGeometry = -> [Sketch,Sketch137]
  FullyConstrained = true
  MakeInternals = false
  MapMode = 5
  Placement = pos=(0,0,0) rot=(1,0,0;1.5708rad)
  sketch-geometry (16):
    g0: LineSegment [constr] StartX=-165.477 StartY=-47.2177 StartZ=0 EndX=-167.759 EndY=-46.4761 EndZ=0
    g1: LineSegment [constr] StartX=-167.759 StartY=-46.4761 StartZ=0 EndX=-168.006 EndY=-47.2369 EndZ=0
    g2: LineSegment [constr] StartX=-168.006 StartY=-47.2369 StartZ=0 EndX=-169.675 EndY=-52.3726 EndZ=0
    g3: LineSegment StartX=-169.675 StartY=-52.3726 StartZ=0 EndX=-171.767 EndY=-51.6928 EndZ=0
    g4: LineSegment StartX=-172.795 StartY=-49.6767 StartZ=0 EndX=-172.115 EndY=-47.5843 EndZ=0
    g5: LineSegment StartX=-170.099 StartY=-46.5571 StartZ=0 EndX=-166.485 EndY=-47.7313 EndZ=0
    g6: LineSegment StartX=-166.485 StartY=-47.7313 StartZ=0 EndX=-168.153 EndY=-52.867 EndZ=0
    g7: LineSegment StartX=-169.675 StartY=-52.3726 StartZ=0 EndX=-168.153 EndY=-52.867 EndZ=0
    g8: LineSegment StartX=-170.593 StartY=-48.0788 StartZ=0 EndX=-171.273 EndY=-50.1711 EndZ=0
    g9: LineSegment StartX=-171.273 StartY=-50.1711 StartZ=0 EndX=-169.181 EndY=-50.8509 EndZ=0
    g10: LineSegment StartX=-169.181 StartY=-50.8509 StartZ=0 EndX=-168.501 EndY=-48.7586 EndZ=0
    g11: LineSegment StartX=-168.501 StartY=-48.7586 StartZ=0 EndX=-170.593 EndY=-48.0788 EndZ=0
    g12: ArcOfCircle CenterX=-170.593 CenterY=-48.0788 CenterZ=0 NormalX=0 NormalY=0 NormalZ=1 AngleXU=0 Radius=1.6 StartAngle=1.25664 EndAngle=2.82743
    g13: GeomPoint [constr] X=-171.62 Y=-46.0626 Z=0
    g14: ArcOfCircle CenterX=-171.273 CenterY=-50.1711 CenterZ=0 NormalX=0 NormalY=0 NormalZ=1 AngleXU=0 Radius=1.6 StartAngle=2.82743 EndAngle=4.39823
    g15: GeomPoint [constr] X=-173.289 Y=-51.1984 Z=0
  constraints (41):
    c: Coincident(g0,g-4)
    c: PointOnObject(g0,g-3)
    c: Parallel(g0,g-4)
    c: Coincident(g1,g0)
    c: Parallel(g1,g-3)
    c: Distance(g1) = 0.8
    c: Coincident(g2,g1)
    c: Distance(g2) = 5.4
    c: Coincident(g3,g2)
    c: Parallel(g2,g-3)
    c: Distance(g15,g13) = 5.4
    c: Perpendicular(g3,g2)
    c: Parallel(g4,g2)
    c: Distance(g5,g13) = 5.4
    c: Distance(g3,g15) = 3.8
    c: Perpendicular(g4,g5)
    c: Coincident(g6,g5)
    c: Distance(g6) = 5.4
    c: Parallel(g6,g4)
    c: Coincident(g7,g2)
    c: Coincident(g7,g6)
    c: Coincident(g8,g9)
    c: Coincident(g9,g10)
    c: Coincident(g10,g11)
    c: Coincident(g11,g8)
    c: Distance(g8,g10) = 2.2
    c: Distance(g9,g11) = 2.2
    c: Perpendicular(g11,g8)
    c: Equal(g8,g10)
    c: Equal(g11,g9)
    c: Tangent(g10,g2)
    c: Distance(g10,g1) = 1.6
    c: PointOnObject(g13,g4)
    c: PointOnObject(g13,g5)
    c: Tangent(g4,g12) = 1.5708
    c: Tangent(g5,g12) = 1.5708
    c: PointOnObject(g15,g4)
    c: Tangent(g4,g14) = 1.5708
    c: Tangent(g3,g14) = 1.5708
    c: Equal(g14,g12)
    c: Coincident(g12,g8)
FEATURE [Part::Extrusion] Extrude081  label="Extrude081 - fermi_nuovo_driver"
  Base = -> Sketch141
  Dir = (0,-1,2e-16)
  DirMode = 2
  FaceMakerClass = Part::FaceMakerBullseye
  FaceMakerMode = 3
  LengthFwd = 25.2
  LengthRev = 0
  Solid = true
  Symmetric = true
FEATURE [Part::MultiFuse] Fusion002
  Refine = true
  Shapes = -> [Cut045,Extrude081]
FEATURE [Part::Cut] Cut046
  Base = -> Fusion002
  Refine = true
  Tool = -> Extrude077
FEATURE [Sketcher::SketchObject] Sketch142  label="fermi_rele"
  ArcFitTolerance = 1e-06
  AttachmentSupport = -> [XZ_Plane]
  ExternalGeometry = -> [Sketch,Sketch136]
  FullyConstrained = true
  MakeInternals = false
  MapMode = 5
  Placement = pos=(0,0,0) rot=(1,0,0;1.5708rad)
  sketch-geometry (15):
    g0: LineSegment StartX=-177.245 StartY=-63.3719 StartZ=0 EndX=-177.924 EndY=-65.4642 EndZ=0
    g1: LineSegment StartX=-175.228 StartY=-62.3446 StartZ=0 EndX=-171.614 EndY=-63.5189 EndZ=0
    g2: LineSegment StartX=-171.614 StartY=-63.5189 StartZ=0 EndX=-173.283 EndY=-68.6546 EndZ=0
    g3: LineSegment StartX=-176.897 StartY=-67.4803 StartZ=0 EndX=-173.283 EndY=-68.6546 EndZ=0
    g4: LineSegment StartX=-175.723 StartY=-63.8663 StartZ=0 EndX=-173.631 EndY=-64.5461 EndZ=0
    g5: LineSegment StartX=-175.723 StartY=-63.8663 StartZ=0 EndX=-176.403 EndY=-65.9586 EndZ=0
    g6: LineSegment StartX=-173.631 StartY=-64.5461 StartZ=0 EndX=-174.31 EndY=-66.6385 EndZ=0
    g7: LineSegment StartX=-176.403 StartY=-65.9586 StartZ=0 EndX=-174.31 EndY=-66.6385 EndZ=0
    g8: LineSegment [constr] StartX=-173.631 StartY=-64.5461 StartZ=0 EndX=-173.136 EndY=-63.0245 EndZ=0
    g9: LineSegment [constr] StartX=-173.631 StartY=-64.5461 StartZ=0 EndX=-172.109 EndY=-65.0406 EndZ=0
    g10: LineSegment [constr] StartX=-170.35 StartY=-63.5093 StartZ=0 EndX=-173.013 EndY=-62.644 EndZ=0
    g11: ArcOfCircle CenterX=-175.723 CenterY=-63.8663 CenterZ=0 NormalX=0 NormalY=0 NormalZ=1 AngleXU=0 Radius=1.6 StartAngle=1.25664 EndAngle=2.82743
    g12: GeomPoint [constr] X=-176.75 Y=-61.8502 Z=0
    g13: ArcOfCircle CenterX=-176.403 CenterY=-65.9586 CenterZ=0 NormalX=0 NormalY=0 NormalZ=1 AngleXU=0 Radius=1.6 StartAngle=2.82743 EndAngle=4.39823
    g14: GeomPoint [constr] X=-178.419 Y=-66.9859 Z=0
  constraints (39):
    c: Distance(g14,g12) = 5.4
    c: Distance(g1,g12) = 5.4
    c: Perpendicular(g1,g0)
    c: Coincident(g2,g1)
    c: Parallel(g2,g0)
    c: Coincident(g3,g2)
    c: Parallel(g2,g-3)
    c: Coincident(g5,g4)
    c: Distance(g5) = 2.2
    c: Distance(g4) = 2.2
    c: Perpendicular(g4,g5)
    c: Coincident(g6,g4)
    c: Equal(g6,g5)
    c: Parallel(g6,g5)
    c: Coincident(g7,g5)
    c: Coincident(g7,g6)
    c: Coincident(g8,g4)
    c: Coincident(g9,g4)
    c: Distance(g8) = 1.6
    c: Distance(g9) = 1.6
    c: Parallel(g8,g6)
    c: Parallel(g9,g4)
    c: PointOnObject(g8,g1)
    c: PointOnObject(g9,g2)
    c: Coincident(g10,g-4)
    c: Parallel(g10,g-4)
    c: PointOnObject(g10,g-3)
    c: Tangent(g6,g-3) = 1.5708
    c: Distance(g4,g10) = 2
    c: PointOnObject(g12,g1)
    c: Tangent(g1,g11) = 1.5708
    c: Tangent(g0,g11) = -1.5708
    c: PointOnObject(g14,g3)
    c: PointOnObject(g14,g0)
    c: Tangent(g3,g13) = -1.5708
    c: Tangent(g0,g13) = -1.5708
    c: Equal(g11,g13)
    c: Coincident(g11,g4)
    c: Parallel(g3,g1)
FEATURE [Part::Extrusion] Extrude082  label="Extrude082 - fermi_rele"
  Base = -> Sketch142
  Dir = (0,-1,2e-16)
  DirMode = 2
  FaceMakerClass = Part::FaceMakerBullseye
  FaceMakerMode = 3
  LengthFwd = 25.2
  LengthRev = 0
  Solid = true
  Symmetric = true
FEATURE [Part::MultiFuse] Fusion003
  Refine = true
  Shapes = -> [Cut046,Extrude082]
FEATURE [Part::Cut] Cut047
  Base = -> Fusion003
  Refine = true
  Tool = -> Extrude076
FEATURE [Sketcher::SketchObject] Sketch143  label="foro_passaggio_cavi_led_batteria"
  ArcFitTolerance = 1e-06
  AttachmentSupport = -> [XZ_Plane]
  ExternalGeometry = -> [Sketch,Sketch042,Sketch036]
  FullyConstrained = true
  MakeInternals = false
  MapMode = 5
  Placement = pos=(0,0,0) rot=(1,0,0;1.5708rad)
  sketch-geometry (4):
    g0: LineSegment StartX=-207.775 StartY=-41.3701 StartZ=0 EndX=-213.607 EndY=-53.8767 EndZ=0
    g1: LineSegment StartX=-213.607 StartY=-53.8767 StartZ=0 EndX=-211.843 EndY=-59.5559 EndZ=0
    g2: LineSegment StartX=-207.775 StartY=-41.3701 StartZ=0 EndX=-207.775 EndY=-50.8316 EndZ=0
    g3: LineSegment StartX=-207.775 StartY=-50.8316 StartZ=0 EndX=-211.843 EndY=-59.5559 EndZ=0
  constraints (9):
    c: Coincident(g0,g-3)
    c: PointOnObject(g1,g-6)
    c: Coincident(g1,g0)
    c: Coincident(g2,g0)
    c: Coincident(g2,g-7)
    c: Coincident(g3,g2)
    c: Parallel(g3,g0)
    c: Coincident(g3,g1)
    c: Coincident(g0,g-5)
FEATURE [Part::Extrusion] Extrude083  label="Extrude083 - foro_passaggio_cavi_led_batteria"
  Base = -> Sketch143
  Dir = (0,-1,2e-16)
  DirMode = 2
  FaceMakerClass = Part::FaceMakerBullseye
  FaceMakerMode = 3
  LengthFwd = 6
  LengthRev = 0
  Solid = true
  Symmetric = true
FEATURE [Part::Cut] Cut048
  Base = -> Cut047
  Refine = true
  Tool = -> Extrude083
FEATURE [Sketcher::SketchObject] Sketch144  label="foro_areazione_alimentatore"
  ArcFitTolerance = 1e-06
  AttachmentSupport = -> [XZ_Plane]
  ExternalGeometry = -> [Sketch036]
  FullyConstrained = true
  MakeInternals = false
  MapMode = 5
  Placement = pos=(0,0,0) rot=(1,0,0;1.5708rad)
  sketch-geometry (4):
    g0: LineSegment StartX=-211.843 StartY=-60.3701 StartZ=0 EndX=-207.775 EndY=-60.3701 EndZ=0
    g1: LineSegment StartX=-207.775 StartY=-60.3701 StartZ=0 EndX=-207.775 EndY=-70.3701 EndZ=0
    g2: LineSegment StartX=-211.843 StartY=-60.3701 StartZ=0 EndX=-211.843 EndY=-70.3701 EndZ=0
    g3: LineSegment StartX=-207.775 StartY=-70.3701 StartZ=0 EndX=-211.843 EndY=-70.3701 EndZ=0
  constraints (11):
    c: Horizontal(g0)
    c: Distance(g1) = 10
    c: Coincident(g1,g0)
    c: Tangent(g1,g-3)
    c: PointOnObject(g0,g-4)
    c: Coincident(g2,g0)
    c: PointOnObject(g2,g-4)
    c: Coincident(g3,g1)
    c: Horizontal(g3)
    c: Coincident(g3,g2)
    c: DistanceY(g0,g-3) = 19
FEATURE [Part::Extrusion] Extrude084  label="Extrude084 - foro_areazione_alimentatore"
  Base = -> Sketch144
  Dir = (0,-1,2e-16)
  DirMode = 2
  FaceMakerClass = Part::FaceMakerBullseye
  FaceMakerMode = 3
  LengthFwd = 10
  LengthRev = 0
  Solid = true
  Symmetric = true
FEATURE [Part::Cut] Cut049
  Base = -> Cut048
  Refine = true
  Tool = -> Extrude084
FEATURE [Sketcher::SketchObject] Sketch145  label="foro_per_condesatore"
  ArcFitTolerance = 1e-06
  AttachmentSupport = -> [XZ_Plane]
  ExternalGeometry = -> [Sketch,Sketch139]
  FullyConstrained = true
  MakeInternals = false
  MapMode = 5
  Placement = pos=(0,0,0) rot=(1,0,0;1.5708rad)
  sketch-geometry (1):
    g0: Circle CenterX=-182.345 CenterY=7.02342 CenterZ=0 NormalX=0 NormalY=0 NormalZ=1 AngleXU=0 Radius=5.2
  constraints (3):
    c: Diameter(g0) = 10.4
    c: Tangent(g0,g-3)
    c: Tangent(g0,g-4)
FEATURE [Part::Extrusion] Extrude085  label="Extrude085 - foro_per_condesatore"
  Base = -> Sketch145
  Dir = (0,-1,2e-16)
  DirMode = 2
  FaceMakerClass = Part::FaceMakerBullseye
  FaceMakerMode = 3
  LengthFwd = 25.2
  LengthRev = 0
  Solid = true
  Symmetric = true
FEATURE [Part::Cut] Cut050
  Base = -> Cut049
  Refine = true
  Tool = -> Extrude085
FEATURE [Sketcher::SketchObject] Sketch146  label="scavo_pulsante_6x6_per_led_batteria"
  ArcFitTolerance = 1e-06
  AttachmentSupport = -> [XZ_Plane]
  ExternalGeometry = -> [Sketch036,Sketch016]
  FullyConstrained = true
  MakeInternals = false
  MapMode = 5
  Placement = pos=(0,0,0) rot=(1,0,0;1.5708rad)
  sketch-geometry (4):
    g0: LineSegment StartX=-217.243 StartY=-66.0316 StartZ=0 EndX=-217.243 EndY=-72.8316 EndZ=0
    g1: LineSegment StartX=-217.243 StartY=-72.8316 StartZ=0 EndX=-211.043 EndY=-72.8316 EndZ=0
    g2: LineSegment StartX=-211.043 StartY=-72.8316 StartZ=0 EndX=-211.043 EndY=-66.0316 EndZ=0
    g3: LineSegment StartX=-211.043 StartY=-66.0316 StartZ=0 EndX=-217.243 EndY=-66.0316 EndZ=0
  constraints (12):
    c: Coincident(g0,g1)
    c: Coincident(g1,g2)
    c: Coincident(g2,g3)
    c: Coincident(g3,g0)
    c: Vertical(g0)
    c: Vertical(g2)
    c: Horizontal(g1)
    c: Horizontal(g3)
    c: Distance(g0,g2) = 6.2
    c: Distance(g1,g3) = 6.8
    c: Tangent(g1,g-4)
    c: DistanceX(g-3,g1) = 0.8
FEATURE [Part::Extrusion] Extrude086  label="Extrude086 - scavo_pulsante_6x6_per_led_batteria"
  Base = -> Sketch146
  Dir = (0,-1,2e-16)
  DirMode = 2
  FaceMakerClass = Part::FaceMakerBullseye
  FaceMakerMode = 3
  LengthFwd = 4.2
  LengthRev = 0
  Placement = pos=(0,12.6,0) rot=(0,0,1;0rad)
  Solid = true
  Symmetric = false
FEATURE [Sketcher::SketchObject] Sketch147  label="scavo_led_stato_batteria"
  ArcFitTolerance = 1e-06
  AttachmentSupport = -> [XZ_Plane]
  ExternalGeometry = -> [Sketch036,Sketch]
  FullyConstrained = true
  MakeInternals = false
  MapMode = 5
  Placement = pos=(0,0,0) rot=(1,0,0;1.5708rad)
  sketch-geometry (4):
    g0: LineSegment StartX=-213.412 StartY=-54.1504 StartZ=0 EndX=-217.3 EndY=-62.4884 EndZ=0
    g1: LineSegment StartX=-217.3 StartY=-62.4884 StartZ=0 EndX=-213.131 EndY=-64.4325 EndZ=0
    g2: LineSegment StartX=-213.131 StartY=-64.4325 StartZ=0 EndX=-209.243 EndY=-56.0944 EndZ=0
    g3: LineSegment StartX=-209.243 StartY=-56.0944 StartZ=0 EndX=-213.412 EndY=-54.1504 EndZ=0
  constraints (12):
    c: Coincident(g0,g1)
    c: Coincident(g1,g2)
    c: Coincident(g2,g3)
    c: Coincident(g3,g0)
    c: Distance(g0,g2) = 4.6
    c: Distance(g1,g3) = 9.2
    c: DistanceY(g2,g-3) = 6
    c: Equal(g0,g2)
    c: Equal(g1,g3)
    c: Perpendicular(g3,g0)
    c: Parallel(g0,g-4)
    c: DistanceX(g-3,g2) = 2.6
FEATURE [PartDesign::Body] Body  label="Struttura pistola"
  AllowCompound = false
  Group = -> [Sketch,Sketch002,Sketch004,DatumPlane,Sketch005,DatumPlane001,CopyCut,Sketch008,Sketch009,Sketch010,Sketch011,Sketch012,Sketch013,Sketch014,Sketch015,Sketch016,Sketch017,Sketch018,Sketch019,Sketch020,Sketch022,Sketch023,Sketch024,Sketch025,Sketch026,Sketch027,Sketch029,Sketch030,Sketch031,Sketch032,Sketch033,Sketch034,Sketch035,Sketch036,Sketch037,Sketch038,Sketch039,Sketch040,Sketch041,Sketch042,+27 more]
  Origin = -> Origin
FEATURE [Part::Extrusion] Extrude087  label="Extrude087 - scavo_led_stato_batteria"
  Base = -> Sketch147
  Dir = (0,-1,2e-16)
  DirMode = 2
  FaceMakerClass = Part::FaceMakerBullseye
  FaceMakerMode = 3
  LengthFwd = 2
  LengthRev = 0
  Placement = pos=(0,12.6,0) rot=(0,0,1;0rad)
  Solid = true
  Symmetric = false
FEATURE [Part::Cut] Cut051
  Base = -> Cut050
  Refine = true
  Tool = -> Extrude086
FEATURE [Part::Cut] Cut052
  Base = -> Cut051
  Refine = true
  Tool = -> Extrude087
FEATURE [Sketcher::SketchObject] Sketch148
  ArcFitTolerance = 1e-06
  AttachmentSupport = -> [Pad016]
  ExternalGeometry = -> [Pad016]
  FullyConstrained = true
  MakeInternals = false
  MapMode = 5
  Placement = pos=(0,0,-80.4316) rot=(1,0,0;3.14159rad)
  sketch-geometry (8):
    g0: LineSegment StartX=-176.685 StartY=3.6 StartZ=0 EndX=-186.685 EndY=3.6 EndZ=0
    g1: LineSegment StartX=-176.685 StartY=3.6 StartZ=0 EndX=-176.685 EndY=1.69e-14 EndZ=0
    g2: LineSegment [constr] StartX=-186.685 StartY=3.6 StartZ=0 EndX=-186.685 EndY=1.69e-14 EndZ=0
    g3: ArcOfEllipse CenterX=-186.685 CenterY=1.68e-14 CenterZ=0 NormalX=0 NormalY=0 NormalZ=1 MajorRadius=10 MinorRadius=3.6 AngleXU=0 StartAngle=0 EndAngle=1.5708
    g4: LineSegment [constr] StartX=-176.685 StartY=1.68e-14 StartZ=0 EndX=-196.685 EndY=1.68e-14 EndZ=0
    g5: LineSegment [constr] StartX=-186.685 StartY=3.6 StartZ=0 EndX=-186.685 EndY=-3.6 EndZ=0
    g6: GeomPoint [constr] X=-177.356 Y=1.68e-14 Z=0
    g7: GeomPoint [constr] X=-196.015 Y=1.68e-14 Z=0
  constraints (13):
    c: Distance(g0) = 10
    c: Coincident(g0,g-5)
    c: PointOnObject(g0,g-3)
    c: Coincident(g1,g0)
    c: Coincident(g1,g-5)
    c: Coincident(g2,g0)
    c: Vertical(g2)
    c: PointOnObject(g2,g-4)
    c: InternalAlignment(g4-g7 -> g3) x4
    c: Coincident(g3,g2)
    c: Coincident(g3,g0)
    c: Coincident(g3,g1)
    c: Horizontal(g4)
FEATURE [PartDesign::SubtractivePipe] SubtractivePipe004
  AuxilleryCurvelinear = true
  AuxillerySpineTangent = false
  BaseFeature = -> Pad016
  Binormal = (0,0,0)
  Mode = 0
  Profile = -> Sketch148
  Refine = true
  Spine = -> Pad016 [Edge254]
  SpineTangent = false
  Suppressed = false
  Transformation = 0
  Transition = 0
FEATURE [Sketcher::SketchObject] Sketch149
  ArcFitTolerance = 1e-06
  AttachmentSupport = -> [Pad016]
  ExternalGeometry = -> [Pad016]
  FullyConstrained = true
  MakeInternals = false
  MapMode = 5
  Placement = pos=(0,0,-80.4316) rot=(1,0,0;3.14159rad)
  sketch-geometry (8):
    g0: LineSegment StartX=-215.932 StartY=3.6 StartZ=0 EndX=-205.932 EndY=3.6 EndZ=0
    g1: LineSegment StartX=-215.932 StartY=3.6 StartZ=0 EndX=-215.932 EndY=1.69e-14 EndZ=0
    g2: LineSegment [constr] StartX=-205.932 StartY=3.6 StartZ=0 EndX=-205.932 EndY=1.69e-14 EndZ=0
    g3: ArcOfEllipse CenterX=-205.932 CenterY=1.68e-14 CenterZ=0 NormalX=0 NormalY=0 NormalZ=1 MajorRadius=10 MinorRadius=3.6 AngleXU=-3.14159 StartAngle=4.71239 EndAngle=6.28319
    g4: LineSegment [constr] StartX=-215.932 StartY=1.68e-14 StartZ=0 EndX=-195.932 EndY=1.68e-14 EndZ=0
    g5: LineSegment [constr] StartX=-205.932 StartY=-3.6 StartZ=0 EndX=-205.932 EndY=3.6 EndZ=0
    g6: GeomPoint [constr] X=-215.262 Y=1.68e-14 Z=0
    g7: GeomPoint [constr] X=-196.602 Y=1.68e-14 Z=0
  constraints (13):
    c: Distance(g0) = 10
    c: Coincident(g0,g-5)
    c: PointOnObject(g0,g-5)
    c: Coincident(g1,g0)
    c: Coincident(g1,g-4)
    c: Coincident(g2,g0)
    c: Vertical(g2)
    c: PointOnObject(g2,g-3)
    c: InternalAlignment(g4-g7 -> g3) x4
    c: Coincident(g3,g2)
    c: Coincident(g3,g0)
    c: Coincident(g3,g1)
    c: Horizontal(g4)
FEATURE [PartDesign::SubtractivePipe] SubtractivePipe005
  AuxilleryCurvelinear = true
  AuxillerySpineTangent = false
  BaseFeature = -> SubtractivePipe004
  Binormal = (0,0,0)
  Mode = 0
  Profile = -> Sketch149
  Refine = true
  Spine = -> Pad016 [Edge256,Edge251,Edge252]
  SpineTangent = false
  Suppressed = false
  Transformation = 0
  Transition = 0
FEATURE [PartDesign::SubtractiveLoft] SubtractiveLoft002
  BaseFeature = -> SubtractivePipe005
  Closed = false
  Profile = -> Sketch129
  Refine = true
  Ruled = false
  Sections = -> [Sketch130]
  Suppressed = false
FEATURE [PartDesign::SubtractiveLoft] SubtractiveLoft003
  BaseFeature = -> SubtractiveLoft002
  Closed = false
  Profile = -> Clone2D001
  Refine = true
  Ruled = false
  Sections = -> [Sketch131]
  Suppressed = false
FEATURE [PartDesign::Chamfer] Chamfer010
  Angle = 45
  Base = -> SubtractiveLoft003 [Edge203,Edge204,Edge202,Edge201,Edge195]
  BaseFeature = -> SubtractiveLoft003
  ChamferType = 0
  FlipDirection = false
  Refine = true
  Size = 1.5
  Size2 = 1
  SupportTransform = false
  Suppressed = false
  UseAllEdges = false
FEATURE [PartDesign::Chamfer] Chamfer011
  Angle = 45
  Base = -> Chamfer010 [Edge15]
  BaseFeature = -> Chamfer010
  ChamferType = 0
  FlipDirection = false
  Refine = true
  Size = 1.6
  Size2 = 1
  SupportTransform = false
  Suppressed = false
  UseAllEdges = false
FEATURE [PartDesign::Chamfer] Chamfer012
  Angle = 45
  Base = -> Chamfer011 [Edge10]
  BaseFeature = -> Chamfer011
  ChamferType = 0
  FlipDirection = false
  Refine = true
  Size = 3.5
  Size2 = 1
  SupportTransform = false
  Suppressed = false
  UseAllEdges = false
FEATURE [PartDesign::Chamfer] Chamfer013
  Angle = 45
  Base = -> Chamfer012 [Edge94]
  BaseFeature = -> Chamfer012
  ChamferType = 0
  FlipDirection = false
  Refine = true
  Size = 1.9
  Size2 = 1
  SupportTransform = false
  Suppressed = false
  UseAllEdges = false
FEATURE [PartDesign::Fillet] Fillet007
  Base = -> Chamfer013 [Edge83]
  BaseFeature = -> Chamfer013
  Radius = 1.1
  Refine = true
  SupportTransform = false
  Suppressed = false
  UseAllEdges = false
FEATURE [PartDesign::Fillet] Fillet008
  Base = -> Fillet007 [Edge75]
  BaseFeature = -> Fillet007
  Radius = 1.9
  Refine = true
  SupportTransform = false
  Suppressed = false
  UseAllEdges = false
FEATURE [PartDesign::Pocket] Pocket011
  BaseFeature = -> Fillet008
  Direction = (0,1,-2e-16)
  Length = 0.8
  Length2 = 5
  Profile = -> Sketch132
  ReferenceAxis = -> Sketch132 [N_Axis]
  Refine = true
  Suppressed = false
  Type = 0
FEATURE [PartDesign::Pocket] Pocket012
  BaseFeature = -> Pocket011
  Direction = (0,1,0)
  Length = 1
  Length2 = 5
  Profile = -> ShapeString
  ReferenceAxis = -> ShapeString [N_Axis]
  Refine = true
  Suppressed = false
  Type = 0
FEATURE [PartDesign::Body] Body007  label="lato DX"
  AllowCompound = false
  Group = -> [Binder001,Sketch114,Pad011,Chamfer014,Sketch115,Pocket006,Sketch116,Pad012,Sketch117,Pocket007,Sketch118,Pad013,Sketch119,Pocket008,Pad017,Chamfer009,Pocket009,Sketch123,Sketch120,Pad014,Pad018,Chamfer008,Pocket010,Sketch121,Pad015,Sketch122,Pad016,SubtractivePipe004,SubtractivePipe005,Sketch149,Sketch148,Sketch124,Sketch125,Sketch126,Sketch129,Sketch130,Clone2D001,Sketch131,SubtractiveLoft002,+11 more]
  Origin = -> Origin007
  Tip = -> Pocket012
note: 2 file-system paths scrubbed to <path> (originals preserved in the JSON sidecar)
